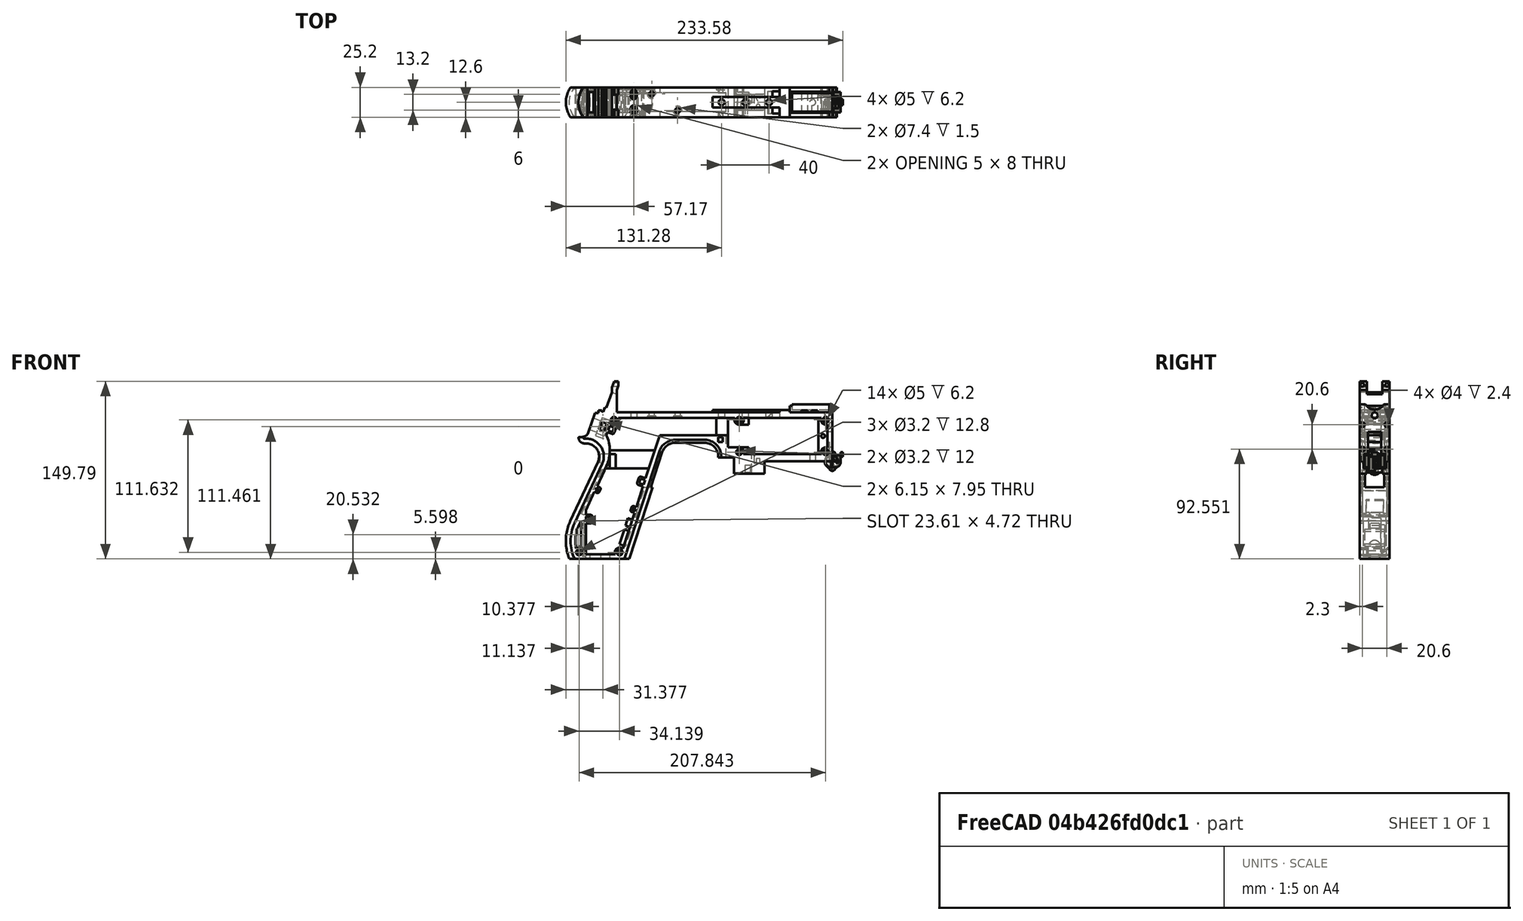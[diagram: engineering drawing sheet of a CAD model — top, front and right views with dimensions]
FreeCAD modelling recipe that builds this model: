
FCSTD DOCUMENT  (FreeCAD 1.0R39319 (Git))
Label: PICON-OF_ver_42
License: All rights reserved
LicenseURL: https://en.wikipedia.org/wiki/All_rights_reserved
objects: Sketcher::SketchObject×109, Part::Extrusion×52, Part::Cut×39, PartDesign::Pad×29, PartDesign::Pocket×18, PartDesign::Chamfer×15, PartDesign::Body×10, PartDesign::Fillet×6, PartDesign::SubtractivePipe×4, Part::Part2DObjectPython×4, PartDesign::SubtractiveLoft×4, PartDesign::Plane×2, PartDesign::SubShapeBinder×2, Part::Sweep×1, PartDesign::ShapeBinder×1, Part::MultiFuse×1, Mesh::Feature×1
note: 558 computed .brp shape members not serialized (recipe doc carries the construction recipe); baked Part::Feature solids carry a one-line shape summary decoded from their .brp

FEATURE [Sketcher::SketchObject] Sketch  label="corpo principale"
  ArcFitTolerance = 1e-06
  AttacherType = Attacher::AttachEngine3D
  AttachmentSupport = -> [XZ_Plane]
  FullyConstrained = true
  MakeInternals = false
  MapMode = 5
  Placement = pos=(0,0,0) rot=(1,0,0;1.5708rad)
  sketch-geometry (65):
    g0: LineSegment StartX=0 StartY=0 StartZ=0 EndX=-57.2 EndY=0 EndZ=0
    g1: LineSegment StartX=-57.2 StartY=0 StartZ=0 EndX=-57.2 EndY=-10.4 EndZ=0
    g2: LineSegment StartX=-57.2 StartY=-10.4 StartZ=0 EndX=-82.8 EndY=-10.4 EndZ=0
    g3: LineSegment StartX=-82.8 StartY=-10.4 StartZ=0 EndX=-82.8 EndY=3.2 EndZ=0
    g4: LineSegment StartX=-82.8 StartY=3.2 StartZ=0 EndX=-93.6 EndY=3.2 EndZ=0
    g5: LineSegment StartX=-93.6 StartY=3.2 StartZ=0 EndX=-93.6 EndY=4 EndZ=0
    g6: LineSegment StartX=-107.6 StartY=18 StartZ=0 EndX=-132.428 EndY=18 EndZ=0
    g7: LineSegment StartX=-145.743 StartY=8.32624 StartZ=0 EndX=-175.232 EndY=-82.4316 EndZ=0
    g8: LineSegment StartX=-175.232 StartY=-82.4316 StartZ=0 EndX=-217.232 EndY=-82.4316 EndZ=0
    g9: LineSegment StartX=-217.232 StartY=-52.1862 StartZ=0 EndX=-193.988 EndY=-2.33927 EndZ=0
    g10: LineSegment StartX=-206.196 StartY=23.0857 StartZ=0 EndX=-199.861 EndY=40.4914 EndZ=0
    g11: LineSegment StartX=-199.861 StartY=40.4914 StartZ=0 EndX=-197.061 EndY=40.4914 EndZ=0
    g12: LineSegment StartX=-197.061 StartY=40.4914 StartZ=0 EndX=-197.061 EndY=42.8914 EndZ=0
    g13: LineSegment StartX=-197.061 StartY=42.8914 StartZ=0 EndX=-194.261 EndY=42.8914 EndZ=0
    g14: LineSegment StartX=-194.261 StartY=42.8914 StartZ=0 EndX=-194.535 EndY=42.1397 EndZ=0
    g15: LineSegment StartX=-194.535 StartY=42.1397 StartZ=0 EndX=-193.031 EndY=41.5924 EndZ=0
    g16: LineSegment StartX=-193.031 StartY=41.5924 StartZ=0 EndX=-191.663 EndY=45.3512 EndZ=0
    g17: LineSegment StartX=-191.663 StartY=45.3512 StartZ=0 EndX=-190.536 EndY=44.9408 EndZ=0
    g18: LineSegment StartX=-190.536 StartY=44.9408 StartZ=0 EndX=-185.747 EndY=58.0965 EndZ=0
    g19: LineSegment StartX=-185.747 StartY=58.0965 StartZ=0 EndX=-185.747 EndY=62.0965 EndZ=0
    g20: LineSegment StartX=-185.747 StartY=62.0965 StartZ=0 EndX=-183.832 EndY=67.3588 EndZ=0
    g21: LineSegment StartX=-183.832 StartY=67.3588 StartZ=0 EndX=-180.232 EndY=67.3588 EndZ=0
    g22: LineSegment StartX=-180.232 StartY=67.3588 StartZ=0 EndX=-180.232 EndY=63.7588 EndZ=0
    g23: LineSegment StartX=-180.232 StartY=63.7588 StartZ=0 EndX=-181.6 EndY=60 EndZ=0
    g24: LineSegment StartX=-181.6 StartY=60 StartZ=0 EndX=-181.6 EndY=41.2 EndZ=0
    g25: LineSegment StartX=-181.6 StartY=41.2 StartZ=0 EndX=-100.8 EndY=41.2 EndZ=0
    g26: LineSegment StartX=-36 StartY=43.2 StartZ=0 EndX=-36 EndY=41.2 EndZ=0
    g27: LineSegment StartX=0 StartY=48 StartZ=0 EndX=0 EndY=0 EndZ=0
    g28: LineSegment StartX=-209.901 StartY=19.85 StartZ=0 EndX=-209.901 EndY=20.1 EndZ=0
    g29: LineSegment StartX=-208.001 StartY=22 StartZ=0 EndX=-207.747 EndY=22 EndZ=0
    g30: LineSegment StartX=-207.583 StartY=19 StartZ=0 EndX=-209.051 EndY=19 EndZ=0
    g31: ArcOfCircle CenterX=-208.001 CenterY=20.1 CenterZ=0 NormalX=0 NormalY=0 NormalZ=1 AngleXU=0 Radius=1.9 StartAngle=1.5708 EndAngle=3.14159
    g32: GeomPoint [constr] X=-209.901 Y=22 Z=0
    g33: ArcOfCircle CenterX=-209.051 CenterY=19.85 CenterZ=0 NormalX=0 NormalY=0 NormalZ=1 AngleXU=0 Radius=0.85 StartAngle=3.14159 EndAngle=4.71239
    g34: GeomPoint [constr] X=-209.901 Y=19 Z=0
    g35: ArcOfCircle CenterX=-207.747 CenterY=23.65 CenterZ=0 NormalX=0 NormalY=0 NormalZ=1 AngleXU=0 Radius=1.65 StartAngle=4.71239 EndAngle=5.93412
    g36: GeomPoint [constr] X=-206.591 Y=22 Z=0
    g37: LineSegment StartX=-4 StartY=6 StartZ=0 EndX=-4 EndY=36.4 EndZ=0
    g38: LineSegment StartX=-4 StartY=36.4 StartZ=0 EndX=-185.2 EndY=36.4 EndZ=0
    g39: LineSegment StartX=-185.2 StartY=36.4 StartZ=0 EndX=-190.441 EndY=22 EndZ=0
    g40: LineSegment StartX=-214.575 StartY=-78.4316 StartZ=0 EndX=-178.142 EndY=-78.4316 EndZ=0
    g41: LineSegment StartX=-178.142 StartY=-78.4316 StartZ=0 EndX=-145.51 EndY=22 EndZ=0
    g42: LineSegment StartX=-145.51 StartY=22 StartZ=0 EndX=-87.91 EndY=22 EndZ=0
    g43: LineSegment StartX=-87.91 StartY=22 StartZ=0 EndX=-87.91 EndY=11.6 EndZ=0
    g44: LineSegment StartX=-87.91 StartY=11.6 StartZ=0 EndX=-80.11 EndY=11.6 EndZ=0
    g45: LineSegment StartX=-80.11 StartY=11.6 StartZ=0 EndX=-80.11 EndY=6 EndZ=0
    g46: LineSegment StartX=-80.11 StartY=6 StartZ=0 EndX=-4 EndY=6 EndZ=0
    g47: LineSegment StartX=-190.363 StartY=-4.02975 StartZ=0 EndX=-213.607 EndY=-53.8767 EndZ=0
    g48: ArcOfCircle CenterX=-132.428 CenterY=4 CenterZ=0 NormalX=0 NormalY=0 NormalZ=1 AngleXU=0 Radius=14 StartAngle=1.5708 EndAngle=2.82743
    g49: GeomPoint [constr] X=-142.6 Y=18 Z=0
    g50: ArcOfCircle CenterX=-107.6 CenterY=4 CenterZ=0 NormalX=0 NormalY=0 NormalZ=1 AngleXU=0 Radius=14 StartAngle=0 EndAngle=1.5708
    g51: GeomPoint [constr] X=-93.6 Y=18 Z=0
    g52: ArcOfCircle CenterX=-184.801 CenterY=-67.3089 CenterZ=0 NormalX=0 NormalY=0 NormalZ=1 AngleXU=0 Radius=35.7833 StartAngle=2.70526 EndAngle=3.57792
    g53: ArcOfCircle CenterX=-207.583 CenterY=4 CenterZ=0 NormalX=0 NormalY=0 NormalZ=1 AngleXU=0 Radius=15 StartAngle=5.84685 EndAngle=7.85398
    g54: LineSegment [constr] StartX=-213.607 StartY=-53.8767 StartZ=0 EndX=-217.232 EndY=-52.1862 EndZ=0
    g55: ArcOfCircle CenterX=-184.801 CenterY=-67.3089 CenterZ=0 NormalX=0 NormalY=0 NormalZ=1 AngleXU=0 Radius=31.7833 StartAngle=2.70526 EndAngle=3.49911
    g56: ArcOfCircle CenterX=-218.095 CenterY=8.90192 CenterZ=0 NormalX=0 NormalY=0 NormalZ=1 AngleXU=0 Radius=30.5989 StartAngle=5.84685 EndAngle=6.72553
    g57: LineSegment StartX=-44.6 StartY=43.2 StartZ=0 EndX=-36 EndY=43.2 EndZ=0
    g58: LineSegment StartX=-100.8 StartY=41.2 StartZ=0 EndX=-44.6 EndY=41.2 EndZ=0
    g59: LineSegment StartX=-44.6 StartY=41.2 StartZ=0 EndX=-44.6 EndY=43.2 EndZ=0
    g60: LineSegment StartX=-2.4 StartY=48 StartZ=0 EndX=0 EndY=48 EndZ=0
    g61: LineSegment StartX=-36 StartY=41.2 StartZ=0 EndX=-2.4 EndY=41.2 EndZ=0
    g62: LineSegment StartX=-2.4 StartY=41.2 StartZ=0 EndX=-2.4 EndY=48 EndZ=0
    g63: LineSegment [constr] StartX=-181.6 StartY=36.4 StartZ=0 EndX=-152.209 EndY=36.4 EndZ=0
    g64: LineSegment [constr] StartX=-181.6 StartY=36.4 StartZ=0 EndX=-130.41 EndY=36.4 EndZ=0
  constraints (183):
    c: Coincident(g-1,g0)
    c: PointOnObject(g0,g-1)
    c: Coincident(g0,g1)
    c: Vertical(g1)
    c: Coincident(g1,g2)
    c: Horizontal(g2)
    c: Coincident(g2,g3)
    c: Vertical(g3)
    c: Coincident(g3,g4)
    c: Coincident(g4,g5)
    c: Vertical(g5)
    c: Horizontal(g6)
    c: Coincident(g7,g8)
    c: Horizontal(g8)
    c: Coincident(g10,g11)
    c: Horizontal(g11)
    c: Coincident(g11,g12)
    c: Vertical(g12)
    c: Coincident(g12,g13)
    c: Horizontal(g13)
    c: Coincident(g13,g14)
    c: Coincident(g14,g15)
    c: Coincident(g15,g16)
    c: Coincident(g16,g17)
    c: Coincident(g17,g18)
    c: Coincident(g18,g19)
    c: Vertical(g19)
    c: Coincident(g19,g20)
    c: Coincident(g20,g21)
    c: Horizontal(g21)
    c: Coincident(g21,g22)
    c: Vertical(g22)
    c: Coincident(g22,g23)
    c: Coincident(g23,g24)
    c: Vertical(g24)
    c: Coincident(g24,g25)
    c: Horizontal(g25)
    c: Coincident(g57,g26)
    c: Vertical(g26)
    c: Coincident(g26,g61)
    c: PointOnObject(g60,g-2)
    c: Coincident(g60,g27)
    c: Coincident(g27,g0)
    c: DistanceY(g27,g27) = 48
    c: DistanceY(g1,g1) = 10.4
    c: DistanceX(g0,g0) = 57.2
    c: DistanceX(g2,g2) = 25.6
    c: Horizontal(g4)
    c: DistanceY(g3,g3) = 13.6
    c: DistanceX(g4,g4) = 10.8
    c: DistanceY(g5,g51) = 14.8
    c: DistanceX(g49,g51) = 49
    c: Distance(g7,g49) = 105.6
    c: DistanceX(g61,g60) = 36
    c: DistanceX(g25,g25) = 80.8
    c: DistanceY(g24,g24) = 18.8
    c: DistanceY(g22,g22) = 3.6
    c: Distance(g23) = 4
    c: Angle(g-1,g23) = 1.22173
    c: DistanceX(g21,g21) = 3.6
    c: Distance(g20) = 5.6
    c: Angle(g-1,g20) = 1.22173
    c: DistanceY(g19,g19) = 4
    c: Distance(g18) = 14
    c: Angle(g-1,g18) = 1.22173
    c: Distance(g17) = 1.2
    c: Distance(g16) = 4
    c: Angle(g16) = 1.22173
    c: Perpendicular(g18,g17)
    c: Distance(g15) = 1.6
    c: Perpendicular(g16,g15)
    c: Distance(g14) = 0.8
    c: DistanceX(g13,g13) = 2.8
    c: Perpendicular(g15,g14)
    c: DistanceY(g12,g12) = 2.4
    c: DistanceX(g11,g11) = 2.8
    c: Distance(g9) = 55
    c: Angle(g9,g-1) = 2.00713
    c: Horizontal(g29)
    c: Vertical(g28)
    c: Horizontal(g30)
    c: PointOnObject(g32,g29)
    c: PointOnObject(g32,g28)
    c: Tangent(g29,g31) = 1.5708
    c: Tangent(g28,g31) = 1.5708
    c: PointOnObject(g34,g28)
    c: PointOnObject(g34,g30)
    c: Tangent(g28,g33) = 1.5708
    c: Tangent(g30,g33) = 1.5708
    c: PointOnObject(g36,g29)
    c: PointOnObject(g36,g10)
    c: Tangent(g29,g35) = -1.5708
    c: Tangent(g10,g35) = -1.5708
    c: Angle(g-1,g10) = 1.22173
    c: Radius(g35) = 1.65
    c: Vertical(g37)
    c: Coincident(g37,g38)
    c: Horizontal(g38)
    c: Coincident(g38,g39)
    c: Horizontal(g40)
    c: Coincident(g40,g41)
    c: Coincident(g41,g42)
    c: Horizontal(g42)
    c: Coincident(g42,g43)
    c: Vertical(g43)
    c: Coincident(g43,g44)
    c: Horizontal(g44)
    c: Coincident(g44,g45)
    c: Vertical(g45)
    c: Coincident(g45,g46)
    c: Coincident(g46,g37)
    c: Horizontal(g46)
    c: DistanceY(g0,g37) = 6
    c: DistanceX(g37,g0) = 4
    c: DistanceY(g37,g25) = 4.8
    c: DistanceX(g38,g38) = 181.2
    c: DistanceX(g42,g42) = 57.6
    c: DistanceY(g49,g41) = 4
    c: DistanceX(g41,g49) = 2.91
    c: DistanceY(g43,g43) = 10.4
    c: DistanceX(g44,g44) = 7.8
    c: DistanceY(g7,g40) = 4
    c: Distance(g47) = 55
    c: Angle(g-1,g39) = 1.22173
    c: PointOnObject(g49,g7)
    c: PointOnObject(g49,g6)
    c: Tangent(g7,g48) = -1.5708
    c: Tangent(g6,g48) = -1.5708
    c: PointOnObject(g51,g5)
    c: PointOnObject(g51,g6)
    c: Tangent(g5,g50) = -1.5708
    c: Tangent(g6,g50) = -1.5708
    c: Radius(g50) = 14
    c: Radius(g48) = 14
    c: DistanceX(g8,g8) = 42
    c: Angle(g7,g-1) = 1.88496
    c: Parallel(g41,g7)
    c: Parallel(g47,g9)
    c: Coincident(g52,g8)
    c: Tangent(g52,g9) = 1.5708
    c: DistanceX(g9,g8) = 0
    c: Tangent(g53,g9) = -1.5708
    c: Tangent(g53,g30) = -1.5708
    c: Diameter(g53) = 30
    c: DistanceY(g53,g0) = -4
    c: Coincident(g54,g47)
    c: Distance(g54) = 4
    c: Coincident(g54,g9)
    c: Coincident(g55,g40)
    c: Tangent(g55,g47) = -1.5708
    c: Coincident(g52,g55)
    c: Coincident(g56,g39)
    c: Tangent(g56,g47) = 1.5708
    c: Horizontal(g57)
    c: DistanceX(g57,g57) = 8.6
    c: Coincident(g58,g25)
    c: Horizontal(g58)
    c: Coincident(g59,g58)
    c: Vertical(g59)
    c: DistanceY(g58,g57) = 2
    c: DistanceX(g58,g58) = 56.2
    c: Coincident(g59,g57)
    c: DistanceY(g41,g36) = 0
    c: DistanceY(g36,g39) = 0
    c: DistanceY(g28,g28) = 0.25
    c: DistanceX(g30,g36) = 2.46
    c: DistanceX(g28,g29) = 1.9
    c: Coincident(g62,g60)
    c: Horizontal(g60)
    c: DistanceX(g62,g27) = 2.4
    c: Coincident(g61,g62)
    c: DistanceY(g26,g26) = 2
    c: Vertical(g62)
    c: DistanceY(g61,g60) = 6.8
    c: Horizontal(g61)
    c: Distance(g63) = 29.391
    c: PointOnObject(g63,g38)
    c: PointOnObject(g63,g38)
    c: Distance(g64) = 51.19
    c: PointOnObject(g64,g38)
    c: PointOnObject(g64,g38)
    c: DistanceX(g24,g63) = 0
    c: DistanceX(g24,g64) = 0
FEATURE [Part::Extrusion] Extrude  label="Extrude corpo principale"
  Base = -> Sketch
  Dir = (0,-1,2e-16)
  DirMode = 2
  FaceMakerClass = Part::FaceMakerBullseye
  FaceMakerMode = 3
  LengthFwd = 25.2
  LengthRev = 12.6
  Solid = true
  Symmetric = true
FEATURE [Sketcher::SketchObject] Sketch002  label="scavo grilletto"
  ArcFitTolerance = 1e-06
  AttachmentSupport = -> [XZ_Plane]
  ExternalGeometry = -> [Sketch]
  FullyConstrained = true
  MakeInternals = false
  MapMode = 5
  Placement = pos=(0,0,0) rot=(1,0,0;1.5708rad)
  sketch-geometry (4):
    g0: LineSegment StartX=-89.51 StartY=22 StartZ=0 EndX=-152.71 EndY=22 EndZ=0
    g1: LineSegment StartX=-152.71 StartY=22 StartZ=0 EndX=-167.006 EndY=-22 EndZ=0
    g2: LineSegment StartX=-167.006 StartY=-22 StartZ=0 EndX=-89.51 EndY=-22 EndZ=0
    g3: LineSegment StartX=-89.51 StartY=-22 StartZ=0 EndX=-89.51 EndY=22 EndZ=0
  constraints (12):
    c: Horizontal(g0)
    c: Coincident(g0,g1)
    c: Coincident(g1,g2)
    c: Horizontal(g2)
    c: Coincident(g2,g3)
    c: Coincident(g3,g0)
    c: Vertical(g3)
    c: Angle(g1,g0) = 1.88496
    c: DistanceY(g3,g3) = 44
    c: DistanceX(g0,g0) = 63.2
    c: DistanceX(g0,g-3) = 1.6
    c: DistanceY(g-3,g0) = 0
FEATURE [Sketcher::SketchObject] Sketch004  label="traiettoria arrotondamento impugnatura anteriore"
  ArcFitTolerance = 1e-06
  AttachmentSupport = -> [XZ_Plane]
  ExternalGeometry = -> [Sketch]
  FullyConstrained = true
  MakeInternals = false
  MapMode = 5
  Placement = pos=(0,0,0) rot=(1,0,0;1.5708rad)
  sketch-geometry (13):
    g0: LineSegment StartX=-175.232 StartY=-82.4316 StartZ=0 EndX=-145.743 EndY=8.32624 EndZ=0
    g1: LineSegment StartX=-93.6 StartY=3.2 StartZ=0 EndX=-93.6 EndY=4 EndZ=0
    g2: LineSegment StartX=-132.428 StartY=18 StartZ=0 EndX=-107.6 EndY=18 EndZ=0
    g3: ArcOfCircle CenterX=-132.428 CenterY=4 CenterZ=0 NormalX=0 NormalY=0 NormalZ=1 AngleXU=0 Radius=14 StartAngle=1.5708 EndAngle=2.82743
    g4: ArcOfCircle CenterX=-107.6 CenterY=4 CenterZ=0 NormalX=0 NormalY=0 NormalZ=1 AngleXU=0 Radius=14 StartAngle=0 EndAngle=1.5708
    g5: LineSegment StartX=-175.232 StartY=-82.4316 StartZ=0 EndX=-217.232 EndY=-82.4316 EndZ=0
    g6: LineSegment StartX=-217.232 StartY=-52.1862 StartZ=0 EndX=-193.988 EndY=-2.33927 EndZ=0
    g7: LineSegment StartX=-209.051 StartY=19 StartZ=0 EndX=-207.583 EndY=19 EndZ=0
    g8: LineSegment StartX=-209.901 StartY=20.1 StartZ=0 EndX=-209.901 EndY=19.85 EndZ=0
    g9: ArcOfCircle CenterX=-184.801 CenterY=-67.3089 CenterZ=0 NormalX=0 NormalY=0 NormalZ=1 AngleXU=0 Radius=35.7833 StartAngle=2.70526 EndAngle=3.57792
    g10: ArcOfCircle CenterX=-207.583 CenterY=4 CenterZ=0 NormalX=0 NormalY=0 NormalZ=1 AngleXU=0 Radius=15 StartAngle=5.84685 EndAngle=7.85398
    g11: ArcOfCircle CenterX=-209.051 CenterY=19.85 CenterZ=0 NormalX=0 NormalY=0 NormalZ=1 AngleXU=0 Radius=0.85 StartAngle=3.14159 EndAngle=4.71239
    g12: ArcOfCircle CenterX=-208.001 CenterY=20.1 CenterZ=0 NormalX=0 NormalY=0 NormalZ=1 AngleXU=0 Radius=1.9 StartAngle=1.5708 EndAngle=3.14159
  constraints (26):
    c: Coincident(g0,g-3)
    c: Coincident(g0,g-6)
    c: Coincident(g1,g-8)
    c: Coincident(g1,g-7)
    c: Coincident(g2,g-5)
    c: Coincident(g2,g-4)
    c: Coincident(g3,g2)
    c: Tangent(g3,g0) = 1.5708
    c: Coincident(g4,g1)
    c: Tangent(g4,g2) = 1.5708
    c: Coincident(g5,g0)
    c: Coincident(g5,g-9)
    c: Coincident(g6,g-12)
    c: Coincident(g6,g-11)
    c: Coincident(g7,g-15)
    c: Coincident(g7,g-14)
    c: Coincident(g8,g-16)
    c: Coincident(g8,g-17)
    c: Tangent(g9,g6) = 1.5708
    c: Coincident(g9,g5)
    c: Coincident(g10,g7)
    c: Tangent(g10,g6) = -1.5708
    c: Tangent(g11,g7) = -1.5708
    c: Coincident(g11,g8)
    c: Tangent(g12,g8) = -1.5708
    c: Coincident(g12,g-17)
FEATURE [PartDesign::Plane] DatumPlane  label="Piano per disegno arrotondamento impugnatura"
  AttachmentSupport = -> [Sketch]
  Length = 73.6581
  MapMode = 7
  Placement = pos=(-145.743,1.8e-15,8.32624) rot=(0.154555,0.154555,0.97582;1.59527rad)
  ResizeMode = 0
  Width = 303.511
FEATURE [Sketcher::SketchObject] Sketch005  label="forma arrotondamento impugnatura anteriore"
  ArcFitTolerance = 1e-06
  AttachmentSupport = -> [DatumPlane]
  FullyConstrained = true
  MakeInternals = false
  MapMode = 5
  Placement = pos=(-145.743,1.8e-15,8.32624) rot=(0.154555,0.154555,0.97582;1.59527rad)
  sketch-geometry (5):
    g0: GeomPoint [constr] X=0 Y=-4 Z=0
    g1: GeomPoint [constr] X=-12.6 Y=7.1e-15 Z=0
    g2: GeomPoint [constr] X=12.6 Y=4.97e-14 Z=0
    g3: LineSegment StartX=-12.6 StartY=7.1e-15 StartZ=0 EndX=12.6 EndY=4.97e-14 EndZ=0
    g4: ArcOfCircle CenterX=-3.88e-14 CenterY=17.845 CenterZ=0 NormalX=0 NormalY=0 NormalZ=1 AngleXU=0 Radius=21.845 StartAngle=4.09759 EndAngle=5.32718
  constraints (11):
    c: DistanceY(g0,g-1) = 4
    c: DistanceX(g-1,g0) = 0
    c: DistanceX(g1,g-1) = 12.6
    c: DistanceX(g-1,g2) = 12.6
    c: DistanceY(g-1,g2) = 0
    c: DistanceY(g-1,g1) = 0
    c: Coincident(g3,g1)
    c: Coincident(g3,g2)
    c: Coincident(g4,g1)
    c: Coincident(g4,g2)
    c: PointOnObject(g0,g4)
FEATURE [Part::Sweep] Sweep  label="Sweep impugnatura"
  Frenet = true
  Sections = -> [Sketch005]
  Solid = true
  Spine = -> Sketch [Edge32,Edge33,Edge34,Edge35,Edge36,Edge37,Edge38,Edge39,Edge40,Edge41,Edge42,Edge43,Edge44]
  Transition = 1
FEATURE [Sketcher::SketchObject] Sketch008  label="buchi e pulizie varie"
  ArcFitTolerance = 1e-06
  AttachmentSupport = -> [XZ_Plane]
  ExternalGeometry = -> [Sketch]
  FullyConstrained = true
  MakeInternals = false
  MapMode = 5
  Placement = pos=(0,0,0) rot=(1,0,0;1.5708rad)
  sketch-geometry (26):
    g0: LineSegment StartX=-96.278 StartY=20.155 StartZ=0 EndX=-92.278 EndY=20.155 EndZ=0
    g1: LineSegment StartX=-92.278 StartY=20.155 StartZ=0 EndX=-92.278 EndY=16.155 EndZ=0
    g2: LineSegment StartX=-92.278 StartY=16.155 StartZ=0 EndX=-96.278 EndY=16.155 EndZ=0
    g3: LineSegment StartX=-96.278 StartY=16.155 StartZ=0 EndX=-96.278 EndY=20.155 EndZ=0
    g4: LineSegment StartX=-222.232 StartY=-82.4316 StartZ=0 EndX=-170.232 EndY=-82.4316 EndZ=0
    g5: LineSegment StartX=-170.232 StartY=-82.4316 StartZ=0 EndX=-170.232 EndY=-86.4316 EndZ=0
    g6: LineSegment StartX=-170.232 StartY=-86.4316 StartZ=0 EndX=-222.232 EndY=-86.4316 EndZ=0
    g7: LineSegment StartX=-222.232 StartY=-86.4316 StartZ=0 EndX=-222.232 EndY=-82.4316 EndZ=0
    g8: LineSegment StartX=-213.901 StartY=20.1 StartZ=0 EndX=-213.901 EndY=26 EndZ=0
    g9: LineSegment StartX=-213.901 StartY=26 StartZ=0 EndX=-206.196 EndY=26 EndZ=0
    g10: LineSegment StartX=-17.4 StartY=42.8 StartZ=0 EndX=-12.4 EndY=42.8 EndZ=0
    g11: LineSegment StartX=-12.4 StartY=42.8 StartZ=0 EndX=-12.4 EndY=41.2 EndZ=0
    g12: LineSegment StartX=-12.4 StartY=41.2 StartZ=0 EndX=-17.4 EndY=41.2 EndZ=0
    g13: LineSegment StartX=-17.4 StartY=41.2 StartZ=0 EndX=-17.4 EndY=42.8 EndZ=0
    g14: LineSegment StartX=-25.9 StartY=42.8 StartZ=0 EndX=-20.9 EndY=42.8 EndZ=0
    g15: LineSegment StartX=-20.9 StartY=42.8 StartZ=0 EndX=-20.9 EndY=41.2 EndZ=0
    g16: LineSegment StartX=-20.9 StartY=41.2 StartZ=0 EndX=-25.9 EndY=41.2 EndZ=0
    g17: LineSegment StartX=-25.9 StartY=41.2 StartZ=0 EndX=-25.9 EndY=42.8 EndZ=0
    g18: GeomPoint [constr] X=-206.196 Y=23.0857 Z=0
    g19: GeomPoint [constr] X=-213.901 Y=20.1 Z=0
    g20: BSplineCurve PolesCount=4 KnotsCount=2 Degree=3 IsPeriodic=0
    g21-g24: Circle [constr] x4 (B-spline internal-alignment scaffolding for g20; pole/knot coordinates omitted)
    g25: LineSegment StartX=-206.196 StartY=26 StartZ=0 EndX=-206.196 EndY=23.0857 EndZ=0
  constraints (73):
    c: Horizontal(g0)
    c: Coincident(g1,g0)
    c: Vertical(g1)
    c: Coincident(g2,g1)
    c: Horizontal(g2)
    c: Coincident(g3,g2)
    c: Coincident(g3,g0)
    c: Vertical(g3)
    c: DistanceX(g0,g-4) = 4.368
    c: DistanceY(g0,g-4) = 1.845
    c: DistanceY(g1,g1) = 4
    c: DistanceX(g2,g2) = 4
    c: Horizontal(g4)
    c: Coincident(g5,g4)
    c: Vertical(g5)
    c: Coincident(g6,g5)
    c: Horizontal(g6)
    c: Coincident(g7,g6)
    c: Coincident(g7,g4)
    c: Vertical(g7)
    c: DistanceY(g7,g7) = 4
    c: DistanceX(g4,g-5) = 5
    c: DistanceX(g-5,g4) = 5
    c: DistanceY(g4,g-5) = 0
    c: Coincident(g9,g8)
    c: Parallel(g9,g-6)
    c: DistanceX(g8,g-8) = 4
    c: Horizontal(g10)
    c: Coincident(g11,g10)
    c: Vertical(g11)
    c: Coincident(g12,g11)
    c: Horizontal(g12)
    c: Coincident(g13,g12)
    c: Coincident(g13,g10)
    c: Vertical(g13)
    c: Horizontal(g14)
    c: Coincident(g15,g14)
    c: Vertical(g15)
    c: Coincident(g16,g15)
    c: Horizontal(g16)
    c: Coincident(g17,g16)
    c: Coincident(g17,g14)
    c: Vertical(g17)
    c: DistanceY(g11,g10) = 1.6
    c: DistanceX(g10,g10) = 5
    c: DistanceY(g15,g14) = 1.6
    c: DistanceX(g14,g14) = 5
    c: DistanceX(g15,g12) = 3.5
    c: DistanceX(g11,g-9) = 10
    c: DistanceY(g-9,g11) = 0
    c: DistanceY(g-9,g15) = 0
    c: Perpendicular(g8,g9)
    c: DistanceY(g-7,g9) = 4
    c: DistanceY(g8,g-8) = 0
    c: InternalAlignment(g18,g20)
    c: InternalAlignment(g19,g20)
    c: InternalAlignment(g21,g20)
    c: Weight(g21) = 1
    c: InternalAlignment(g22,g20)
    c: Equal(g22,g21)
    c: InternalAlignment(g23,g20)
    c: Equal(g23,g21)
    c: InternalAlignment(g24,g20)
    c: Equal(g24,g21)
    c: Coincident(g18,g-12)
    c: Coincident(g19,g8)
    c: Coincident(g25,g9)
    c: Coincident(g25,g20)
    c: Vertical(g25)
    c: DistanceY(g20,g23) = 0
    c: DistanceY(g22,g18) = 2.26
    c: DistanceX(g22,g18) = 0.93
    c: DistanceX(g20,g23) = 2.9
FEATURE [Part::Extrusion] Extrude004  label="Extrude Buchi e pulizie varie"
  Base = -> Sketch008
  Dir = (0,-1,2e-16)
  DirMode = 2
  FaceMakerClass = Part::FaceMakerBullseye
  FaceMakerMode = 3
  LengthFwd = 25.2
  LengthRev = 0
  Solid = true
  Symmetric = true
FEATURE [Sketcher::SketchObject] Sketch009  label="rinforzi"
  ArcFitTolerance = 1e-06
  AttachmentSupport = -> [XZ_Plane]
  ExternalGeometry = -> [Sketch]
  FullyConstrained = true
  MakeInternals = false
  MapMode = 5
  Placement = pos=(0,0,0) rot=(1,0,0;1.5708rad)
  sketch-geometry (9):
    g0: LineSegment StartX=-87.91 StartY=22 StartZ=0 EndX=-87.91 EndY=36.4 EndZ=0
    g1: LineSegment StartX=-87.91 StartY=36.4 StartZ=0 EndX=-97.91 EndY=36.4 EndZ=0
    g2: LineSegment StartX=-97.91 StartY=36.4 StartZ=0 EndX=-97.91 EndY=22 EndZ=0
    g3: LineSegment StartX=-97.91 StartY=22 StartZ=0 EndX=-87.91 EndY=22 EndZ=0
    g4: LineSegment StartX=-149.713 StartY=9.06563 StartZ=0 EndX=-154.586 EndY=-5.93437 EndZ=0
    g5: LineSegment StartX=-154.586 StartY=-5.93437 StartZ=0 EndX=-191.863 EndY=-5.93437 EndZ=0
    g6: LineSegment StartX=-191.863 StartY=-5.93437 StartZ=0 EndX=-191.863 EndY=9.06563 EndZ=0
    g7: LineSegment StartX=-191.863 StartY=9.06563 StartZ=0 EndX=-149.713 EndY=9.06563 EndZ=0
    g8: LineSegment [constr] StartX=-145.51 StartY=22 StartZ=0 EndX=-149.713 EndY=9.06563 EndZ=0
  constraints (25):
    c: Vertical(g0)
    c: Coincident(g1,g0)
    c: Horizontal(g1)
    c: Coincident(g2,g1)
    c: Vertical(g2)
    c: Coincident(g3,g2)
    c: Coincident(g3,g0)
    c: Horizontal(g3)
    c: Coincident(g0,g-4)
    c: DistanceX(g3,g3) = 10
    c: DistanceY(g0,g-3) = 0
    c: Coincident(g5,g4)
    c: Horizontal(g5)
    c: Coincident(g6,g5)
    c: Vertical(g6)
    c: Coincident(g7,g6)
    c: Coincident(g7,g4)
    c: Horizontal(g7)
    c: Distance(g8) = 13.6
    c: Parallel(g-6,g8)
    c: Coincident(g-6,g8)
    c: Parallel(g4,g-6)
    c: DistanceY(g4,g4) = 15
    c: Coincident(g4,g8)
    c: DistanceX(g-5,g5) = -1.5
FEATURE [Part::Extrusion] Extrude001  label="Extrude scavo grilletto"
  Base = -> Sketch002
  Dir = (0,-1,2e-16)
  DirMode = 2
  FaceMakerClass = Part::FaceMakerBullseye
  FaceMakerMode = 3
  LengthFwd = 16
  LengthRev = 0
  Solid = true
  Symmetric = true
FEATURE [Part::Extrusion] Extrude005  label="Extrude Rinforzi"
  Base = -> Sketch009
  Dir = (0,-1,2e-16)
  DirMode = 2
  FaceMakerClass = Part::FaceMakerBullseye
  FaceMakerMode = 3
  LengthFwd = 2
  LengthRev = 0
  Placement = pos=(0,12.6,0) rot=(0,0,1;0rad)
  Solid = true
  Symmetric = false
FEATURE [PartDesign::ShapeBinder] CopyCut
  TraceSupport = false
FEATURE [PartDesign::Plane] DatumPlane001
  AttachmentSupport = -> [CopyCut]
  Length = 283.944
  MapMode = 5
  Placement = pos=(0,12.6,0) rot=(0,0.707107,0.707107;3.14159rad)
  ResizeMode = 0
  Width = 188.15
FEATURE [Sketcher::SketchObject] Sketch010  label="buco neopixel"
  ArcFitTolerance = 1e-06
  AttachmentSupport = -> [XZ_Plane]
  ExternalGeometry = -> [Sketch]
  FullyConstrained = true
  MakeInternals = false
  MapMode = 5
  Placement = pos=(0,0,0) rot=(1,0,0;1.5708rad)
  sketch-geometry (5):
    g0: LineSegment [constr] StartX=-199.861 StartY=40.4914 StartZ=0 EndX=-201.368 EndY=36.3521 EndZ=0
    g1: LineSegment StartX=-201.368 StartY=36.3521 StartZ=0 EndX=-204.932 EndY=26.5605 EndZ=0
    g2: LineSegment StartX=-201.368 StartY=36.3521 StartZ=0 EndX=-180.2 EndY=28.6477 EndZ=0
    g3: LineSegment StartX=-180.2 StartY=28.6477 StartZ=0 EndX=-183.764 EndY=18.8561 EndZ=0
    g4: LineSegment StartX=-183.764 StartY=18.8561 StartZ=0 EndX=-204.932 EndY=26.5605 EndZ=0
  constraints (14):
    c: Parallel(g0,g-3)
    c: Distance(g0) = 4.405
    c: Coincident(g0,g-3)
    c: Coincident(g2,g1)
    c: Coincident(g3,g2)
    c: Coincident(g4,g3)
    c: Coincident(g4,g1)
    c: Parallel(g1,g-3)
    c: Distance(g1) = 10.42
    c: Coincident(g1,g0)
    c: Parallel(g2,g4)
    c: Perpendicular(g1,g2)
    c: DistanceX(g-4,g2) = 5
    c: Parallel(g3,g1)
FEATURE [Part::Extrusion] Extrude006  label="Extrude buco neopixel"
  Base = -> Sketch010
  Dir = (0,-1,2e-16)
  DirMode = 2
  FaceMakerClass = Part::FaceMakerBullseye
  FaceMakerMode = 3
  LengthFwd = 17.2
  LengthRev = 0
  Solid = true
  Symmetric = true
FEATURE [Sketcher::SketchObject] Sketch011  label="fermo grilletto"
  ArcFitTolerance = 1e-06
  AttachmentSupport = -> [XZ_Plane]
  ExternalGeometry = -> [Sketch]
  FullyConstrained = true
  MakeInternals = false
  MapMode = 5
  Placement = pos=(0,0,0) rot=(1,0,0;1.5708rad)
  sketch-geometry (18):
    g0: LineSegment [constr] StartX=-145.51 StartY=22 StartZ=0 EndX=-157.347 EndY=-14.4293 EndZ=0
    g1: LineSegment [constr] StartX=-157.347 StartY=-14.4293 StartZ=0 EndX=-157.841 EndY=-15.951 EndZ=0
    g2: LineSegment StartX=-161.151 StartY=-13.1932 StartZ=0 EndX=-155.825 EndY=-14.9237 EndZ=0
    g3: LineSegment StartX=-163.167 StartY=-14.2205 StartZ=0 EndX=-164.403 EndY=-18.0247 EndZ=0
    g4: LineSegment StartX=-163.376 StartY=-20.0408 StartZ=0 EndX=-158.05 EndY=-21.7713 EndZ=0
    g5: LineSegment StartX=-158.05 StartY=-21.7713 StartZ=0 EndX=-155.825 EndY=-14.9237 EndZ=0
    g6: LineSegment StartX=-161.645 StartY=-14.7149 StartZ=0 EndX=-157.841 EndY=-15.951 EndZ=0
    g7: LineSegment StartX=-157.841 StartY=-15.951 StartZ=0 EndX=-159.077 EndY=-19.7552 EndZ=0
    g8: LineSegment StartX=-159.077 StartY=-19.7552 StartZ=0 EndX=-162.881 EndY=-18.5191 EndZ=0
    g9: LineSegment StartX=-162.881 StartY=-18.5191 StartZ=0 EndX=-161.645 EndY=-14.7149 EndZ=0
    g10: LineSegment [constr] StartX=-161.645 StartY=-14.7149 StartZ=0 EndX=-161.151 EndY=-13.1932 EndZ=0
    g11: LineSegment [constr] StartX=-159.077 StartY=-19.7552 StartZ=0 EndX=-157.555 EndY=-20.2496 EndZ=0
    g12: LineSegment [constr] StartX=-159.077 StartY=-19.7552 StartZ=0 EndX=-159.572 EndY=-21.2769 EndZ=0
    g13: LineSegment [constr] StartX=-161.645 StartY=-14.7149 StartZ=0 EndX=-163.167 EndY=-14.2205 EndZ=0
    g14: ArcOfCircle CenterX=-161.645 CenterY=-14.7149 CenterZ=0 NormalX=0 NormalY=0 NormalZ=1 AngleXU=0 Radius=1.6 StartAngle=1.25664 EndAngle=2.82743
    g15: GeomPoint [constr] X=-162.673 Y=-12.6988 Z=0
    g16: ArcOfCircle CenterX=-162.881 CenterY=-18.5191 CenterZ=0 NormalX=0 NormalY=0 NormalZ=1 AngleXU=0 Radius=1.6 StartAngle=2.82743 EndAngle=4.39823
    g17: GeomPoint [constr] X=-164.897 Y=-19.5464 Z=0
  constraints (48):
    c: Parallel(g0,g-3)
    c: Distance(g0) = 38.304
    c: Coincident(g0,g-3)
    c: Parallel(g1,g-3)
    c: Distance(g1) = 1.6
    c: Coincident(g1,g0)
    c: Coincident(g5,g4)
    c: Coincident(g5,g2)
    c: Coincident(g7,g6)
    c: Coincident(g8,g7)
    c: Coincident(g9,g8)
    c: Coincident(g9,g6)
    c: Parallel(g7,g-3)
    c: Parallel(g9,g7)
    c: Perpendicular(g6,g7)
    c: Parallel(g6,g8)
    c: Distance(g6) = 4
    c: Distance(g9) = 4
    c: Parallel(g5,g7)
    c: Parallel(g9,g3)
    c: Parallel(g2,g6)
    c: Parallel(g4,g8)
    c: Parallel(g13,g6)
    c: Parallel(g10,g9)
    c: Parallel(g11,g8)
    c: Parallel(g12,g7)
    c: Distance(g10) = 1.6
    c: Distance(g13) = 1.6
    c: Distance(g12) = 1.6
    c: Distance(g11) = 1.6
    c: Coincident(g10,g6)
    c: Coincident(g13,g6)
    c: Coincident(g12,g7)
    c: Coincident(g11,g7)
    c: Distance(g10,g15) = 1.6
    c: Distance(g15,g13) = 1.6
    c: Distance(g4,g12) = 1.6
    c: Distance(g4,g11) = 1.6
    c: PointOnObject(g15,g2)
    c: Tangent(g3,g14) = -1.5708
    c: Tangent(g2,g14) = 1.5708
    c: PointOnObject(g17,g4)
    c: PointOnObject(g17,g3)
    c: Tangent(g4,g16) = -1.5708
    c: Tangent(g3,g16) = -1.5708
    c: Equal(g16,g14)
    c: Coincident(g16,g8)
    c: Coincident(g6,g1)
FEATURE [Part::Extrusion] Extrude007  label="Extrude fermo grilletto"
  Base = -> Sketch011
  Dir = (0,-1,2e-16)
  DirMode = 2
  FaceMakerClass = Part::FaceMakerBullseye
  FaceMakerMode = 3
  LengthFwd = 25.2
  LengthRev = 0
  Solid = true
  Symmetric = true
FEATURE [Sketcher::SketchObject] Sketch012  label="buco oled"
  ArcFitTolerance = 1e-06
  AttachmentSupport = -> [XZ_Plane]
  ExternalGeometry = -> [Sketch]
  FullyConstrained = true
  MakeInternals = false
  MapMode = 5
  Placement = pos=(0,0,0) rot=(1,0,0;1.5708rad)
  sketch-geometry (4):
    g0: LineSegment StartX=-185.747 StartY=58.0965 StartZ=0 EndX=-180.232 EndY=56.0891 EndZ=0
    g1: LineSegment StartX=-185.747 StartY=58.0965 StartZ=0 EndX=-185.747 EndY=67.3588 EndZ=0
    g2: LineSegment StartX=-185.747 StartY=67.3588 StartZ=0 EndX=-180.232 EndY=67.3588 EndZ=0
    g3: LineSegment StartX=-180.232 StartY=67.3588 StartZ=0 EndX=-180.232 EndY=56.0891 EndZ=0
  constraints (10):
    c: Coincident(g1,g0)
    c: Coincident(g2,g1)
    c: Coincident(g3,g2)
    c: Coincident(g3,g0)
    c: Parallel(g1,g-5)
    c: Perpendicular(g-3,g0)
    c: Parallel(g2,g-6)
    c: Parallel(g3,g-4)
    c: Coincident(g0,g-5)
    c: Coincident(g2,g-6)
FEATURE [Part::Extrusion] Extrude008  label="Extrude buco oled"
  Base = -> Sketch012
  Dir = (0,-1,2e-16)
  DirMode = 2
  FaceMakerClass = Part::FaceMakerBullseye
  FaceMakerMode = 3
  LengthFwd = 12.8
  LengthRev = 0
  Solid = true
  Symmetric = true
FEATURE [Sketcher::SketchObject] Sketch013  label="buco pompa"
  ArcFitTolerance = 1e-06
  AttachmentSupport = -> [XZ_Plane]
  ExternalGeometry = -> [Sketch]
  FullyConstrained = true
  MakeInternals = false
  MapMode = 5
  Placement = pos=(0,0,0) rot=(1,0,0;1.5708rad)
  sketch-geometry (8):
    g0: LineSegment StartX=-82.8 StartY=-10.4 StartZ=0 EndX=-82.8 EndY=-9.6 EndZ=0
    g1: LineSegment StartX=-82.8 StartY=-9.6 StartZ=0 EndX=-67.9 EndY=-9.6 EndZ=0
    g2: LineSegment StartX=-67.9 StartY=-9.6 StartZ=0 EndX=-67.9 EndY=6 EndZ=0
    g3: LineSegment StartX=-67.9 StartY=6 StartZ=0 EndX=-65.9 EndY=6 EndZ=0
    g4: LineSegment StartX=-65.9 StartY=6 StartZ=0 EndX=-65.9 EndY=-1.7 EndZ=0
    g5: LineSegment StartX=-65.9 StartY=-1.7 StartZ=0 EndX=-57.2 EndY=-1.7 EndZ=0
    g6: LineSegment StartX=-57.2 StartY=-1.7 StartZ=0 EndX=-57.2 EndY=-10.4 EndZ=0
    g7: LineSegment StartX=-57.2 StartY=-10.4 StartZ=0 EndX=-82.8 EndY=-10.4 EndZ=0
  constraints (22):
    c: Vertical(g0)
    c: Coincident(g1,g0)
    c: Horizontal(g1)
    c: Coincident(g2,g1)
    c: Vertical(g2)
    c: Coincident(g3,g2)
    c: Horizontal(g3)
    c: Coincident(g4,g3)
    c: Vertical(g4)
    c: Coincident(g5,g4)
    c: Horizontal(g5)
    c: Coincident(g6,g5)
    c: Vertical(g6)
    c: Coincident(g7,g6)
    c: Coincident(g7,g0)
    c: DistanceY(g0,g0) = 0.8
    c: DistanceY(g6,g6) = 8.7
    c: DistanceX(g1,g1) = 14.9
    c: DistanceX(g3,g3) = 2
    c: Coincident(g0,g-4)
    c: DistanceY(g2,g-6) = 0
    c: Coincident(g6,g-5)
FEATURE [Part::Extrusion] Extrude009  label="Extrude buco pompa"
  Base = -> Sketch013
  Dir = (0,-1,2e-16)
  DirMode = 2
  FaceMakerClass = Part::FaceMakerBullseye
  FaceMakerMode = 3
  LengthFwd = 13.2
  LengthRev = 0
  Solid = true
  Symmetric = true
FEATURE [Sketcher::SketchObject] Sketch014  label="buco frontale"
  ArcFitTolerance = 1e-06
  AttachmentSupport = -> [XZ_Plane]
  ExternalGeometry = -> [Sketch]
  FullyConstrained = true
  MakeInternals = false
  MapMode = 5
  Placement = pos=(0,0,0) rot=(1,0,0;1.5708rad)
  sketch-geometry (10):
    g0: LineSegment StartX=0 StartY=0 StartZ=0 EndX=0 EndY=24.671 EndZ=0
    g1: LineSegment StartX=0 StartY=24.671 StartZ=0 EndX=-4 EndY=24.671 EndZ=0
    g2: LineSegment StartX=-4 StartY=24.671 StartZ=0 EndX=-4 EndY=16 EndZ=0
    g3: LineSegment StartX=-4 StartY=16 StartZ=0 EndX=-2.4 EndY=16 EndZ=0
    g4: LineSegment StartX=-2.4 StartY=16 StartZ=0 EndX=-2.4 EndY=10 EndZ=0
    g5: LineSegment StartX=-2.4 StartY=10 StartZ=0 EndX=-12 EndY=10 EndZ=0
    g6: LineSegment StartX=-12 StartY=10 StartZ=0 EndX=-12 EndY=6 EndZ=0
    g7: LineSegment StartX=-12 StartY=6 StartZ=0 EndX=-2.4 EndY=6 EndZ=0
    g8: LineSegment StartX=-2.4 StartY=6 StartZ=0 EndX=-2.4 EndY=0 EndZ=0
    g9: LineSegment StartX=-2.4 StartY=0 StartZ=0 EndX=0 EndY=0 EndZ=0
  constraints (29):
    c: Vertical(g0)
    c: Coincident(g1,g0)
    c: Horizontal(g1)
    c: Coincident(g2,g1)
    c: Vertical(g2)
    c: Coincident(g3,g2)
    c: Horizontal(g3)
    c: Coincident(g4,g3)
    c: Vertical(g4)
    c: Coincident(g5,g4)
    c: Horizontal(g5)
    c: Coincident(g6,g5)
    c: Vertical(g6)
    c: Coincident(g7,g6)
    c: Coincident(g8,g7)
    c: Vertical(g8)
    c: Coincident(g9,g8)
    c: Coincident(g9,g0)
    c: Horizontal(g9)
    c: DistanceY(g0,g0) = 24.671
    c: Horizontal(g7)
    c: DistanceY(g6,g6) = 4
    c: DistanceY(g4,g4) = 6
    c: DistanceX(g9,g9) = 2.4
    c: Coincident(g0,g-1)
    c: DistanceY(g-3,g7) = 0
    c: DistanceX(g8,g4) = 0
    c: DistanceX(g-3,g1) = 0
    c: DistanceX(g6,g-3) = 8
FEATURE [Part::Extrusion] Extrude010  label="Extrude buco frontale"
  Base = -> Sketch014
  Dir = (0,-1,2e-16)
  DirMode = 2
  FaceMakerClass = Part::FaceMakerBullseye
  FaceMakerMode = 3
  LengthFwd = 11.2
  LengthRev = 0
  Solid = true
  Symmetric = true
FEATURE [Sketcher::SketchObject] Sketch015  label="guida rail"
  ArcFitTolerance = 1e-06
  AttachmentSupport = -> [XZ_Plane]
  ExternalGeometry = -> [Sketch]
  FullyConstrained = true
  MakeInternals = false
  MapMode = 5
  Placement = pos=(0,0,0) rot=(1,0,0;1.5708rad)
  sketch-geometry (4):
    g0: LineSegment StartX=-100.8 StartY=43.2 StartZ=0 EndX=-44.6 EndY=43.2 EndZ=0
    g1: LineSegment StartX=-44.6 StartY=43.2 StartZ=0 EndX=-44.6 EndY=41.2 EndZ=0
    g2: LineSegment StartX=-44.6 StartY=41.2 StartZ=0 EndX=-100.8 EndY=41.2 EndZ=0
    g3: LineSegment StartX=-100.8 StartY=41.2 StartZ=0 EndX=-100.8 EndY=43.2 EndZ=0
  constraints (9):
    c: Horizontal(g0)
    c: Coincident(g1,g0)
    c: Coincident(g2,g1)
    c: Coincident(g3,g2)
    c: Coincident(g3,g0)
    c: Vertical(g3)
    c: Coincident(g2,g-3)
    c: Coincident(g1,g-3)
    c: Coincident(g0,g-4)
FEATURE [Part::Extrusion] Extrude011  label="Extrude guida rail"
  Base = -> Sketch015
  Dir = (0,-1,2e-16)
  DirMode = 2
  FaceMakerClass = Part::FaceMakerBullseye
  FaceMakerMode = 3
  LengthFwd = 9
  LengthRev = 0
  Solid = true
  Symmetric = true
FEATURE [Sketcher::SketchObject] Sketch016  label="guide per coperture laterali"
  ArcFitTolerance = 1e-06
  AttachmentSupport = -> [XZ_Plane]
  ExternalGeometry = -> [Sketch]
  FullyConstrained = true
  MakeInternals = false
  MapMode = 5
  Placement = pos=(0,0,0) rot=(1,0,0;1.5708rad)
  sketch-geometry (14):
    g0: Circle CenterX=-5.6 CenterY=7.6 CenterZ=0 NormalX=0 NormalY=0 NormalZ=1 AngleXU=0 Radius=1.6
    g1: Circle CenterX=-5.6 CenterY=7.6 CenterZ=0 NormalX=0 NormalY=0 NormalZ=1 AngleXU=0 Radius=4
    g2: Circle CenterX=-5.6 CenterY=34.8 CenterZ=0 NormalX=0 NormalY=0 NormalZ=1 AngleXU=0 Radius=1.6
    g3: Circle CenterX=-5.6 CenterY=34.8 CenterZ=0 NormalX=0 NormalY=0 NormalZ=1 AngleXU=0 Radius=4
    g4: Circle CenterX=-184.08 CenterY=34.8 CenterZ=0 NormalX=0 NormalY=0 NormalZ=1 AngleXU=0 Radius=1.6
    g5: Circle CenterX=-184.08 CenterY=34.8 CenterZ=0 NormalX=0 NormalY=0 NormalZ=1 AngleXU=0 Radius=4
    g6: Circle CenterX=-179.305 CenterY=-76.8316 CenterZ=0 NormalX=0 NormalY=0 NormalZ=1 AngleXU=0 Radius=1.6
    g7: Circle CenterX=-179.305 CenterY=-76.8316 CenterZ=0 NormalX=0 NormalY=0 NormalZ=1 AngleXU=0 Radius=4
    g8: Circle CenterX=-213.443 CenterY=-76.8316 CenterZ=0 NormalX=0 NormalY=0 NormalZ=1 AngleXU=0 Radius=1.6
    g9: Circle CenterX=-213.443 CenterY=-76.8316 CenterZ=0 NormalX=0 NormalY=0 NormalZ=1 AngleXU=0 Radius=4
    g10: Circle CenterX=-78.51 CenterY=7.6 CenterZ=0 NormalX=0 NormalY=0 NormalZ=1 AngleXU=0 Radius=1.6
    g11: Circle CenterX=-78.51 CenterY=7.6 CenterZ=0 NormalX=0 NormalY=0 NormalZ=1 AngleXU=0 Radius=4
    g12: Circle CenterX=-78.51 CenterY=34.8 CenterZ=0 NormalX=0 NormalY=0 NormalZ=1 AngleXU=0 Radius=1.6
    g13: Circle CenterX=-78.51 CenterY=34.8 CenterZ=0 NormalX=0 NormalY=0 NormalZ=1 AngleXU=0 Radius=4
  constraints (35):
    c: Diameter(g0) = 3.2
    c: Diameter(g1) = 8
    c: Coincident(g0,g1)
    c: Diameter(g2) = 3.2
    c: Diameter(g3) = 8
    c: Coincident(g3,g2)
    c: Tangent(g2,g-7)
    c: Diameter(g4) = 3.2
    c: Diameter(g5) = 8
    c: Coincident(g5,g4)
    c: Tangent(g4,g-7)
    c: Tangent(g4,g-8)
    c: Diameter(g6) = 3.2
    c: Diameter(g7) = 8
    c: Coincident(g7,g6)
    c: Tangent(g6,g-9)
    c: Tangent(g6,g-10)
    c: Diameter(g8) = 3.2
    c: Diameter(g9) = 8
    c: Coincident(g9,g8)
    c: Tangent(g8,g-10)
    c: Tangent(g8,g-11)
    c: Diameter(g10) = 3.2
    c: Diameter(g11) = 8
    c: Diameter(g12) = 3.2
    c: Diameter(g13) = 8
    c: Coincident(g12,g13)
    c: Coincident(g10,g11)
    c: Tangent(g12,g-7)
    c: DistanceX(g12,g10) = 0
    c: Tangent(g2,g-6)
    c: Tangent(g0,g-6)
    c: Tangent(g0,g-3)
    c: Tangent(g10,g-3)
    c: Tangent(g10,g-4)
FEATURE [Part::Extrusion] Extrude012  label="extrude guide per coperture laterali"
  Base = -> Sketch016
  Dir = (0,-1,2e-16)
  DirMode = 2
  FaceMakerClass = Part::FaceMakerBullseye
  FaceMakerMode = 3
  LengthFwd = 25.2
  LengthRev = 0
  Solid = true
  Symmetric = true
FEATURE [Sketcher::SketchObject] Sketch017  label="supporto CAM"
  ArcFitTolerance = 1e-06
  AttachmentSupport = -> [XZ_Plane]
  ExternalGeometry = -> [Sketch]
  FullyConstrained = true
  MakeInternals = false
  MapMode = 5
  Placement = pos=(0,0,0) rot=(1,0,0;1.5708rad)
  sketch-geometry (6):
    g0: LineSegment StartX=-2.4 StartY=48 StartZ=0 EndX=-2.4 EndY=41.2 EndZ=0
    g1: LineSegment StartX=-2.4 StartY=48 StartZ=0 EndX=-34 EndY=48 EndZ=0
    g2: LineSegment StartX=-34 StartY=48 StartZ=0 EndX=-34 EndY=46.72 EndZ=0
    g3: LineSegment StartX=-34 StartY=46.72 StartZ=0 EndX=-36 EndY=46.72 EndZ=0
    g4: LineSegment StartX=-36 StartY=46.72 StartZ=0 EndX=-36 EndY=41.2 EndZ=0
    g5: LineSegment StartX=-36 StartY=41.2 StartZ=0 EndX=-2.4 EndY=41.2 EndZ=0
  constraints (15):
    c: Coincident(g1,g0)
    c: Horizontal(g1)
    c: Coincident(g2,g1)
    c: Vertical(g2)
    c: Coincident(g3,g2)
    c: Horizontal(g3)
    c: Coincident(g4,g3)
    c: Coincident(g5,g4)
    c: DistanceX(g1,g0) = 31.6
    c: Coincident(g5,g0)
    c: Vertical(g4)
    c: DistanceY(g2,g1) = 1.28
    c: Coincident(g0,g-3)
    c: Coincident(g0,g-3)
    c: Coincident(g4,g-4)
FEATURE [Part::Extrusion] Extrude013  label="Extrude supporto CAM"
  Base = -> Sketch017
  Dir = (0,-1,2e-16)
  DirMode = 2
  FaceMakerClass = Part::FaceMakerBullseye
  FaceMakerMode = 3
  LengthFwd = 17.8
  LengthRev = 0
  Solid = true
  Symmetric = true
FEATURE [Sketcher::SketchObject] Sketch018  label="Scavo CAM"
  ArcFitTolerance = 1e-06
  AttachmentSupport = -> [YZ_Plane]
  ExternalGeometry = -> [Sketch]
  FullyConstrained = true
  MakeInternals = false
  MapMode = 5
  Placement = pos=(0,0,0) rot=(0.57735,0.57735,0.57735;2.0944rad)
  sketch-geometry (4):
    g0: LineSegment StartX=-7.73 StartY=48 StartZ=0 EndX=7.73 EndY=48 EndZ=0
    g1: LineSegment [constr] StartX=1.07e-14 StartY=48 StartZ=0 EndX=0 EndY=43.5155 EndZ=0
    g2: ArcOfCircle CenterX=9e-15 CenterY=52.42 CenterZ=0 NormalX=0 NormalY=0 NormalZ=1 AngleXU=0 Radius=8.90445 StartAngle=3.66102 EndAngle=5.76376
    g3: Circle [constr] CenterX=9e-15 CenterY=52.42 CenterZ=0 NormalX=0 NormalY=0 NormalZ=1 AngleXU=0 Radius=8.9
  constraints (13):
    c: Horizontal(g0)
    c: DistanceY(g-3,g0) = 0
    c: DistanceX(g0,g0) = 15.46
    c: DistanceX(g0,g-3) = 7.73
    c: DistanceX(g-3) = 0
    c: Coincident(g1,g-3)
    c: PointOnObject(g1,g-2)
    c: Coincident(g2,g0)
    c: Coincident(g2,g0)
    c: PointOnObject(g1,g2)
    c: Diameter(g3) = 17.8
    c: DistanceY(g1,g3) = 4.42
    c: Coincident(g2,g3)
FEATURE [Part::Extrusion] Extrude014  label="Extrude Scavo CAM"
  Base = -> Sketch018
  Dir = (1,0,0)
  DirMode = 2
  FaceMakerClass = Part::FaceMakerBullseye
  FaceMakerMode = 3
  LengthFwd = -34
  LengthRev = 0
  Solid = true
  Symmetric = false
FEATURE [Sketcher::SketchObject] Sketch019  label="scavo rumble"
  ArcFitTolerance = 1e-06
  AttachmentSupport = -> [XZ_Plane]
  ExternalGeometry = -> [Sketch]
  FullyConstrained = true
  MakeInternals = false
  MapMode = 5
  Placement = pos=(0,0,0) rot=(1,0,0;1.5708rad)
  sketch-geometry (6):
    g0: LineSegment StartX=-164.266 StartY=-23.4275 StartZ=0 EndX=-159.13 EndY=-25.0962 EndZ=0
    g1: LineSegment StartX=-159.13 StartY=-25.0962 StartZ=0 EndX=-166.238 EndY=-46.9705 EndZ=0
    g2: LineSegment StartX=-166.238 StartY=-46.9705 StartZ=0 EndX=-171.373 EndY=-45.3018 EndZ=0
    g3: LineSegment StartX=-171.373 StartY=-45.3018 StartZ=0 EndX=-164.266 EndY=-23.4275 EndZ=0
    g4: LineSegment [constr] StartX=-145.51 StartY=22 StartZ=0 EndX=-160.652 EndY=-24.6018 EndZ=0
    g5: LineSegment [constr] StartX=-159.13 StartY=-25.0962 StartZ=0 EndX=-160.652 EndY=-24.6018 EndZ=0
  constraints (17):
    c: Coincident(g1,g0)
    c: Coincident(g2,g1)
    c: Coincident(g3,g2)
    c: Coincident(g3,g0)
    c: Parallel(g3,g-3)
    c: Parallel(g3,g1)
    c: Perpendicular(g3,g0)
    c: Perpendicular(g2,g3)
    c: Distance(g2,g0) = 23
    c: Parallel(g4,g-3)
    c: Distance(g4) = 49
    c: Coincident(g4,g-3)
    c: Parallel(g5,g0)
    c: Distance(g5) = 1.6
    c: Coincident(g5,g0)
    c: Distance(g5,g0) = 3.8
    c: Coincident(g5,g4)
FEATURE [Part::Extrusion] Extrude015  label="scavo rumble001"
  Base = -> Sketch019
  Dir = (0,-1,2e-16)
  DirMode = 2
  FaceMakerClass = Part::FaceMakerBullseye
  FaceMakerMode = 3
  LengthFwd = 21
  LengthRev = 0
  Solid = true
  Symmetric = true
FEATURE [Sketcher::SketchObject] Sketch020  label="fermo rumble"
  ArcFitTolerance = 1e-06
  AttachmentSupport = -> [XZ_Plane]
  ExternalGeometry = -> [Sketch019,Sketch]
  FullyConstrained = true
  MakeInternals = false
  MapMode = 5
  Placement = pos=(0,0,0) rot=(1,0,0;1.5708rad)
  sketch-geometry (16):
    g0: LineSegment [constr] StartX=-166.4 StartY=-42.2914 StartZ=0 EndX=-167.759 EndY=-46.4761 EndZ=0
    g1: LineSegment [constr] StartX=-167.759 StartY=-46.4761 StartZ=0 EndX=-166.238 EndY=-46.9705 EndZ=0
    g2: LineSegment StartX=-167.812 StartY=-39.5193 StartZ=0 EndX=-165.72 EndY=-40.1991 EndZ=0
    g3: LineSegment StartX=-165.72 StartY=-40.1991 StartZ=0 EndX=-166.4 EndY=-42.2914 EndZ=0
    g4: LineSegment StartX=-166.4 StartY=-42.2914 StartZ=0 EndX=-168.492 EndY=-41.6116 EndZ=0
    g5: LineSegment StartX=-168.492 StartY=-41.6116 StartZ=0 EndX=-167.812 EndY=-39.5193 EndZ=0
    g6: LineSegment StartX=-167.318 StartY=-37.9976 StartZ=0 EndX=-163.894 EndY=-39.11 EndZ=0
    g7: LineSegment StartX=-163.894 StartY=-39.11 StartZ=0 EndX=-165.501 EndY=-44.0555 EndZ=0
    g8: LineSegment StartX=-165.501 StartY=-44.0555 StartZ=0 EndX=-168.924 EndY=-42.9431 EndZ=0
    g9: LineSegment StartX=-169.952 StartY=-40.9269 StartZ=0 EndX=-169.334 EndY=-39.0248 EndZ=0
    g10: LineSegment [constr] StartX=-169.334 StartY=-39.0248 StartZ=0 EndX=-168.839 EndY=-37.5031 EndZ=0
    g11: LineSegment [constr] StartX=-168.839 StartY=-37.5031 StartZ=0 EndX=-167.318 EndY=-37.9976 EndZ=0
    g12: ArcOfCircle CenterX=-168.43 CenterY=-41.4214 CenterZ=0 NormalX=0 NormalY=0 NormalZ=1 AngleXU=0 Radius=1.6 StartAngle=2.82743 EndAngle=4.39823
    g13: GeomPoint [constr] X=-170.446 Y=-42.4486 Z=0
    g14: ArcOfCircle CenterX=-167.812 CenterY=-39.5193 CenterZ=0 NormalX=0 NormalY=0 NormalZ=1 AngleXU=0 Radius=1.6 StartAngle=1.25664 EndAngle=2.82743
    g15: GeomPoint [constr] X=-168.839 Y=-37.5031 Z=0
  constraints (42):
    c: Parallel(g0,g-4)
    c: Distance(g0) = 4.4
    c: Coincident(g1,g0)
    c: Perpendicular(g0,g1)
    c: Distance(g1) = 1.6
    c: Coincident(g1,g-5)
    c: Coincident(g3,g2)
    c: Coincident(g4,g3)
    c: Coincident(g5,g4)
    c: Coincident(g5,g2)
    c: Parallel(g3,g-4)
    c: Parallel(g3,g5)
    c: Perpendicular(g2,g3)
    c: Parallel(g4,g2)
    c: Distance(g2) = 2.2
    c: Distance(g3) = 2.2
    c: Coincident(g7,g6)
    c: Coincident(g8,g7)
    c: Parallel(g7,g-4)
    c: Parallel(g7,g9)
    c: Perpendicular(g6,g7)
    c: Parallel(g6,g8)
    c: Distance(g6,g15) = 5.2
    c: Distance(g7) = 5.2
    c: Coincident(g11,g10)
    c: Parallel(g10,g9)
    c: Parallel(g11,g6)
    c: Distance(g10) = 1.6
    c: Distance(g11) = 1.6
    c: Coincident(g10,g15)
    c: Distance(g11,g2) = 1.6
    c: Distance(g2,g10) = 1.6
    c: PointOnObject(g13,g8)
    c: PointOnObject(g13,g9)
    c: Tangent(g8,g12) = 1.5708
    c: Tangent(g9,g12) = 1.5708
    c: PointOnObject(g15,g9)
    c: Tangent(g6,g14) = 1.5708
    c: Tangent(g9,g14) = 1.5708
    c: Equal(g12,g14)
    c: Coincident(g6,g11)
    c: Coincident(g3,g0)
FEATURE [Part::Extrusion] Extrude016  label="Extrude fermo rumble"
  Base = -> Sketch020
  Dir = (0,-1,2e-16)
  DirMode = 2
  FaceMakerClass = Part::FaceMakerBullseye
  FaceMakerMode = 3
  LengthFwd = 25.2
  LengthRev = 0
  Solid = true
  Symmetric = true
FEATURE [Sketcher::SketchObject] Sketch021  label="perno fermo rumble001"
  ArcFitTolerance = 1e-06
  AttachmentSupport = -> [XZ_Plane001]
  FullyConstrained = true
  MakeInternals = false
  MapMode = 5
  Placement = pos=(0,0,0) rot=(1,0,0;1.5708rad)
  sketch-geometry (16):
    g0: LineSegment StartX=0 StartY=0.45 StartZ=0 EndX=0 EndY=1.55 EndZ=0
    g1: LineSegment StartX=0.45 StartY=2 StartZ=0 EndX=1.55 EndY=2 EndZ=0
    g2: LineSegment StartX=2 StartY=1.55 StartZ=0 EndX=2 EndY=0.45 EndZ=0
    g3: LineSegment StartX=1.55 StartY=0 StartZ=0 EndX=0.45 EndY=0 EndZ=0
    g4: ArcOfCircle [constr] CenterX=0.45 CenterY=1.55 CenterZ=0 NormalX=0 NormalY=0 NormalZ=1 AngleXU=0 Radius=0.45 StartAngle=1.5708 EndAngle=3.14159
    g5: GeomPoint [constr] X=0 Y=2 Z=0
    g6: LineSegment StartX=0.45 StartY=2 StartZ=0 EndX=0 EndY=1.55 EndZ=0
    g7: ArcOfCircle [constr] CenterX=1.55 CenterY=1.55 CenterZ=0 NormalX=0 NormalY=0 NormalZ=1 AngleXU=0 Radius=0.45 StartAngle=0 EndAngle=1.5708
    g8: GeomPoint [constr] X=2 Y=2 Z=0
    g9: LineSegment StartX=2 StartY=1.55 StartZ=0 EndX=1.55 EndY=2 EndZ=0
    g10: ArcOfCircle [constr] CenterX=1.55 CenterY=0.45 CenterZ=0 NormalX=0 NormalY=0 NormalZ=1 AngleXU=0 Radius=0.45 StartAngle=4.71239 EndAngle=6.28319
    g11: GeomPoint [constr] X=2 Y=0 Z=0
    g12: LineSegment StartX=1.55 StartY=0 StartZ=0 EndX=2 EndY=0.45 EndZ=0
    g13: ArcOfCircle [constr] CenterX=0.45 CenterY=0.45 CenterZ=0 NormalX=0 NormalY=0 NormalZ=1 AngleXU=0 Radius=0.45 StartAngle=3.14159 EndAngle=4.71239
    g14: GeomPoint [constr] X=0 Y=0 Z=0
    g15: LineSegment StartX=0 StartY=0.45 StartZ=0 EndX=0.45 EndY=0 EndZ=0
  constraints (35):
    c: Coincident(g14,g-1)
    c: PointOnObject(g5,g-2)
    c: Horizontal(g1)
    c: Vertical(g2)
    c: Horizontal(g3)
    c: DistanceX(g5,g8) = 2
    c: DistanceY(g11,g8) = 2
    c: PointOnObject(g5,g0)
    c: PointOnObject(g5,g1)
    c: Tangent(g0,g4) = 1.5708
    c: Tangent(g1,g4) = 1.5708
    c: Coincident(g6,g0)
    c: Coincident(g6,g1)
    c: PointOnObject(g8,g2)
    c: PointOnObject(g8,g1)
    c: Tangent(g2,g7) = 1.5708
    c: Tangent(g1,g7) = 1.5708
    c: Coincident(g9,g2)
    c: Coincident(g9,g1)
    c: PointOnObject(g11,g2)
    c: PointOnObject(g11,g3)
    c: Tangent(g2,g10) = 1.5708
    c: Tangent(g3,g10) = 1.5708
    c: Coincident(g12,g2)
    c: Coincident(g12,g3)
    c: PointOnObject(g14,g0)
    c: PointOnObject(g14,g3)
    c: Tangent(g0,g13) = 1.5708
    c: Tangent(g3,g13) = 1.5708
    c: Coincident(g15,g0)
    c: Coincident(g15,g3)
    c: Equal(g6,g9)
    c: Equal(g9,g12)
    c: Equal(g12,g15)
    c: DistanceX(g14,g3) = 0.45
FEATURE [Sketcher::SketchObject] Sketch022  label="fori per M3x5(OD)x6(L)"
  ArcFitTolerance = 1e-06
  AttachmentSupport = -> [XZ_Plane]
  ExternalGeometry = -> [Sketch016]
  FullyConstrained = true
  MakeInternals = false
  MapMode = 5
  Placement = pos=(0,0,0) rot=(1,0,0;1.5708rad)
  sketch-geometry (7):
    g0: Circle CenterX=-5.6 CenterY=34.8 CenterZ=0 NormalX=0 NormalY=0 NormalZ=1 AngleXU=0 Radius=2.5
    g1: Circle CenterX=-5.6 CenterY=7.6 CenterZ=0 NormalX=0 NormalY=0 NormalZ=1 AngleXU=0 Radius=2.5
    g2: Circle CenterX=-78.51 CenterY=34.8 CenterZ=0 NormalX=0 NormalY=0 NormalZ=1 AngleXU=0 Radius=2.5
    g3: Circle CenterX=-78.51 CenterY=7.6 CenterZ=0 NormalX=0 NormalY=0 NormalZ=1 AngleXU=0 Radius=2.5
    g4: Circle CenterX=-184.08 CenterY=34.8 CenterZ=0 NormalX=0 NormalY=0 NormalZ=1 AngleXU=0 Radius=2.5
    g5: Circle CenterX=-179.305 CenterY=-76.8316 CenterZ=0 NormalX=0 NormalY=0 NormalZ=1 AngleXU=0 Radius=2.5
    g6: Circle CenterX=-213.443 CenterY=-76.8316 CenterZ=0 NormalX=0 NormalY=0 NormalZ=1 AngleXU=0 Radius=2.5
  constraints (14):
    c: Diameter(g0) = 5
    c: Diameter(g1) = 5
    c: Diameter(g2) = 5
    c: Diameter(g3) = 5
    c: Diameter(g4) = 5
    c: Diameter(g5) = 5
    c: Diameter(g6) = 5
    c: Coincident(g0,g-8)
    c: Coincident(g1,g-9)
    c: Coincident(g2,g-6)
    c: Coincident(g3,g-7)
    c: Coincident(g4,g-5)
    c: Coincident(g5,g-4)
    c: Coincident(g6,g-3)
FEATURE [Part::Extrusion] Extrude018  label="Extrude fori M3x5x6 - dx"
  Base = -> Sketch022
  Dir = (0,-1,2e-16)
  DirMode = 2
  FaceMakerClass = Part::FaceMakerBullseye
  FaceMakerMode = 3
  LengthFwd = 6.2
  LengthRev = 0
  Placement = pos=(0,-9.5,0) rot=(0,0,1;0rad)
  Solid = true
  Symmetric = true
FEATURE [Part::Extrusion] Extrude019  label="Extrude fori M3x5x6 - sx"
  Base = -> Sketch022
  Dir = (0,-1,2e-16)
  DirMode = 2
  FaceMakerClass = Part::FaceMakerBullseye
  FaceMakerMode = 3
  LengthFwd = 6.2
  LengthRev = 0
  Placement = pos=(0,9.5,0) rot=(0,0,1;0rad)
  Solid = true
  Symmetric = true
FEATURE [Sketcher::SketchObject] Sketch023  label="foro anteriore M3x5x6"
  ArcFitTolerance = 1e-06
  AttachmentSupport = -> [YZ_Plane]
  FullyConstrained = true
  MakeInternals = false
  MapMode = 5
  Placement = pos=(0,0,0) rot=(0.57735,0.57735,0.57735;2.0944rad)
  sketch-geometry (2):
    g0: LineSegment [constr] StartX=0 StartY=0 StartZ=0 EndX=0 EndY=38.6 EndZ=0
    g1: Circle CenterX=0 CenterY=38.6 CenterZ=0 NormalX=0 NormalY=0 NormalZ=1 AngleXU=0 Radius=2.5
  constraints (5):
    c: Coincident(g0,g-1)
    c: PointOnObject(g0,g-2)
    c: DistanceY(g0,g0) = 38.6
    c: Diameter(g1) = 5
    c: Coincident(g1,g0)
FEATURE [Part::Extrusion] Extrude020  label="Extrude foro anteriore M3x5x6"
  Base = -> Sketch023
  Dir = (1,0,0)
  DirMode = 2
  FaceMakerClass = Part::FaceMakerBullseye
  FaceMakerMode = 3
  LengthFwd = -6.2
  LengthRev = 0
  Solid = true
  Symmetric = false
FEATURE [Sketcher::SketchObject] Sketch024  label="fori per viti frontale"
  ArcFitTolerance = 1e-06
  AttachmentSupport = -> [YZ_Plane]
  FullyConstrained = true
  MakeInternals = false
  MapMode = 5
  Placement = pos=(0,0,0) rot=(0.57735,0.57735,0.57735;2.0944rad)
  sketch-geometry (9):
    g0: LineSegment [constr] StartX=-10.3 StartY=30.721 StartZ=0 EndX=10.3 EndY=30.721 EndZ=0
    g1: LineSegment [constr] StartX=10.3 StartY=30.721 StartZ=0 EndX=10.3 EndY=10.121 EndZ=0
    g2: LineSegment [constr] StartX=10.3 StartY=10.121 StartZ=0 EndX=-10.3 EndY=10.121 EndZ=0
    g3: LineSegment [constr] StartX=-10.3 StartY=10.121 StartZ=0 EndX=-10.3 EndY=30.721 EndZ=0
    g4: LineSegment [constr] StartX=0 StartY=0 StartZ=0 EndX=0 EndY=10.121 EndZ=0
    g5: Circle CenterX=-10.3 CenterY=30.721 CenterZ=0 NormalX=0 NormalY=0 NormalZ=1 AngleXU=0 Radius=2
    g6: Circle CenterX=10.3 CenterY=30.721 CenterZ=0 NormalX=0 NormalY=0 NormalZ=1 AngleXU=0 Radius=2
    g7: Circle CenterX=-10.3 CenterY=10.121 CenterZ=0 NormalX=0 NormalY=0 NormalZ=1 AngleXU=0 Radius=2
    g8: Circle CenterX=10.3 CenterY=10.121 CenterZ=0 NormalX=0 NormalY=0 NormalZ=1 AngleXU=0 Radius=2
  constraints (22):
    c: Horizontal(g0)
    c: Coincident(g1,g0)
    c: Vertical(g1)
    c: Coincident(g2,g1)
    c: Horizontal(g2)
    c: Coincident(g3,g2)
    c: Coincident(g3,g0)
    c: Vertical(g3)
    c: DistanceX(g0,g0) = 20.6
    c: DistanceY(g3,g3) = 20.6
    c: Coincident(g4,g-1)
    c: PointOnObject(g4,g-2)
    c: DistanceY(g4,g4) = 10.121
    c: Symmetric(g2,g2,g4)
    c: Diameter(g5) = 4
    c: Diameter(g6) = 4
    c: Diameter(g7) = 4
    c: Diameter(g8) = 4
    c: Coincident(g5,g0)
    c: Coincident(g6,g0)
    c: Coincident(g7,g2)
    c: Coincident(g8,g1)
FEATURE [Part::Extrusion] Extrude021  label="Extrude fori per viti frontale"
  Base = -> Sketch024
  Dir = (1,0,0)
  DirMode = 2
  FaceMakerClass = Part::FaceMakerBullseye
  FaceMakerMode = 3
  LengthFwd = -2.4
  LengthRev = 0
  Solid = true
  Symmetric = false
FEATURE [Sketcher::SketchObject] Sketch025  label="foro per filo CAM"
  ArcFitTolerance = 1e-06
  AttachmentSupport = -> [XZ_Plane]
  ExternalGeometry = -> [Sketch]
  FullyConstrained = true
  MakeInternals = false
  MapMode = 5
  Placement = pos=(0,0,0) rot=(1,0,0;1.5708rad)
  sketch-geometry (4):
    g0: LineSegment StartX=-44.6 StartY=41.2 StartZ=0 EndX=-44.6 EndY=36.4 EndZ=0
    g1: LineSegment StartX=-44.6 StartY=36.4 StartZ=0 EndX=-54.6 EndY=36.4 EndZ=0
    g2: LineSegment StartX=-54.6 StartY=36.4 StartZ=0 EndX=-50.4 EndY=41.2 EndZ=0
    g3: LineSegment StartX=-50.4 StartY=41.2 StartZ=0 EndX=-44.6 EndY=41.2 EndZ=0
  constraints (11):
    c: Vertical(g0)
    c: Coincident(g1,g0)
    c: Horizontal(g1)
    c: Coincident(g2,g1)
    c: Coincident(g3,g2)
    c: Coincident(g3,g0)
    c: Horizontal(g3)
    c: Coincident(g0,g-3)
    c: DistanceY(g0,g-4) = 0
    c: DistanceX(g3,g3) = 5.8
    c: DistanceX(g1,g1) = 10
FEATURE [Part::Extrusion] Extrude022  label="Extrude foro per filo CAM dx"
  Base = -> Sketch025
  Dir = (0,-1,2e-16)
  DirMode = 2
  FaceMakerClass = Part::FaceMakerBullseye
  FaceMakerMode = 3
  LengthFwd = 4.9
  LengthRev = 0
  Placement = pos=(0,6.95,0) rot=(0,0,1;0rad)
  Solid = true
  Symmetric = true
FEATURE [Part::Extrusion] Extrude023  label="Extrude foro per filo CAM sx"
  Base = -> Sketch025
  Dir = (0,-1,2e-16)
  DirMode = 2
  FaceMakerClass = Part::FaceMakerBullseye
  FaceMakerMode = 3
  LengthFwd = 4.9
  LengthRev = 0
  Placement = pos=(0,-6.95,0) rot=(0,0,1;0rad)
  Solid = true
  Symmetric = true
FEATURE [Sketcher::SketchObject] Sketch026  label="foro sotto anteriore M3x5x6"
  ArcFitTolerance = 1e-06
  AttachmentSupport = -> [XY_Plane]
  FullyConstrained = true
  MakeInternals = false
  MapMode = 5
  sketch-geometry (2):
    g0: LineSegment [constr] StartX=0 StartY=0 StartZ=0 EndX=-16.5 EndY=0 EndZ=0
    g1: Circle CenterX=-16.5 CenterY=0 CenterZ=0 NormalX=0 NormalY=0 NormalZ=1 AngleXU=0 Radius=2.5
  constraints (5):
    c: Distance(g0) = 16.5
    c: Coincident(g0,g-1)
    c: PointOnObject(g0,g-1)
    c: Diameter(g1) = 5
    c: Coincident(g0,g1)
FEATURE [Sketcher::SketchObject] Sketch027  label="foro sotto posteriore M3x5x6"
  ArcFitTolerance = 1e-06
  AttachmentSupport = -> [XY_Plane]
  ExternalGeometry = -> [Sketch]
  FullyConstrained = true
  MakeInternals = false
  MapMode = 5
  sketch-geometry (2):
    g0: LineSegment [constr] StartX=-82.8 StartY=2e-16 StartZ=0 EndX=-71.3 EndY=2e-16 EndZ=0
    g1: Circle CenterX=-71.3 CenterY=2e-16 CenterZ=0 NormalX=0 NormalY=0 NormalZ=1 AngleXU=0 Radius=2.5
  constraints (5):
    c: Distance(g0) = 11.5
    c: Coincident(g0,g-3)
    c: PointOnObject(g0,g-3)
    c: Diameter(g1) = 5
    c: Coincident(g1,g0)
FEATURE [Sketcher::SketchObject] Sketch029  label="fori sotto impugnatura"
  ArcFitTolerance = 1e-06
  AttachmentSupport = -> [XY_Plane]
  ExternalGeometry = -> [Sketch]
  FullyConstrained = true
  MakeInternals = false
  MapMode = 5
  sketch-geometry (15):
    g0: LineSegment [constr] StartX=-175.232 StartY=-1.83e-14 StartZ=0 EndX=-191.232 EndY=0 EndZ=0
    g1: Circle CenterX=-191.232 CenterY=0 CenterZ=0 NormalX=0 NormalY=0 NormalZ=1 AngleXU=0 Radius=3.95
    g2: LineSegment [constr] StartX=-175.232 StartY=-1.83e-14 StartZ=0 EndX=-204.275 EndY=0 EndZ=0
    g3: LineSegment StartX=-204.275 StartY=3.525 StartZ=0 EndX=-204.275 EndY=-3.525 EndZ=0
    g4: LineSegment StartX=-205.4 StartY=-4.65 StartZ=0 EndX=-206.65 EndY=-4.65 EndZ=0
    g5: LineSegment StartX=-207.775 StartY=-3.525 StartZ=0 EndX=-207.775 EndY=3.525 EndZ=0
    g6: LineSegment StartX=-206.65 StartY=4.65 StartZ=0 EndX=-205.4 EndY=4.65 EndZ=0
    g7: ArcOfCircle CenterX=-206.65 CenterY=3.525 CenterZ=0 NormalX=0 NormalY=0 NormalZ=1 AngleXU=0 Radius=1.125 StartAngle=1.5708 EndAngle=3.14159
    g8: GeomPoint [constr] X=-207.775 Y=4.65 Z=0
    g9: ArcOfCircle CenterX=-205.4 CenterY=3.525 CenterZ=0 NormalX=0 NormalY=0 NormalZ=1 AngleXU=0 Radius=1.125 StartAngle=0 EndAngle=1.5708
    g10: GeomPoint [constr] X=-204.275 Y=4.65 Z=0
    g11: ArcOfCircle CenterX=-205.4 CenterY=-3.525 CenterZ=0 NormalX=0 NormalY=0 NormalZ=1 AngleXU=0 Radius=1.125 StartAngle=4.71239 EndAngle=6.28319
    g12: GeomPoint [constr] X=-204.275 Y=-4.65 Z=0
    g13: ArcOfCircle CenterX=-206.65 CenterY=-3.525 CenterZ=0 NormalX=0 NormalY=0 NormalZ=1 AngleXU=0 Radius=1.125 StartAngle=3.14159 EndAngle=4.71239
    g14: GeomPoint [constr] X=-207.775 Y=-4.65 Z=0
  constraints (35):
    c: Distance(g0) = 16
    c: Coincident(g0,g-3)
    c: PointOnObject(g0,g-1)
    c: Diameter(g1) = 7.9
    c: Coincident(g1,g0)
    c: Coincident(g2,g0)
    c: PointOnObject(g2,g-1)
    c: Vertical(g3)
    c: Horizontal(g4)
    c: Vertical(g5)
    c: Horizontal(g6)
    c: DistanceY(g12,g10) = 9.3
    c: DistanceX(g8,g10) = 3.5
    c: Symmetric(g10,g12,g2)
    c: PointOnObject(g8,g5)
    c: PointOnObject(g8,g6)
    c: Tangent(g5,g7) = 1.5708
    c: Tangent(g6,g7) = 1.5708
    c: PointOnObject(g10,g3)
    c: PointOnObject(g10,g6)
    c: Tangent(g3,g9) = 1.5708
    c: Tangent(g6,g9) = 1.5708
    c: PointOnObject(g12,g3)
    c: PointOnObject(g12,g4)
    c: Tangent(g3,g11) = 1.5708
    c: Tangent(g4,g11) = 1.5708
    c: PointOnObject(g14,g4)
    c: PointOnObject(g14,g5)
    c: Tangent(g4,g13) = 1.5708
    c: Tangent(g5,g13) = 1.5708
    c: Equal(g7,g9)
    c: Equal(g9,g11)
    c: Equal(g11,g13)
    c: DistanceX(g6,g6) = 1.25
    c: DistanceX(g-5,g5) = 6.8
FEATURE [Sketcher::SketchObject] Sketch030  label="fori superiori per solenoide e oled"
  ArcFitTolerance = 1e-06
  AttachmentSupport = -> [XY_Plane]
  ExternalGeometry = -> [Sketch]
  FullyConstrained = true
  MakeInternals = false
  MapMode = 5
  sketch-geometry (33):
    g0: LineSegment [constr] StartX=-181.6 StartY=1.12e-14 StartZ=0 EndX=-169.91 EndY=0 EndZ=0
    g1: LineSegment [constr] StartX=-169.91 StartY=0 StartZ=0 EndX=-169.91 EndY=-2.6 EndZ=0
    g2: LineSegment [constr] StartX=-169.91 StartY=0 StartZ=0 EndX=-169.91 EndY=2.6 EndZ=0
    g3: LineSegment StartX=-169.91 StartY=4.975 StartZ=0 EndX=-169.91 EndY=8.225 EndZ=0
    g4: LineSegment StartX=-167.535 StartY=10.6 StartZ=0 EndX=-167.285 EndY=10.6 EndZ=0
    g5: LineSegment StartX=-164.91 StartY=8.225 StartZ=0 EndX=-164.91 EndY=4.975 EndZ=0
    g6: LineSegment StartX=-167.285 StartY=2.6 StartZ=0 EndX=-167.535 EndY=2.6 EndZ=0
    g7: LineSegment StartX=-169.91 StartY=-4.975 StartZ=0 EndX=-169.91 EndY=-8.225 EndZ=0
    g8: LineSegment StartX=-167.535 StartY=-10.6 StartZ=0 EndX=-167.285 EndY=-10.6 EndZ=0
    g9: LineSegment StartX=-164.91 StartY=-8.225 StartZ=0 EndX=-164.91 EndY=-4.975 EndZ=0
    g10: LineSegment StartX=-167.285 StartY=-2.6 StartZ=0 EndX=-167.535 EndY=-2.6 EndZ=0
    g11: ArcOfCircle CenterX=-167.535 CenterY=8.225 CenterZ=0 NormalX=0 NormalY=0 NormalZ=1 AngleXU=0 Radius=2.375 StartAngle=1.5708 EndAngle=3.14159
    g12: GeomPoint [constr] X=-169.91 Y=10.6 Z=0
    g13: ArcOfCircle CenterX=-167.285 CenterY=8.225 CenterZ=0 NormalX=0 NormalY=0 NormalZ=1 AngleXU=0 Radius=2.375 StartAngle=0 EndAngle=1.5708
    g14: GeomPoint [constr] X=-164.91 Y=10.6 Z=0
    g15: ArcOfCircle CenterX=-167.285 CenterY=4.975 CenterZ=0 NormalX=0 NormalY=0 NormalZ=1 AngleXU=0 Radius=2.375 StartAngle=4.71239 EndAngle=6.28319
    g16: GeomPoint [constr] X=-164.91 Y=2.6 Z=0
    g17: ArcOfCircle CenterX=-167.535 CenterY=4.975 CenterZ=0 NormalX=0 NormalY=0 NormalZ=1 AngleXU=0 Radius=2.375 StartAngle=3.14159 EndAngle=4.71239
    g18: GeomPoint [constr] X=-169.91 Y=2.6 Z=0
    g19: ArcOfCircle CenterX=-167.535 CenterY=-4.975 CenterZ=0 NormalX=0 NormalY=0 NormalZ=1 AngleXU=0 Radius=2.375 StartAngle=1.5708 EndAngle=3.14159
    g20: GeomPoint [constr] X=-169.91 Y=-2.6 Z=0
    g21: ArcOfCircle CenterX=-167.285 CenterY=-4.975 CenterZ=0 NormalX=0 NormalY=0 NormalZ=1 AngleXU=0 Radius=2.375 StartAngle=0 EndAngle=1.5708
    g22: GeomPoint [constr] X=-164.91 Y=-2.6 Z=0
    g23: ArcOfCircle CenterX=-167.285 CenterY=-8.225 CenterZ=0 NormalX=0 NormalY=0 NormalZ=1 AngleXU=0 Radius=2.375 StartAngle=4.71239 EndAngle=6.28319
    g24: GeomPoint [constr] X=-164.91 Y=-10.6 Z=0
    g25: ArcOfCircle CenterX=-167.535 CenterY=-8.225 CenterZ=0 NormalX=0 NormalY=0 NormalZ=1 AngleXU=0 Radius=2.375 StartAngle=3.14159 EndAngle=4.71239
    g26: GeomPoint [constr] X=-169.91 Y=-10.6 Z=0
    g27: LineSegment [constr] StartX=-181.6 StartY=1.12e-14 StartZ=0 EndX=-152.209 EndY=0 EndZ=0
    g28: LineSegment [constr] StartX=-181.6 StartY=1.12e-14 StartZ=0 EndX=-130.41 EndY=0 EndZ=0
    g29: LineSegment [constr] StartX=-152.209 StartY=0 StartZ=0 EndX=-152.209 EndY=6.95 EndZ=0
    g30: LineSegment [constr] StartX=-130.41 StartY=0 StartZ=0 EndX=-130.41 EndY=-6.95 EndZ=0
    g31: Circle CenterX=-152.209 CenterY=6.95 CenterZ=0 NormalX=0 NormalY=0 NormalZ=1 AngleXU=0 Radius=2.1
    g32: Circle CenterX=-130.41 CenterY=-6.95 CenterZ=0 NormalX=0 NormalY=0 NormalZ=1 AngleXU=0 Radius=2.1
  constraints (79):
    c: Distance(g0) = 11.69
    c: PointOnObject(g0,g-1)
    c: Coincident(g-4,g0)
    c: Distance(g1) = 2.6
    c: Coincident(g1,g0)
    c: Vertical(g1)
    c: Distance(g2) = 2.6
    c: Coincident(g2,g0)
    c: Vertical(g2)
    c: Distance(g18,g12) = 8
    c: Coincident(g18,g2)
    c: Vertical(g3)
    c: Distance(g14,g12) = 5
    c: Horizontal(g4)
    c: Distance(g16,g14) = 8
    c: Vertical(g5)
    c: Distance(g26,g20) = 8
    c: Coincident(g20,g1)
    c: Vertical(g7)
    c: Distance(g26,g24) = 5
    c: Horizontal(g8)
    c: Distance(g24,g22) = 8
    c: Vertical(g9)
    c: PointOnObject(g12,g3)
    c: PointOnObject(g12,g4)
    c: Tangent(g3,g11) = 1.5708
    c: Tangent(g4,g11) = 1.5708
    c: PointOnObject(g14,g5)
    c: PointOnObject(g14,g4)
    c: Tangent(g5,g13) = 1.5708
    c: Tangent(g4,g13) = 1.5708
    c: PointOnObject(g16,g5)
    c: PointOnObject(g16,g6)
    c: Tangent(g5,g15) = 1.5708
    c: Tangent(g6,g15) = 1.5708
    c: PointOnObject(g18,g3)
    c: PointOnObject(g18,g6)
    c: Tangent(g3,g17) = 1.5708
    c: Tangent(g6,g17) = 1.5708
    c: Equal(g11,g13)
    c: Equal(g13,g15)
    c: Equal(g15,g17)
    c: DistanceX(g4,g4) = 0.25
    c: PointOnObject(g20,g7)
    c: PointOnObject(g20,g10)
    c: Tangent(g7,g19) = -1.5708
    c: Tangent(g10,g19) = -1.5708
    c: PointOnObject(g22,g9)
    c: PointOnObject(g22,g10)
    c: Tangent(g9,g21) = -1.5708
    c: Tangent(g10,g21) = -1.5708
    c: PointOnObject(g24,g9)
    c: PointOnObject(g24,g8)
    c: Tangent(g9,g23) = -1.5708
    c: Tangent(g8,g23) = -1.5708
    c: PointOnObject(g26,g8)
    c: PointOnObject(g26,g7)
    c: Tangent(g8,g25) = -1.5708
    c: Tangent(g7,g25) = -1.5708
    c: Equal(g19,g21)
    c: Equal(g21,g23)
    c: Equal(g23,g25)
    c: DistanceX(g10,g10) = 0.25
    c: Distance(g27) = 29.391
    c: Coincident(g27,g0)
    c: PointOnObject(g27,g-1)
    c: Distance(g28) = 51.19
    c: Coincident(g28,g0)
    c: PointOnObject(g28,g-1)
    c: Distance(g29) = 6.95
    c: Coincident(g29,g27)
    c: Vertical(g29)
    c: Distance(g30) = 6.95
    c: Coincident(g30,g28)
    c: Vertical(g30)
    c: Diameter(g31) = 4.2
    c: Diameter(g32) = 4.2
    c: Coincident(g32,g30)
    c: Coincident(g31,g29)
FEATURE [Sketcher::SketchObject] Sketch031  label="fori inferiori switch pompa"
  ArcFitTolerance = 1e-06
  AttachmentSupport = -> [XY_Plane]
  ExternalGeometry = -> [Sketch]
  FullyConstrained = true
  MakeInternals = false
  MapMode = 5
  sketch-geometry (4):
    g0: LineSegment [constr] StartX=-57.2 StartY=1.9e-15 StartZ=0 EndX=-62.45 EndY=1.9e-15 EndZ=0
    g1: LineSegment [constr] StartX=-62.45 StartY=3.25 StartZ=0 EndX=-62.45 EndY=-3.25 EndZ=0
    g2: Circle CenterX=-62.45 CenterY=3.25 CenterZ=0 NormalX=0 NormalY=0 NormalZ=1 AngleXU=0 Radius=1.6
    g3: Circle CenterX=-62.45 CenterY=-3.25 CenterZ=0 NormalX=0 NormalY=0 NormalZ=1 AngleXU=0 Radius=1.6
  constraints (10):
    c: Distance(g0) = 5.25
    c: Coincident(g0,g-3)
    c: PointOnObject(g0,g-3)
    c: Vertical(g1)
    c: DistanceY(g1,g1) = 6.5
    c: Symmetric(g1,g1,g0)
    c: Diameter(g2) = 3.2
    c: Diameter(g3) = 3.2
    c: Coincident(g2,g1)
    c: Coincident(g3,g1)
FEATURE [Sketcher::SketchObject] Sketch032  label="spazio per PILA 18650"
  ArcFitTolerance = 1e-06
  AttachmentSupport = -> [XY_Plane]
  ExternalGeometry = -> [Sketch]
  FullyConstrained = true
  MakeInternals = false
  MapMode = 5
  sketch-geometry (2):
    g0: LineSegment [constr] StartX=-178.142 StartY=-1.74e-14 StartZ=0 EndX=-191.142 EndY=-1.83e-14 EndZ=0
    g1: Circle CenterX=-191.142 CenterY=-1.83e-14 CenterZ=0 NormalX=0 NormalY=0 NormalZ=1 AngleXU=0 Radius=10.9
  constraints (5):
    c: Distance(g0) = 13
    c: Coincident(g0,g-3)
    c: PointOnObject(g0,g-4)
    c: Diameter(g1) = 21.8
    c: Coincident(g1,g0)
FEATURE [Part::Extrusion] Extrude030  label="Extrude spazio per PILA 18650"
  Base = -> Sketch032
  Dir = (0,0,1)
  DirLink = -> Sketch [Edge45]
  DirMode = 2
  FaceMakerClass = Part::FaceMakerBullseye
  FaceMakerMode = 3
  LengthFwd = 76
  LengthRev = 0
  Placement = pos=(6,0,-70) rot=(0,0,1;0rad)
  Solid = true
  Symmetric = false
FEATURE [Sketcher::SketchObject] Sketch033  label="fermo per scheda micro"
  ArcFitTolerance = 1e-06
  AttachmentSupport = -> [XZ_Plane]
  ExternalGeometry = -> [Sketch]
  FullyConstrained = true
  MakeInternals = false
  MapMode = 5
  Placement = pos=(0,0,0) rot=(1,0,0;1.5708rad)
  sketch-geometry (12):
    g0: LineSegment StartX=-11.6 StartY=6 StartZ=0 EndX=-4 EndY=6 EndZ=0
    g1: LineSegment StartX=-4 StartY=6 StartZ=0 EndX=-4 EndY=36.4 EndZ=0
    g2: LineSegment StartX=-4 StartY=36.4 StartZ=0 EndX=-11.6 EndY=36.4 EndZ=0
    g3: LineSegment StartX=-11.6 StartY=36.4 StartZ=0 EndX=-11.6 EndY=6 EndZ=0
    g4: LineSegment StartX=-80.11 StartY=11.6 StartZ=0 EndX=-70.51 EndY=11.6 EndZ=0
    g5: LineSegment StartX=-70.51 StartY=11.6 StartZ=0 EndX=-70.51 EndY=6 EndZ=0
    g6: LineSegment StartX=-70.51 StartY=6 StartZ=0 EndX=-80.11 EndY=6 EndZ=0
    g7: LineSegment StartX=-80.11 StartY=6 StartZ=0 EndX=-80.11 EndY=11.6 EndZ=0
    g8: LineSegment StartX=-78.51 StartY=36.4 StartZ=0 EndX=-70.51 EndY=36.4 EndZ=0
    g9: LineSegment StartX=-70.51 StartY=36.4 StartZ=0 EndX=-70.51 EndY=30.8 EndZ=0
    g10: LineSegment StartX=-70.51 StartY=30.8 StartZ=0 EndX=-78.51 EndY=30.8 EndZ=0
    g11: LineSegment StartX=-78.51 StartY=30.8 StartZ=0 EndX=-78.51 EndY=36.4 EndZ=0
  constraints (33):
    c: Horizontal(g0)
    c: Coincident(g1,g0)
    c: Coincident(g2,g1)
    c: Horizontal(g2)
    c: Coincident(g3,g2)
    c: Coincident(g3,g0)
    c: Vertical(g3)
    c: DistanceX(g2,g2) = 7.6
    c: Coincident(g1,g-3)
    c: Coincident(g0,g-3)
    c: Horizontal(g4)
    c: Coincident(g5,g4)
    c: Vertical(g5)
    c: Coincident(g6,g5)
    c: Horizontal(g6)
    c: Coincident(g7,g6)
    c: Coincident(g7,g4)
    c: Vertical(g7)
    c: DistanceY(g5,g5) = 5.6
    c: DistanceX(g4,g4) = 9.6
    c: Coincident(g9,g8)
    c: Vertical(g9)
    c: Coincident(g10,g9)
    c: Horizontal(g10)
    c: Coincident(g11,g10)
    c: Coincident(g11,g8)
    c: Vertical(g11)
    c: DistanceY(g9,g9) = 5.6
    c: DistanceX(g10,g10) = 8
    c: Coincident(g4,g-4)
    c: DistanceX(g4,g10) = 1.6
    c: Horizontal(g8)
    c: DistanceY(g8,g1) = 0
FEATURE [Sketcher::SketchObject] Sketch034  label="buchi guida rail"
  ArcFitTolerance = 1e-06
  AttachmentSupport = -> [XY_Plane]
  ExternalGeometry = -> [Sketch]
  FullyConstrained = true
  MakeInternals = false
  MapMode = 5
  sketch-geometry (6):
    g0: LineSegment [constr] StartX=-100.8 StartY=9.1e-15 StartZ=0 EndX=-93.3 EndY=0 EndZ=0
    g1: LineSegment [constr] StartX=-93.3 StartY=0 StartZ=0 EndX=-73.3 EndY=0 EndZ=0
    g2: LineSegment [constr] StartX=-73.3 StartY=0 StartZ=0 EndX=-53.3 EndY=0 EndZ=0
    g3: Circle CenterX=-93.3 CenterY=0 CenterZ=0 NormalX=0 NormalY=0 NormalZ=1 AngleXU=0 Radius=2.5
    g4: Circle CenterX=-73.3 CenterY=0 CenterZ=0 NormalX=0 NormalY=0 NormalZ=1 AngleXU=0 Radius=2.5
    g5: Circle CenterX=-53.3 CenterY=0 CenterZ=0 NormalX=0 NormalY=0 NormalZ=1 AngleXU=0 Radius=2.5
  constraints (15):
    c: Distance(g0) = 7.5
    c: Coincident(g0,g-3)
    c: PointOnObject(g0,g-1)
    c: Distance(g1) = 20
    c: Coincident(g1,g0)
    c: PointOnObject(g1,g-1)
    c: Distance(g2) = 20
    c: Coincident(g2,g1)
    c: PointOnObject(g2,g-1)
    c: Diameter(g3) = 5
    c: Diameter(g4) = 5
    c: Diameter(g5) = 5
    c: Coincident(g3,g0)
    c: Coincident(g4,g1)
    c: Coincident(g5,g2)
FEATURE [Part::Extrusion] Extrude032  label="Extrude buchi guida rail"
  Base = -> Sketch034
  Dir = (0,0,1)
  DirMode = 2
  FaceMakerClass = Part::FaceMakerBullseye
  FaceMakerMode = 3
  LengthFwd = -6.2
  LengthRev = 0
  Placement = pos=(0,0,43.2) rot=(0,0,1;0rad)
  Solid = true
  Symmetric = false
FEATURE [Part::Extrusion] Extrude033  label="Extrude fori superiori per solenoide e oled001"
  Base = -> Sketch030
  Dir = (0,0,1)
  DirMode = 2
  FaceMakerClass = Part::FaceMakerBullseye
  FaceMakerMode = 3
  LengthFwd = -4.8
  LengthRev = 0
  Placement = pos=(0,0,41.2) rot=(0,0,1;0rad)
  Solid = true
  Symmetric = false
FEATURE [Part::Extrusion] Extrude034  label="Extrude fori sotto impugnatura001"
  Base = -> Sketch029
  Dir = (0,0,1)
  DirMode = 2
  FaceMakerClass = Part::FaceMakerBullseye
  FaceMakerMode = 3
  LengthFwd = 5
  LengthRev = 0
  Placement = pos=(0,0,-83) rot=(0,0,1;0rad)
  Solid = true
  Symmetric = false
FEATURE [Part::Extrusion] Extrude035  label="Extrude fori inferiori switch pompa001"
  Base = -> Sketch031
  Dir = (0,0,1)
  DirMode = 2
  FaceMakerClass = Part::FaceMakerBullseye
  FaceMakerMode = 3
  LengthFwd = 4
  LengthRev = 0
  Placement = pos=(0,0,-1.7) rot=(0,0,1;0rad)
  Solid = true
  Symmetric = false
FEATURE [Part::Extrusion] Extrude036  label="Extrude foro sotto posteriore M3x5x007"
  Base = -> Sketch027
  Dir = (0,0,1)
  DirMode = 2
  FaceMakerClass = Part::FaceMakerBullseye
  FaceMakerMode = 3
  LengthFwd = 6.2
  LengthRev = 0
  Placement = pos=(0,0,-9.6) rot=(0,0,1;0rad)
  Solid = true
  Symmetric = false
FEATURE [Part::Extrusion] Extrude037  label="Extrude foro sotto anteriore M3x5x007"
  Base = -> Sketch026
  Dir = (0,0,1)
  DirMode = 2
  FaceMakerClass = Part::FaceMakerBullseye
  FaceMakerMode = 3
  LengthFwd = 6.2
  LengthRev = 0
  Solid = true
  Symmetric = false
FEATURE [Sketcher::SketchObject] Sketch035  label="foro per fissaggio micro"
  ArcFitTolerance = 1e-06
  AttachmentSupport = -> [XZ_Plane]
  ExternalGeometry = -> [Sketch,Sketch033]
  FullyConstrained = true
  MakeInternals = false
  MapMode = 5
  Placement = pos=(0,0,0) rot=(1,0,0;1.5708rad)
  sketch-geometry (3):
    g0: Circle CenterX=-7.8 CenterY=21.2 CenterZ=0 NormalX=0 NormalY=0 NormalZ=1 AngleXU=0 Radius=1.6
    g1: GeomPoint [constr] X=-4 Y=21.2 Z=0
    g2: LineSegment [constr] StartX=-4 StartY=21.2 StartZ=0 EndX=-11.6 EndY=21.2 EndZ=0
  constraints (6):
    c: Diameter(g0) = 3.2
    c: Symmetric(g-3,g-3,g1)
    c: Coincident(g2,g1)
    c: Horizontal(g2)
    c: DistanceX(g-4,g2) = 0
    c: Symmetric(g2,g1,g0)
FEATURE [Part::Extrusion] Extrude038  label="Extrude foro per fissaggio micro"
  Base = -> Sketch035
  Dir = (0,-1,2e-16)
  DirMode = 2
  FaceMakerClass = Part::FaceMakerBullseye
  FaceMakerMode = 3
  LengthFwd = 3
  LengthRev = 0
  Placement = pos=(0,8.6,0) rot=(0,0,1;0rad)
  Solid = true
  Symmetric = false
FEATURE [Sketcher::SketchObject] Sketch036  label="supporto per alimentatore"
  ArcFitTolerance = 1e-06
  AttachmentSupport = -> [XZ_Plane]
  ExternalGeometry = -> [Sketch,Sketch016,Sketch022]
  FullyConstrained = true
  MakeInternals = false
  MapMode = 5
  Placement = pos=(0,0,0) rot=(1,0,0;1.5708rad)
  sketch-geometry (5):
    g0: LineSegment StartX=-211.843 StartY=-50.0944 StartZ=0 EndX=-211.843 EndY=-80.4316 EndZ=0
    g1: LineSegment StartX=-211.843 StartY=-50.0944 StartZ=0 EndX=-207.775 EndY=-41.3701 EndZ=0
    g2: LineSegment [constr] StartX=-209.443 StartY=-50.0944 StartZ=0 EndX=-209.443 EndY=-80.4316 EndZ=0
    g3: LineSegment StartX=-207.775 StartY=-41.3701 StartZ=0 EndX=-207.775 EndY=-80.4316 EndZ=0
    g4: LineSegment StartX=-211.843 StartY=-80.4316 StartZ=0 EndX=-207.775 EndY=-80.4316 EndZ=0
  constraints (15):
    c: Vertical(g0)
    c: Coincident(g1,g0)
    c: Vertical(g2)
    c: Tangent(g2,g-5)
    c: Coincident(g3,g1)
    c: Vertical(g3)
    c: DistanceY(g-3,g3) = -2
    c: Tangent(g1,g-8)
    c: DistanceY(g-3,g0) = -2
    c: Coincident(g4,g0)
    c: Coincident(g4,g3)
    c: Tangent(g0,g-6)
    c: DistanceY(g-3,g2) = -2
    c: DistanceY(g2,g0) = 0
    c: DistanceX(g-3,g3) = 6.8
FEATURE [Part::Extrusion] Extrude039  label="Extrude039 supporto alimentatore"
  Base = -> Sketch036
  Dir = (0,-1,2e-16)
  DirMode = 2
  FaceMakerClass = Part::FaceMakerBullseye
  FaceMakerMode = 3
  LengthFwd = 25.2
  LengthRev = 0
  Solid = true
  Symmetric = true
FEATURE [Sketcher::SketchObject] Sketch037  label="scavo per alimentatore"
  ArcFitTolerance = 1e-06
  AttachmentSupport = -> [XZ_Plane]
  ExternalGeometry = -> [Sketch036]
  FullyConstrained = true
  MakeInternals = false
  MapMode = 5
  Placement = pos=(0,0,0) rot=(1,0,0;1.5708rad)
  sketch-geometry (4):
    g0: LineSegment StartX=-209.575 StartY=-50.4316 StartZ=0 EndX=-209.575 EndY=-80.4316 EndZ=0
    g1: LineSegment StartX=-209.575 StartY=-50.4316 StartZ=0 EndX=-207.775 EndY=-50.4316 EndZ=0
    g2: LineSegment StartX=-207.775 StartY=-50.4316 StartZ=0 EndX=-207.775 EndY=-80.4316 EndZ=0
    g3: LineSegment StartX=-207.775 StartY=-80.4316 StartZ=0 EndX=-209.575 EndY=-80.4316 EndZ=0
  constraints (11):
    c: Vertical(g0)
    c: Coincident(g1,g0)
    c: Horizontal(g1)
    c: Coincident(g2,g1)
    c: Vertical(g2)
    c: Coincident(g3,g2)
    c: Coincident(g3,g0)
    c: Horizontal(g3)
    c: DistanceX(g1,g1) = 1.8
    c: Coincident(g2,g-3)
    c: DistanceY(g2,g2) = 30
FEATURE [Part::Extrusion] Extrude040  label="Extrude040 scavo alimentatore"
  Base = -> Sketch037
  Dir = (0,-1,2e-16)
  DirMode = 2
  FaceMakerClass = Part::FaceMakerBullseye
  FaceMakerMode = 3
  LengthFwd = 19.5
  LengthRev = 0
  Solid = true
  Symmetric = true
FEATURE [Part::Extrusion] Extrude031  label="Extrude fermo per scheda micro"
  Base = -> Sketch033
  Dir = (0,-1,2e-16)
  DirMode = 2
  FaceMakerClass = Part::FaceMakerBullseye
  FaceMakerMode = 3
  LengthFwd = 3
  LengthRev = 0
  Placement = pos=(0,8.6,0) rot=(0,0,1;0rad)
  Solid = true
  Symmetric = false
FEATURE [Sketcher::SketchObject] Sketch038  label="scavo driver solenoide"
  ArcFitTolerance = 1e-06
  AttachmentSupport = -> [XZ_Plane]
  ExternalGeometry = -> [Sketch,Sketch036]
  FullyConstrained = true
  MakeInternals = false
  MapMode = 5
  Placement = pos=(0,0,0) rot=(1,0,0;1.5708rad)
  sketch-geometry (7):
    g0: LineSegment StartX=-192.222 StartY=-8.0175 StartZ=0 EndX=-194.035 EndY=-7.17226 EndZ=0
    g1: LineSegment StartX=-194.035 StartY=-7.17226 StartZ=0 EndX=-211.362 EndY=-44.3309 EndZ=0
    g2: LineSegment StartX=-192.222 StartY=-8.0175 StartZ=0 EndX=-188.779 EndY=-9.62345 EndZ=0
    g3: LineSegment StartX=-188.779 StartY=-9.62345 StartZ=0 EndX=-205.357 EndY=-45.1761 EndZ=0
    g4: LineSegment StartX=-205.357 StartY=-45.1761 StartZ=0 EndX=-209.55 EndY=-45.1761 EndZ=0
    g5: LineSegment [constr] StartX=-211.362 StartY=-44.3309 StartZ=0 EndX=-209.55 EndY=-45.1761 EndZ=0
    g6: LineSegment StartX=-211.362 StartY=-44.3309 StartZ=0 EndX=-209.55 EndY=-45.1761 EndZ=0
  constraints (20):
    c: Coincident(g1,g0)
    c: Coincident(g3,g2)
    c: Coincident(g4,g3)
    c: Distance(g2) = 3.8
    c: Distance(g1) = 41
    c: Coincident(g5,g1)
    c: Distance(g5) = 2
    c: Perpendicular(g5,g-3)
    c: Parallel(g1,g-3)
    c: Perpendicular(g1,g0)
    c: Distance(g0) = 2
    c: Coincident(g6,g1)
    c: Parallel(g3,g-3)
    c: Perpendicular(g2,g3)
    c: Coincident(g2,g0)
    c: Perpendicular(g-4,g4)
    c: PointOnObject(g5,g-3)
    c: Distance(g-3,g5) = 9.6
    c: Coincident(g4,g5)
    c: Coincident(g6,g4)
FEATURE [Part::Extrusion] Extrude041  label="Extrude scavo driver solenoide"
  Base = -> Sketch038
  Dir = (0,-1,2e-16)
  DirMode = 2
  FaceMakerClass = Part::FaceMakerBullseye
  FaceMakerMode = 3
  LengthFwd = 20.8
  LengthRev = 0
  Solid = true
  Symmetric = true
FEATURE [Sketcher::SketchObject] Sketch039  label="scavo per cavo usb per micro"
  ArcFitTolerance = 1e-06
  AttachmentSupport = -> [XZ_Plane]
  ExternalGeometry = -> [Sketch,Sketch016]
  FullyConstrained = true
  MakeInternals = false
  MapMode = 5
  Placement = pos=(0,0,0) rot=(1,0,0;1.5708rad)
  sketch-geometry (4):
    g0: LineSegment StartX=-82.51 StartY=36.4 StartZ=0 EndX=-74.51 EndY=36.4 EndZ=0
    g1: LineSegment StartX=-74.51 StartY=36.4 StartZ=0 EndX=-74.51 EndY=30.8 EndZ=0
    g2: LineSegment StartX=-74.51 StartY=30.8 StartZ=0 EndX=-82.51 EndY=30.8 EndZ=0
    g3: LineSegment StartX=-82.51 StartY=30.8 StartZ=0 EndX=-82.51 EndY=36.4 EndZ=0
  constraints (11):
    c: Coincident(g1,g0)
    c: Vertical(g1)
    c: Coincident(g2,g1)
    c: Horizontal(g2)
    c: Coincident(g3,g2)
    c: Coincident(g3,g0)
    c: Vertical(g3)
    c: Tangent(g0,g-3)
    c: Tangent(g2,g-4)
    c: Tangent(g3,g-4)
    c: Tangent(g1,g-4)
FEATURE [Part::Extrusion] Extrude042  label="Extrude scavo per cavo usb per micro"
  Base = -> Sketch039
  Dir = (0,-1,2e-16)
  DirMode = 2
  FaceMakerClass = Part::FaceMakerBullseye
  FaceMakerMode = 3
  LengthFwd = 11.2
  LengthRev = 0
  Solid = true
  Symmetric = true
FEATURE [Sketcher::SketchObject] Sketch040  label="scavo saldature alimentatore connettore 5v"
  ArcFitTolerance = 1e-06
  AttachmentSupport = -> [XZ_Plane]
  ExternalGeometry = -> [Sketch037]
  FullyConstrained = true
  MakeInternals = false
  MapMode = 5
  Placement = pos=(0,0,0) rot=(1,0,0;1.5708rad)
  sketch-geometry (4):
    g0: LineSegment StartX=-211.175 StartY=-52.4316 StartZ=0 EndX=-211.175 EndY=-56.4316 EndZ=0
    g1: LineSegment StartX=-211.175 StartY=-52.4316 StartZ=0 EndX=-209.575 EndY=-52.4316 EndZ=0
    g2: LineSegment StartX=-209.575 StartY=-52.4316 StartZ=0 EndX=-209.575 EndY=-56.4316 EndZ=0
    g3: LineSegment StartX=-209.575 StartY=-56.4316 StartZ=0 EndX=-211.175 EndY=-56.4316 EndZ=0
  constraints (11):
    c: Vertical(g0)
    c: Coincident(g1,g0)
    c: Horizontal(g1)
    c: Coincident(g2,g1)
    c: Coincident(g3,g2)
    c: Coincident(g3,g0)
    c: Horizontal(g3)
    c: DistanceX(g1,g1) = 1.6
    c: DistanceY(g2,g2) = 4
    c: Tangent(g2,g-3)
    c: DistanceY(g1,g-3) = 2
FEATURE [Part::Extrusion] Extrude043  label="Extrude scavo saldature alimentatore connettore 5v"
  Base = -> Sketch040
  Dir = (0,-1,2e-16)
  DirMode = 2
  FaceMakerClass = Part::FaceMakerBullseye
  FaceMakerMode = 3
  LengthFwd = 8
  LengthRev = 0
  Solid = true
  Symmetric = true
FEATURE [Sketcher::SketchObject] Sketch041  label="scavo saldature alimentatore connettore 5v verticali"
  ArcFitTolerance = 1e-06
  AttachmentSupport = -> [XZ_Plane]
  ExternalGeometry = -> [Sketch037]
  FullyConstrained = true
  MakeInternals = false
  MapMode = 5
  Placement = pos=(0,0,0) rot=(1,0,0;1.5708rad)
  sketch-geometry (4):
    g0: LineSegment StartX=-211.175 StartY=-53.6316 StartZ=0 EndX=-209.575 EndY=-53.6316 EndZ=0
    g1: LineSegment StartX=-209.575 StartY=-53.6316 StartZ=0 EndX=-209.575 EndY=-76.6316 EndZ=0
    g2: LineSegment StartX=-209.575 StartY=-76.6316 StartZ=0 EndX=-211.175 EndY=-76.6316 EndZ=0
    g3: LineSegment StartX=-211.175 StartY=-76.6316 StartZ=0 EndX=-211.175 EndY=-53.6316 EndZ=0
  constraints (11):
    c: Horizontal(g0)
    c: Coincident(g1,g0)
    c: Coincident(g2,g1)
    c: Horizontal(g2)
    c: Coincident(g3,g2)
    c: Coincident(g3,g0)
    c: Vertical(g3)
    c: DistanceY(g3,g3) = 23
    c: DistanceX(g0,g0) = 1.6
    c: Tangent(g1,g-3)
    c: DistanceY(g0,g-3) = 3.2
FEATURE [Part::Extrusion] Extrude044  label="Extrude scavo saldature alimentatore connettore 5v verticali"
  Base = -> Sketch041
  Dir = (0,-1,2e-16)
  DirMode = 2
  FaceMakerClass = Part::FaceMakerBullseye
  FaceMakerMode = 3
  LengthFwd = 3.2
  LengthRev = 0
  Placement = pos=(0,8.3,0) rot=(0,0,1;0rad)
  Solid = true
  Symmetric = false
FEATURE [Sketcher::SketchObject] Sketch042  label="fermi per driver solenoide e alimentatore"
  ArcFitTolerance = 1e-06
  AttachmentSupport = -> [XZ_Plane]
  ExternalGeometry = -> [Sketch036,Sketch037,Sketch,Sketch038]
  FullyConstrained = true
  MakeInternals = false
  MapMode = 5
  Placement = pos=(0,0,0) rot=(1,0,0;1.5708rad)
  sketch-geometry (27):
    g0: LineSegment StartX=-198.9 StartY=-22.3372 StartZ=0 EndX=-199.83 EndY=-24.331 EndZ=0
    g1: LineSegment StartX=-199.83 StartY=-24.331 StartZ=0 EndX=-197.836 EndY=-25.2608 EndZ=0
    g2: LineSegment StartX=-197.836 StartY=-25.2608 StartZ=0 EndX=-196.906 EndY=-23.2669 EndZ=0
    g3: LineSegment StartX=-196.906 StartY=-23.2669 StartZ=0 EndX=-198.9 EndY=-22.3372 EndZ=0
    g4: LineSegment StartX=-199.674 StartY=-20.2109 StartZ=0 EndX=-201.956 EndY=-25.1049 EndZ=0
    g5: LineSegment StartX=-201.956 StartY=-25.1049 StartZ=0 EndX=-198.512 EndY=-26.7109 EndZ=0
    g6: LineSegment StartX=-196.386 StartY=-25.937 StartZ=0 EndX=-195.456 EndY=-23.9431 EndZ=0
    g7: LineSegment StartX=-196.23 StartY=-21.8168 StartZ=0 EndX=-199.674 EndY=-20.2109 EndZ=0
    g8: LineSegment [constr] StartX=-197.062 StartY=-27.3871 StartZ=0 EndX=-196.386 EndY=-25.937 EndZ=0
    g9: LineSegment [constr] StartX=-197.062 StartY=-27.3871 StartZ=0 EndX=-198.512 EndY=-26.7109 EndZ=0
    g10: ArcOfCircle CenterX=-196.906 CenterY=-23.2669 CenterZ=0 NormalX=0 NormalY=0 NormalZ=1 AngleXU=0 Radius=1.6 StartAngle=5.84685 EndAngle=7.41765
    g11: GeomPoint [constr] X=-194.78 Y=-22.493 Z=0
    g12: ArcOfCircle CenterX=-197.836 CenterY=-25.2608 CenterZ=0 NormalX=0 NormalY=0 NormalZ=1 AngleXU=0 Radius=1.6 StartAngle=4.27606 EndAngle=5.84685
    g13: GeomPoint [constr] X=-197.062 Y=-27.3871 Z=0
    g14: LineSegment StartX=-207.775 StartY=-46.8316 StartZ=0 EndX=-207.775 EndY=-50.8316 EndZ=0
    g15: LineSegment StartX=-207.775 StartY=-46.8316 StartZ=0 EndX=-203.775 EndY=-46.8316 EndZ=0
    g16: LineSegment StartX=-203.775 StartY=-46.8316 StartZ=0 EndX=-203.775 EndY=-50.8316 EndZ=0
    g17: LineSegment StartX=-207.775 StartY=-50.8316 StartZ=0 EndX=-203.775 EndY=-50.8316 EndZ=0
    g18: LineSegment StartX=-209.375 StartY=-52.4316 StartZ=0 EndX=-203.775 EndY=-52.4316 EndZ=0
    g19: LineSegment StartX=-202.175 StartY=-50.8316 StartZ=0 EndX=-202.175 EndY=-46.8316 EndZ=0
    g20: LineSegment StartX=-203.775 StartY=-45.2316 StartZ=0 EndX=-209.375 EndY=-45.2316 EndZ=0
    g21: LineSegment StartX=-209.375 StartY=-45.2316 StartZ=0 EndX=-209.375 EndY=-52.4316 EndZ=0
    g22: ArcOfCircle CenterX=-203.775 CenterY=-46.8316 CenterZ=0 NormalX=0 NormalY=0 NormalZ=1 AngleXU=0 Radius=1.6 StartAngle=1.8e-15 EndAngle=1.5708
    g23: GeomPoint [constr] X=-202.175 Y=-45.2316 Z=0
    g24: ArcOfCircle CenterX=-203.775 CenterY=-50.8316 CenterZ=0 NormalX=0 NormalY=0 NormalZ=1 AngleXU=0 Radius=1.6 StartAngle=4.71239 EndAngle=6.28319
    g25: GeomPoint [constr] X=-202.175 Y=-52.4316 Z=0
    g26: LineSegment [constr] StartX=-207.775 StartY=-50.4316 StartZ=0 EndX=-207.775 EndY=-50.8316 EndZ=0
  constraints (69):
    c: Coincident(g1,g0)
    c: Coincident(g2,g1)
    c: Coincident(g3,g2)
    c: Coincident(g3,g0)
    c: Parallel(g0,g2)
    c: Perpendicular(g3,g0)
    c: Perpendicular(g1,g0)
    c: Coincident(g5,g4)
    c: Coincident(g7,g4)
    c: Distance(g3) = 2.2
    c: Distance(g2) = 2.2
    c: Parallel(g6,g2)
    c: Parallel(g6,g4)
    c: Perpendicular(g5,g6)
    c: Perpendicular(g7,g6)
    c: Distance(g13,g11) = 5.4
    c: Distance(g5,g13) = 5.4
    c: Coincident(g9,g8)
    c: Distance(g8) = 1.6
    c: Distance(g9) = 1.6
    c: Perpendicular(g9,g8)
    c: Parallel(g8,g6)
    c: Coincident(g8,g13)
    c: Distance(g8,g1) = 1.6
    c: Distance(g9,g1) = 1.6
    c: Tangent(g0,g-5)
    c: Distance(g0,g-6) = 23
    c: PointOnObject(g11,g7)
    c: PointOnObject(g11,g6)
    c: Tangent(g7,g10) = -1.5708
    c: Tangent(g6,g10) = -1.5708
    c: PointOnObject(g13,g5)
    c: Tangent(g5,g12) = -1.5708
    c: Tangent(g6,g12) = -1.5708
    c: Equal(g10,g12)
    c: Coincident(g10,g2)
    c: Vertical(g14)
    c: Coincident(g15,g14)
    c: Horizontal(g15)
    c: Coincident(g16,g15)
    c: Vertical(g16)
    c: Coincident(g17,g14)
    c: Coincident(g17,g16)
    c: Horizontal(g17)
    c: Distance(g16) = 4
    c: Distance(g15) = 4
    c: Horizontal(g18)
    c: Vertical(g19)
    c: Horizontal(g20)
    c: Coincident(g21,g20)
    c: Coincident(g21,g18)
    c: Vertical(g21)
    c: Distance(g20,g23) = 7.2
    c: Distance(g25,g23) = 7.2
    c: DistanceY(g18,g14) = 1.6
    c: DistanceX(g18,g14) = 1.6
    c: PointOnObject(g23,g20)
    c: PointOnObject(g23,g19)
    c: Tangent(g20,g22) = -1.5708
    c: Tangent(g19,g22) = -1.5708
    c: PointOnObject(g25,g19)
    c: Tangent(g18,g24) = -1.5708
    c: Tangent(g19,g24) = -1.5708
    c: Equal(g22,g24)
    c: Coincident(g22,g15)
    c: Vertical(g26)
    c: Distance(g26) = 0.4
    c: Coincident(g26,g-4)
    c: Coincident(g14,g26)
FEATURE [Part::Extrusion] Extrude045  label="Extrude fermi per driver solenoide e alimentatore"
  Base = -> Sketch042
  Dir = (0,-1,2e-16)
  DirMode = 2
  FaceMakerClass = Part::FaceMakerBullseye
  FaceMakerMode = 3
  LengthFwd = 25.2
  LengthRev = 0
  Solid = true
  Symmetric = true
FEATURE [Sketcher::SketchObject] Sketch043  label="scavo pulizia fermo alimentatore"
  ArcFitTolerance = 1e-06
  AttachmentSupport = -> [XZ_Plane]
  ExternalGeometry = -> [Sketch042,Sketch036,Sketch037]
  FullyConstrained = true
  MakeInternals = false
  MapMode = 5
  Placement = pos=(0,0,0) rot=(1,0,0;1.5708rad)
  sketch-geometry (6):
    g0: LineSegment StartX=-209.375 StartY=-52.4316 StartZ=0 EndX=-209.375 EndY=-50.4316 EndZ=0
    g1: LineSegment StartX=-209.375 StartY=-50.4316 StartZ=0 EndX=-207.775 EndY=-50.4316 EndZ=0
    g2: LineSegment StartX=-207.775 StartY=-50.4316 StartZ=0 EndX=-207.775 EndY=-45.2316 EndZ=0
    g3: LineSegment StartX=-207.775 StartY=-45.2316 StartZ=0 EndX=-202.175 EndY=-45.2316 EndZ=0
    g4: LineSegment StartX=-202.175 StartY=-45.2316 StartZ=0 EndX=-202.175 EndY=-52.4316 EndZ=0
    g5: LineSegment StartX=-202.175 StartY=-52.4316 StartZ=0 EndX=-209.375 EndY=-52.4316 EndZ=0
  constraints (13):
    c: Vertical(g0)
    c: Coincident(g1,g0)
    c: Coincident(g2,g1)
    c: Coincident(g3,g2)
    c: Coincident(g4,g3)
    c: Coincident(g5,g4)
    c: Coincident(g5,g0)
    c: Horizontal(g5)
    c: Coincident(g0,g-6)
    c: Tangent(g1,g-8)
    c: Tangent(g2,g-4)
    c: Tangent(g3,g-7)
    c: Tangent(g4,g-3)
FEATURE [Part::Extrusion] Extrude046  label="Extrude scavo pulizia fermo alimentatore"
  Base = -> Sketch043
  Dir = (0,-1,2e-16)
  DirMode = 2
  FaceMakerClass = Part::FaceMakerBullseye
  FaceMakerMode = 3
  LengthFwd = 19.5
  LengthRev = 0
  Solid = true
  Symmetric = true
FEATURE [Sketcher::SketchObject] Sketch044  label="buchini per fissaggio oled"
  ArcFitTolerance = 1e-06
  AttachmentSupport = -> [YZ_Plane]
  ExternalGeometry = -> [Sketch]
  FullyConstrained = true
  MakeInternals = false
  MapMode = 5
  Placement = pos=(0,0,0) rot=(0.57735,0.57735,0.57735;2.0944rad)
  sketch-geometry (5):
    g0: LineSegment [constr] StartX=1.5e-14 StartY=67.3588 StartZ=0 EndX=0 EndY=64.3588 EndZ=0
    g1: LineSegment [constr] StartX=0 StartY=64.3588 StartZ=0 EndX=10.4 EndY=64.3588 EndZ=0
    g2: LineSegment [constr] StartX=0 StartY=64.3588 StartZ=0 EndX=-10.4 EndY=64.3588 EndZ=0
    g3: Circle CenterX=10.4 CenterY=64.3588 CenterZ=0 NormalX=0 NormalY=0 NormalZ=1 AngleXU=0 Radius=1.5
    g4: Circle CenterX=-10.4 CenterY=64.3588 CenterZ=0 NormalX=0 NormalY=0 NormalZ=1 AngleXU=0 Radius=1.5
  constraints (13):
    c: Distance(g0) = 3
    c: PointOnObject(g0,g-2)
    c: Coincident(g1,g0)
    c: Horizontal(g1)
    c: Coincident(g2,g0)
    c: Horizontal(g2)
    c: DistanceX(g1,g1) = 10.4
    c: Coincident(g3,g1)
    c: Diameter(g4) = 3
    c: Coincident(g4,g2)
    c: Coincident(g0,g-7)
    c: Equal(g1,g2)
    c: Equal(g4,g3)
FEATURE [Part::Extrusion] Extrude047  label="Extrude buchini per fissaggio oled"
  Base = -> Sketch044
  Dir = (1,0,0)
  DirMode = 2
  FaceMakerClass = Part::FaceMakerBullseye
  FaceMakerMode = 3
  LengthFwd = 10
  LengthRev = 0
  Placement = pos=(-186,0,0) rot=(0,0,1;0rad)
  Solid = true
  Symmetric = false
FEATURE [Sketcher::SketchObject] Sketch046  label="scavo 5x5 neopixel"
  ArcFitTolerance = 1e-06
  AttachmentSupport = -> [YZ_Plane002]
  FullyConstrained = true
  MakeInternals = false
  MapMode = 5
  Placement = pos=(0,0,0) rot=(0.57735,0.57735,0.57735;2.0944rad)
  sketch-geometry (4):
    g0: LineSegment StartX=-2.7 StartY=2.7 StartZ=0 EndX=2.7 EndY=2.7 EndZ=0
    g1: LineSegment StartX=2.7 StartY=2.7 StartZ=0 EndX=2.7 EndY=-2.7 EndZ=0
    g2: LineSegment StartX=2.7 StartY=-2.7 StartZ=0 EndX=-2.7 EndY=-2.7 EndZ=0
    g3: LineSegment StartX=-2.7 StartY=-2.7 StartZ=0 EndX=-2.7 EndY=2.7 EndZ=0
  constraints (11):
    c: Horizontal(g0)
    c: Coincident(g1,g0)
    c: Vertical(g1)
    c: Coincident(g2,g1)
    c: Horizontal(g2)
    c: Coincident(g3,g2)
    c: Coincident(g3,g0)
    c: Vertical(g3)
    c: DistanceX(g0,g0) = 5.4
    c: DistanceY(g1,g1) = 5.4
    c: Symmetric(g0,g1,g-1)
FEATURE [Sketcher::SketchObject] Sketch047  label="scavo 10x10 neopixel corpo"
  ArcFitTolerance = 1e-06
  AttachmentOffset = pos=(0,0,1) rot=(0,0,1;0rad)
  AttachmentSupport = -> [YZ_Plane002]
  FullyConstrained = true
  MakeInternals = false
  MapMode = 5
  Placement = pos=(1,0,0) rot=(0.57735,0.57735,0.57735;2.0944rad)
  sketch-geometry (4):
    g0: LineSegment StartX=-5 StartY=5.1 StartZ=0 EndX=5 EndY=5.1 EndZ=0
    g1: LineSegment StartX=5 StartY=5.1 StartZ=0 EndX=5 EndY=-5.1 EndZ=0
    g2: LineSegment StartX=5 StartY=-5.1 StartZ=0 EndX=-5 EndY=-5.1 EndZ=0
    g3: LineSegment StartX=-5 StartY=-5.1 StartZ=0 EndX=-5 EndY=5.1 EndZ=0
  constraints (11):
    c: Horizontal(g0)
    c: Coincident(g1,g0)
    c: Vertical(g1)
    c: Coincident(g2,g1)
    c: Horizontal(g2)
    c: Coincident(g3,g2)
    c: Coincident(g3,g0)
    c: Vertical(g3)
    c: DistanceX(g0,g0) = 10
    c: DistanceY(g1,g1) = 10.2
    c: Symmetric(g0,g2,g-1)
FEATURE [Sketcher::SketchObject] Sketch048  label="buco per perno blocco neopixel"
  ArcFitTolerance = 1e-06
  AttachmentSupport = -> [XZ_Plane002]
  FullyConstrained = true
  MakeInternals = false
  MapMode = 5
  Placement = pos=(0,0,0) rot=(1,0,0;1.5708rad)
  sketch-geometry (4):
    g0: LineSegment StartX=3 StartY=1.2 StartZ=0 EndX=3 EndY=-1.2 EndZ=0
    g1: LineSegment StartX=3 StartY=-1.2 StartZ=0 EndX=5.4 EndY=-1.2 EndZ=0
    g2: LineSegment StartX=5.4 StartY=-1.2 StartZ=0 EndX=5.4 EndY=1.2 EndZ=0
    g3: LineSegment StartX=5.4 StartY=1.2 StartZ=0 EndX=3 EndY=1.2 EndZ=0
  constraints (11):
    c: Coincident(g1,g0)
    c: Horizontal(g1)
    c: Coincident(g2,g1)
    c: Vertical(g2)
    c: Coincident(g3,g2)
    c: Coincident(g3,g0)
    c: Horizontal(g3)
    c: DistanceX(g1,g1) = 2.4
    c: DistanceY(g2,g2) = 2.4
    c: Symmetric(g0,g0,g-1)
    c: DistanceX(g-1,g0) = 3
FEATURE [Sketcher::SketchObject] Sketch045  label="blocco principale per neopixel"
  ArcFitTolerance = 1e-06
  AttachmentSupport = -> [XZ_Plane002]
  ExternalGeometry = -> [Sketch048]
  FullyConstrained = true
  MakeInternals = false
  MapMode = 5
  Placement = pos=(0,0,0) rot=(1,0,0;1.5708rad)
  sketch-geometry (6):
    g0: LineSegment StartX=0 StartY=5.1 StartZ=0 EndX=0 EndY=-5.1 EndZ=0
    g1: LineSegment StartX=0 StartY=-5.1 StartZ=0 EndX=3 EndY=-5.1 EndZ=0
    g2: LineSegment StartX=7 StartY=-1.1 StartZ=0 EndX=7 EndY=5.1 EndZ=0
    g3: LineSegment StartX=7 StartY=5.1 StartZ=0 EndX=0 EndY=5.1 EndZ=0
    g4: ArcOfCircle CenterX=3 CenterY=-1.1 CenterZ=0 NormalX=0 NormalY=0 NormalZ=1 AngleXU=0 Radius=4 StartAngle=4.71239 EndAngle=6.28319
    g5: GeomPoint [constr] X=7 Y=-5.1 Z=0
  constraints (15):
    c: Vertical(g0)
    c: Coincident(g1,g0)
    c: Horizontal(g1)
    c: Vertical(g2)
    c: Coincident(g3,g2)
    c: Coincident(g3,g0)
    c: Horizontal(g3)
    c: DistanceY(g0,g0) = 10.2
    c: Symmetric(g0,g0,g-1)
    c: DistanceX(g3,g3) = 7
    c: PointOnObject(g5,g2)
    c: PointOnObject(g5,g1)
    c: Tangent(g2,g4) = -1.5708
    c: Tangent(g1,g4) = -1.5708
    c: DistanceX(g-3,g1) = 0
FEATURE [Sketcher::SketchObject] Sketch049  label="rinforzi esterni per corpo neopoixel"
  ArcFitTolerance = 1e-06
  AttachmentSupport = -> [XZ_Plane002]
  ExternalGeometry = -> [Sketch045]
  FullyConstrained = true
  MakeInternals = false
  MapMode = 5
  Placement = pos=(0,0,0) rot=(1,0,0;1.5708rad)
  sketch-geometry (8):
    g0: LineSegment StartX=1 StartY=-4.1 StartZ=0 EndX=2 EndY=-4.1 EndZ=0
    g1: LineSegment StartX=2 StartY=-4.1 StartZ=0 EndX=2 EndY=-5.1 EndZ=0
    g2: LineSegment StartX=2 StartY=-5.1 StartZ=0 EndX=1 EndY=-5.1 EndZ=0
    g3: LineSegment StartX=1 StartY=-5.1 StartZ=0 EndX=1 EndY=-4.1 EndZ=0
    g4: LineSegment StartX=1 StartY=5.1 StartZ=0 EndX=2 EndY=5.1 EndZ=0
    g5: LineSegment StartX=2 StartY=5.1 StartZ=0 EndX=2 EndY=4.1 EndZ=0
    g6: LineSegment StartX=2 StartY=4.1 StartZ=0 EndX=1 EndY=4.1 EndZ=0
    g7: LineSegment StartX=1 StartY=4.1 StartZ=0 EndX=1 EndY=5.1 EndZ=0
  constraints (24):
    c: Horizontal(g0)
    c: Coincident(g1,g0)
    c: Vertical(g1)
    c: Coincident(g2,g1)
    c: Horizontal(g2)
    c: Coincident(g3,g2)
    c: Coincident(g3,g0)
    c: Vertical(g3)
    c: Horizontal(g4)
    c: Coincident(g5,g4)
    c: Vertical(g5)
    c: Coincident(g6,g5)
    c: Horizontal(g6)
    c: Coincident(g7,g6)
    c: Coincident(g7,g4)
    c: Vertical(g7)
    c: DistanceX(g4,g4) = 1
    c: DistanceY(g5,g5) = 1
    c: DistanceX(g0,g0) = 1
    c: DistanceY(g1,g1) = 1
    c: DistanceX(g-3,g4) = 1
    c: DistanceY(g-3,g4) = 0
    c: DistanceX(g-4,g2) = 1
    c: DistanceY(g2,g-4) = 0
FEATURE [Sketcher::SketchObject] Sketch052  label="scavo saldature driver solenoide"
  ArcFitTolerance = 1e-06
  AttachmentSupport = -> [XZ_Plane]
  ExternalGeometry = -> [Sketch038]
  FullyConstrained = true
  MakeInternals = false
  MapMode = 5
  Placement = pos=(0,0,0) rot=(1,0,0;1.5708rad)
  sketch-geometry (4):
    g0: LineSegment StartX=-195.485 StartY=-6.49608 StartZ=0 EndX=-197.176 EndY=-10.1213 EndZ=0
    g1: LineSegment StartX=-197.176 StartY=-10.1213 StartZ=0 EndX=-195.726 EndY=-10.7975 EndZ=0
    g2: LineSegment StartX=-195.726 StartY=-10.7975 StartZ=0 EndX=-194.035 EndY=-7.17226 EndZ=0
    g3: LineSegment StartX=-194.035 StartY=-7.17226 StartZ=0 EndX=-195.485 EndY=-6.49608 EndZ=0
  constraints (11):
    c: Coincident(g1,g0)
    c: Coincident(g2,g1)
    c: Coincident(g3,g2)
    c: Coincident(g3,g0)
    c: Parallel(g2,g0)
    c: Perpendicular(g2,g3)
    c: Perpendicular(g1,g2,g1) = 1.5708
    c: Parallel(g2,g-3)
    c: Distance(g2) = 4
    c: Distance(g3) = 1.6
    c: Coincident(g2,g-3)
FEATURE [Part::Extrusion] Extrude055  label="Extrude scavo saldature driver solenoide"
  Base = -> Sketch052
  Dir = (0,-1,2e-16)
  DirMode = 2
  FaceMakerClass = Part::FaceMakerBullseye
  FaceMakerMode = 3
  LengthFwd = 6
  LengthRev = 0
  Solid = true
  Symmetric = true
FEATURE [Sketcher::SketchObject] Sketch053  label="scavo saldature rumble"
  ArcFitTolerance = 1e-06
  AttachmentSupport = -> [XZ_Plane]
  ExternalGeometry = -> [Sketch019]
  FullyConstrained = true
  MakeInternals = false
  MapMode = 5
  Placement = pos=(0,0,0) rot=(1,0,0;1.5708rad)
  sketch-geometry (4):
    g0: LineSegment StartX=-165.001 StartY=-43.1663 StartZ=0 EndX=-166.238 EndY=-46.9705 EndZ=0
    g1: LineSegment StartX=-166.238 StartY=-46.9705 StartZ=0 EndX=-165.096 EndY=-47.3413 EndZ=0
    g2: LineSegment StartX=-165.096 StartY=-47.3413 StartZ=0 EndX=-163.86 EndY=-43.5371 EndZ=0
    g3: LineSegment StartX=-163.86 StartY=-43.5371 StartZ=0 EndX=-165.001 EndY=-43.1663 EndZ=0
  constraints (11):
    c: Coincident(g1,g0)
    c: Coincident(g2,g1)
    c: Coincident(g3,g2)
    c: Coincident(g3,g0)
    c: Parallel(g0,g2)
    c: Perpendicular(g3,g0)
    c: Perpendicular(g1,g0)
    c: Parallel(g0,g-3)
    c: Distance(g0) = 4
    c: Distance(g1) = 1.2
    c: Coincident(g0,g-3)
FEATURE [Part::Extrusion] Extrude056  label="Extrude scavo saldature rumble"
  Base = -> Sketch053
  Dir = (0,-1,2e-16)
  DirMode = 2
  FaceMakerClass = Part::FaceMakerBullseye
  FaceMakerMode = 3
  LengthFwd = 8.4
  LengthRev = 0
  Solid = true
  Symmetric = true
FEATURE [Sketcher::SketchObject] Sketch054  label="scavo saldature alimentatore connettore USB"
  ArcFitTolerance = 1e-06
  AttachmentSupport = -> [XZ_Plane]
  ExternalGeometry = -> [Sketch037]
  FullyConstrained = true
  MakeInternals = false
  MapMode = 5
  Placement = pos=(0,0,0) rot=(1,0,0;1.5708rad)
  sketch-geometry (4):
    g0: LineSegment StartX=-209.575 StartY=-80.4316 StartZ=0 EndX=-210.375 EndY=-80.4316 EndZ=0
    g1: LineSegment StartX=-210.375 StartY=-80.4316 StartZ=0 EndX=-210.375 EndY=-72.4316 EndZ=0
    g2: LineSegment StartX=-210.375 StartY=-72.4316 StartZ=0 EndX=-209.575 EndY=-72.4316 EndZ=0
    g3: LineSegment StartX=-209.575 StartY=-72.4316 StartZ=0 EndX=-209.575 EndY=-80.4316 EndZ=0
  constraints (11):
    c: Horizontal(g0)
    c: Coincident(g1,g0)
    c: Vertical(g1)
    c: Coincident(g2,g1)
    c: Horizontal(g2)
    c: Coincident(g3,g2)
    c: Coincident(g3,g0)
    c: Vertical(g3)
    c: DistanceX(g0,g0) = 0.8
    c: DistanceY(g3,g3) = 8
    c: Coincident(g0,g-4)
FEATURE [Part::Extrusion] Extrude057  label="Extrude scavo saldature alimentatore connettore USB"
  Base = -> Sketch054
  Dir = (0,-1,2e-16)
  DirMode = 2
  FaceMakerClass = Part::FaceMakerBullseye
  FaceMakerMode = 3
  LengthFwd = 11
  LengthRev = 0
  Solid = true
  Symmetric = true
FEATURE [Sketcher::SketchObject] Sketch055  label="buco interno per micro switch"
  ArcFitTolerance = 1e-06
  AttachmentSupport = -> [XZ_Plane]
  ExternalGeometry = -> [Sketch]
  FullyConstrained = true
  MakeInternals = false
  MapMode = 5
  Placement = pos=(0,0,0) rot=(1,0,0;1.5708rad)
  sketch-geometry (11):
    g0: LineSegment [constr] StartX=-194.483 StartY=34.2854 StartZ=0 EndX=-196.022 EndY=30.0568 EndZ=0
    g1: LineSegment [constr] StartX=-196.022 StartY=30.0568 StartZ=0 EndX=-197.561 EndY=25.8282 EndZ=0
    g2: LineSegment [constr] StartX=-196.022 StartY=30.0568 StartZ=0 EndX=-194.143 EndY=29.3727 EndZ=0
    g3: LineSegment [constr] StartX=-196.022 StartY=30.0568 StartZ=0 EndX=-197.902 EndY=30.7408 EndZ=0
    g4: LineSegment StartX=-196.362 StartY=34.9694 StartZ=0 EndX=-192.604 EndY=33.6014 EndZ=0
    g5: LineSegment StartX=-199.441 StartY=26.5122 StartZ=0 EndX=-195.682 EndY=25.1441 EndZ=0
    g6: LineSegment StartX=-192.604 StartY=33.6014 StartZ=0 EndX=-195.682 EndY=25.1441 EndZ=0
    g7: LineSegment StartX=-196.362 StartY=34.9694 StartZ=0 EndX=-199.441 EndY=26.5122 EndZ=0
    g8: GeomPoint [constr] X=-187.821 Y=29.2 Z=0
    g9: LineSegment [constr] StartX=-188.505 StartY=27.3206 StartZ=0 EndX=-196.022 EndY=30.0568 EndZ=0
    g10: LineSegment [constr] StartX=-187.821 StartY=29.2 StartZ=0 EndX=-188.505 EndY=27.3206 EndZ=0
  constraints (27):
    c: Coincident(g2,g0)
    c: Parallel(g0,g-3)
    c: Tangent(g1,g0) = -1.5708
    c: Perpendicular(g0,g2)
    c: Tangent(g2,g3)
    c: Distance(g0,g1) = 9
    c: Equal(g0,g1)
    c: Distance(g3,g2) = 4
    c: Equal(g2,g3)
    c: Parallel(g3,g4)
    c: Symmetric(g4,g4,g0)
    c: Parallel(g6,g1)
    c: Parallel(g7,g1)
    c: Symmetric(g6,g6,g2)
    c: Symmetric(g5,g5,g1)
    c: Symmetric(g7,g7,g3)
    c: Coincident(g7,g4)
    c: Coincident(g6,g4)
    c: Coincident(g5,g6)
    c: Symmetric(g-3,g-3,g8)
    c: Perpendicular(g-3,g9)
    c: Distance(g9) = 8
    c: Coincident(g3,g9)
    c: Coincident(g10,g8)
    c: Parallel(g10,g-3)
    c: Distance(g10) = 2
    c: Coincident(g10,g9)
FEATURE [Sketcher::SketchObject] Sketch056  label="buco esterno per micro switch"
  ArcFitTolerance = 1e-06
  AttachmentSupport = -> [XZ_Plane]
  ExternalGeometry = -> [Sketch055]
  FullyConstrained = true
  MakeInternals = false
  MapMode = 5
  Placement = pos=(0,0,0) rot=(1,0,0;1.5708rad)
  sketch-geometry (17):
    g0: GeomPoint [constr] X=-194.143 Y=29.3727 Z=0
    g1: GeomPoint [constr] X=-194.483 Y=34.2854 Z=0
    g2: GeomPoint [constr] X=-197.902 Y=30.7408 Z=0
    g3: GeomPoint [constr] X=-197.561 Y=25.8282 Z=0
    g4: GeomPoint [constr] X=-196.022 Y=30.0568 Z=0
    g5: LineSegment [constr] StartX=-194.483 StartY=34.2854 StartZ=0 EndX=-196.022 EndY=30.0568 EndZ=0
    g6: LineSegment [constr] StartX=-196.022 StartY=30.0568 StartZ=0 EndX=-197.561 EndY=25.8282 EndZ=0
    g7: LineSegment [constr] StartX=-197.902 StartY=30.7408 StartZ=0 EndX=-196.022 EndY=30.0568 EndZ=0
    g8: LineSegment [constr] StartX=-196.022 StartY=30.0568 StartZ=0 EndX=-194.143 EndY=29.3727 EndZ=0
    g9: LineSegment [constr] StartX=-195.338 StartY=31.9362 StartZ=0 EndX=-196.022 EndY=30.0568 EndZ=0
    g10: LineSegment [constr] StartX=-196.022 StartY=30.0568 StartZ=0 EndX=-196.706 EndY=28.1774 EndZ=0
    g11: LineSegment [constr] StartX=-196.022 StartY=30.0568 StartZ=0 EndX=-196.821 EndY=30.3475 EndZ=0
    g12: LineSegment [constr] StartX=-196.022 StartY=30.0568 StartZ=0 EndX=-195.223 EndY=29.7661 EndZ=0
    g13: LineSegment StartX=-194.539 StartY=31.6454 StartZ=0 EndX=-195.907 EndY=27.8867 EndZ=0
    g14: LineSegment StartX=-196.137 StartY=32.2269 StartZ=0 EndX=-197.505 EndY=28.4681 EndZ=0
    g15: LineSegment StartX=-196.137 StartY=32.2269 StartZ=0 EndX=-194.539 EndY=31.6454 EndZ=0
    g16: LineSegment StartX=-197.505 StartY=28.4681 StartZ=0 EndX=-195.907 EndY=27.8867 EndZ=0
  constraints (34):
    c: Symmetric(g-5,g-5,g1)
    c: Symmetric(g-5,g-6,g0)
    c: Symmetric(g-6,g-6,g3)
    c: Symmetric(g-5,g-6,g2)
    c: Coincident(g5,g1)
    c: Coincident(g5,g4)
    c: Coincident(g6,g4)
    c: Coincident(g6,g3)
    c: Equal(g5,g6)
    c: Coincident(g7,g2)
    c: Coincident(g7,g4)
    c: Coincident(g8,g4)
    c: Coincident(g8,g0)
    c: Equal(g7,g8)
    c: Coincident(g11,g9)
    c: Coincident(g12,g9)
    c: Tangent(g10,g9) = -1.5708
    c: Perpendicular(g11,g9)
    c: Parallel(g9,g-4)
    c: Equal(g9,g10)
    c: Parallel(g12,g11)
    c: Equal(g11,g12)
    c: Distance(g11,g12) = 1.7
    c: Distance(g9,g10) = 4
    c: Symmetric(g13,g13,g12)
    c: Parallel(g13,g9)
    c: Symmetric(g14,g14,g11)
    c: Symmetric(g15,g15,g9)
    c: Parallel(g15,g11)
    c: Symmetric(g16,g16,g10)
    c: Coincident(g16,g14)
    c: Coincident(g15,g14)
    c: Coincident(g13,g15)
    c: Coincident(g9,g4)
FEATURE [Sketcher::SketchObject] Sketch057  label="buco interno per SWITCH"
  ArcFitTolerance = 1e-06
  AttachmentSupport = -> [XZ_Plane]
  ExternalGeometry = -> [Sketch]
  FullyConstrained = true
  MakeInternals = false
  MapMode = 5
  Placement = pos=(0,0,0) rot=(1,0,0;1.5708rad)
  sketch-geometry (10):
    g0: GeomPoint [constr] X=-187.821 Y=29.2 Z=0
    g1: LineSegment [constr] StartX=-188.505 StartY=27.3206 StartZ=0 EndX=-193.203 EndY=29.0307 EndZ=0
    g2: LineSegment [constr] StartX=-190.809 StartY=35.6086 StartZ=0 EndX=-195.597 EndY=22.4529 EndZ=0
    g3: GeomPoint [constr] X=-193.203 Y=29.0307 Z=0
    g4: LineSegment [constr] StartX=-196.492 StartY=30.2278 StartZ=0 EndX=-189.914 EndY=27.8336 EndZ=0
    g5: LineSegment StartX=-194.098 StartY=36.8056 StartZ=0 EndX=-187.52 EndY=34.4115 EndZ=0
    g6: LineSegment StartX=-194.098 StartY=36.8056 StartZ=0 EndX=-198.886 EndY=23.6499 EndZ=0
    g7: LineSegment StartX=-187.52 StartY=34.4115 StartZ=0 EndX=-192.308 EndY=21.2558 EndZ=0
    g8: LineSegment StartX=-198.886 StartY=23.6499 StartZ=0 EndX=-192.308 EndY=21.2558 EndZ=0
    g9: LineSegment [constr] StartX=-187.821 StartY=29.2 StartZ=0 EndX=-188.505 EndY=27.3206 EndZ=0
  constraints (23):
    c: Symmetric(g-3,g-3,g0)
    c: Perpendicular(g1,g-3)
    c: Parallel(g2,g-3)
    c: Symmetric(g2,g2,g3)
    c: Perpendicular(g2,g4)
    c: Symmetric(g4,g4,g3)
    c: Distance(g2) = 14
    c: Distance(g4) = 7
    c: Distance(g1) = 5
    c: Parallel(g5,g4)
    c: Parallel(g7,g2)
    c: Symmetric(g5,g5,g2)
    c: Symmetric(g6,g6,g4)
    c: Symmetric(g7,g7,g4)
    c: Symmetric(g8,g8,g2)
    c: Coincident(g6,g5)
    c: Coincident(g7,g5)
    c: Coincident(g8,g7)
    c: Coincident(g3,g1)
    c: Coincident(g9,g0)
    c: Parallel(g9,g-3)
    c: Distance(g9) = 2
    c: Coincident(g1,g9)
FEATURE [Sketcher::SketchObject] Sketch058  label="buco esterno per SWITCH"
  ArcFitTolerance = 1e-06
  AttachmentSupport = -> [XZ_Plane]
  ExternalGeometry = -> [Sketch057]
  FullyConstrained = true
  MakeInternals = false
  MapMode = 5
  Placement = pos=(0,0,0) rot=(1,0,0;1.5708rad)
  sketch-geometry (12):
    g0: GeomPoint [constr] X=-190.809 Y=35.6086 Z=0
    g1: GeomPoint [constr] X=-196.492 Y=30.2278 Z=0
    g2: GeomPoint [constr] X=-189.914 Y=27.8336 Z=0
    g3: GeomPoint [constr] X=-195.597 Y=22.4529 Z=0
    g4: GeomPoint [constr] X=-193.203 Y=29.0307 Z=0
    g5: LineSegment [constr] StartX=-192.006 StartY=32.3196 StartZ=0 EndX=-194.4 EndY=25.7418 EndZ=0
    g6: GeomPoint [constr] X=-193.203 Y=29.0307 Z=0
    g7: LineSegment [constr] StartX=-195.082 StartY=29.7148 StartZ=0 EndX=-191.324 EndY=28.3467 EndZ=0
    g8: LineSegment StartX=-193.885 StartY=33.0037 StartZ=0 EndX=-190.127 EndY=31.6356 EndZ=0
    g9: LineSegment StartX=-190.127 StartY=31.6356 StartZ=0 EndX=-192.521 EndY=25.0578 EndZ=0
    g10: LineSegment StartX=-196.28 StartY=26.4258 StartZ=0 EndX=-192.521 EndY=25.0578 EndZ=0
    g11: LineSegment StartX=-193.885 StartY=33.0037 StartZ=0 EndX=-196.28 EndY=26.4258 EndZ=0
  constraints (21):
    c: Symmetric(g-6,g-6,g3)
    c: Symmetric(g-4,g-6,g2)
    c: Symmetric(g-5,g-4,g0)
    c: Symmetric(g-5,g-6,g1)
    c: Symmetric(g1,g2,g4)
    c: Parallel(g5,g-4)
    c: Symmetric(g5,g5,g6)
    c: Perpendicular(g7,g5)
    c: Symmetric(g7,g7,g6)
    c: Distance(g5) = 7
    c: Distance(g7) = 4
    c: Parallel(g8,g7)
    c: Parallel(g11,g5)
    c: Symmetric(g8,g8,g5)
    c: Symmetric(g9,g9,g7)
    c: Symmetric(g10,g10,g5)
    c: Symmetric(g11,g11,g7)
    c: Coincident(g11,g8)
    c: Coincident(g9,g8)
    c: Coincident(g9,g10)
    c: Coincident(g6,g4)
FEATURE [Part::Extrusion] Extrude060  label="Extrude buco interno per SWITCH destro"
  Base = -> Sketch057
  Dir = (0,-1,2e-16)
  DirMode = 2
  FaceMakerClass = Part::FaceMakerBullseye
  FaceMakerMode = 3
  LengthFwd = 13.2
  LengthRev = 0
  Placement = pos=(0,2.6,0) rot=(0,0,1;0rad)
  Solid = true
  Symmetric = false
FEATURE [Part::Extrusion] Extrude061  label="Extrude buco esterno per SWITCH destro"
  Base = -> Sketch058
  Dir = (0,-1,2e-16)
  DirMode = 2
  FaceMakerClass = Part::FaceMakerBullseye
  FaceMakerMode = 3
  LengthFwd = 2
  LengthRev = 0
  Placement = pos=(0,-10.6,0) rot=(0,0,1;0rad)
  Solid = true
  Symmetric = false
FEATURE [Sketcher::SketchObject] Sketch059  label="buco per spazio introduzione SWITCH"
  ArcFitTolerance = 1e-06
  AttachmentSupport = -> [XZ_Plane]
  ExternalGeometry = -> [Sketch057,Sketch010]
  FullyConstrained = true
  MakeInternals = false
  MapMode = 5
  Placement = pos=(0,0,0) rot=(1,0,0;1.5708rad)
  sketch-geometry (8):
    g0: LineSegment [constr] StartX=-201.368 StartY=36.3521 StartZ=0 EndX=-195.094 EndY=34.0687 EndZ=0
    g1: LineSegment [constr] StartX=-194.098 StartY=36.8056 StartZ=0 EndX=-195.094 EndY=34.0687 EndZ=0
    g2: LineSegment StartX=-198.658 StartY=24.2771 StartZ=0 EndX=-199.654 EndY=21.5401 EndZ=0
    g3: LineSegment StartX=-199.654 StartY=21.5401 StartZ=0 EndX=-181.196 EndY=14.822 EndZ=0
    g4: LineSegment StartX=-181.196 StartY=14.822 StartZ=0 EndX=-180.2 EndY=17.559 EndZ=0
    g5: LineSegment StartX=-180.2 StartY=17.559 StartZ=0 EndX=-198.658 EndY=24.2771 EndZ=0
    g6: LineSegment [constr] StartX=-204.932 StartY=26.5605 StartZ=0 EndX=-198.658 EndY=24.2771 EndZ=0
    g7: LineSegment [constr] StartX=-198.658 StartY=24.2771 StartZ=0 EndX=-199.654 EndY=21.5401 EndZ=0
  constraints (20):
    c: Parallel(g1,g-3)
    c: Parallel(g0,g-4)
    c: Coincident(g0,g-4)
    c: Coincident(g1,g-3)
    c: Coincident(g0,g1)
    c: Coincident(g3,g2)
    c: Coincident(g4,g3)
    c: Coincident(g5,g4)
    c: Coincident(g5,g2)
    c: Parallel(g5,g-5)
    c: Parallel(g3,g-5)
    c: Parallel(g4,g-6)
    c: DistanceX(g-6,g4) = 0
    c: Coincident(g6,g-5)
    c: Equal(g6,g0)
    c: Coincident(g7,g6)
    c: Equal(g7,g1)
    c: Tangent(g7,g-3)
    c: Coincident(g2,g6)
    c: Coincident(g2,g7)
FEATURE [Part::Extrusion] Extrude062  label="Extrude buco per spazio introduzione SWITCH"
  Base = -> Sketch059
  Dir = (0,-1,2e-16)
  DirMode = 2
  FaceMakerClass = Part::FaceMakerBullseye
  FaceMakerMode = 3
  LengthFwd = 13.2
  LengthRev = 0
  Solid = true
  Symmetric = true
FEATURE [Part::Extrusion] Extrude063  label="Extrude buco interno per SWITCH sinistro"
  Base = -> Sketch057
  Dir = (0,-1,2e-16)
  DirMode = 2
  FaceMakerClass = Part::FaceMakerBullseye
  FaceMakerMode = 3
  LengthFwd = 13.2
  LengthRev = 0
  Placement = pos=(0,10.6,0) rot=(0,0,1;0rad)
  Solid = true
  Symmetric = false
FEATURE [Part::Extrusion] Extrude064  label="Extrude buco esterno per SWITCH sinistro"
  Base = -> Sketch058
  Dir = (0,-1,2e-16)
  DirMode = 2
  FaceMakerClass = Part::FaceMakerBullseye
  FaceMakerMode = 3
  LengthFwd = 2
  LengthRev = 0
  Placement = pos=(0,12.6,0) rot=(0,0,1;0rad)
  Solid = true
  Symmetric = false
FEATURE [Sketcher::SketchObject] Sketch061  label="struttura esterna blocco switch"
  ArcFitTolerance = 1e-06
  AttachmentSupport = -> [XZ_Plane003]
  FullyConstrained = true
  MakeInternals = false
  MapMode = 5
  Placement = pos=(0,0,0) rot=(1,0,0;1.5708rad)
  sketch-geometry (5):
    g0: LineSegment StartX=-1 StartY=-5.1 StartZ=0 EndX=1 EndY=-5.1 EndZ=0
    g1: LineSegment StartX=1 StartY=-5.1 StartZ=0 EndX=1 EndY=5.1 EndZ=0
    g2: LineSegment StartX=1 StartY=5.1 StartZ=0 EndX=-1 EndY=5.1 EndZ=0
    g3: LineSegment StartX=-1 StartY=5.1 StartZ=0 EndX=-1 EndY=-5.1 EndZ=0
    g4: GeomPoint [constr] X=0 Y=0 Z=0
  constraints (12):
    c: Coincident(g0,g1)
    c: Coincident(g1,g2)
    c: Coincident(g2,g3)
    c: Coincident(g3,g0)
    c: Horizontal(g0)
    c: Horizontal(g2)
    c: Vertical(g1)
    c: Vertical(g3)
    c: Symmetric(g2,g0,g4)
    c: Distance(g1,g3) = 2
    c: Distance(g0,g2) = 10.2
    c: Coincident(g4,g-1)
FEATURE [Sketcher::SketchObject] Sketch062  label="struttura interna blocco switch"
  ArcFitTolerance = 1e-06
  AttachmentSupport = -> [XZ_Plane003]
  ExternalGeometry = -> [Sketch061]
  FullyConstrained = true
  MakeInternals = false
  MapMode = 5
  Placement = pos=(0,0,0) rot=(1,0,0;1.5708rad)
  sketch-geometry (5):
    g0: LineSegment StartX=-1 StartY=3.1 StartZ=0 EndX=-1 EndY=-3.1 EndZ=0
    g1: LineSegment StartX=-1 StartY=-3.1 StartZ=0 EndX=1 EndY=-3.1 EndZ=0
    g2: LineSegment StartX=1 StartY=-3.1 StartZ=0 EndX=1 EndY=3.1 EndZ=0
    g3: LineSegment StartX=1 StartY=3.1 StartZ=0 EndX=-1 EndY=3.1 EndZ=0
    g4: GeomPoint [constr] X=0 Y=0 Z=0
  constraints (12):
    c: Coincident(g0,g1)
    c: Coincident(g1,g2)
    c: Coincident(g2,g3)
    c: Coincident(g3,g0)
    c: Vertical(g0)
    c: Vertical(g2)
    c: Horizontal(g1)
    c: Horizontal(g3)
    c: Symmetric(g2,g0,g4)
    c: Coincident(g4,g-1)
    c: Distance(g0) = 6.2
    c: Equal(g3,g-3)
FEATURE [Sketcher::SketchObject] Sketch063  label="blocchi tra switch"
  ArcFitTolerance = 1e-06
  AttachmentSupport = -> [XZ_Plane003]
  ExternalGeometry = -> [Sketch061,Sketch062]
  FullyConstrained = true
  MakeInternals = false
  MapMode = 5
  Placement = pos=(0,0,0) rot=(1,0,0;1.5708rad)
  sketch-geometry (8):
    g0: LineSegment StartX=-3 StartY=5.1 StartZ=0 EndX=-1 EndY=5.1 EndZ=0
    g1: LineSegment StartX=-1 StartY=5.1 StartZ=0 EndX=-1 EndY=3.1 EndZ=0
    g2: LineSegment StartX=-1 StartY=3.1 StartZ=0 EndX=-3 EndY=3.1 EndZ=0
    g3: LineSegment StartX=-3 StartY=3.1 StartZ=0 EndX=-3 EndY=5.1 EndZ=0
    g4: LineSegment StartX=-3 StartY=-3.1 StartZ=0 EndX=-1 EndY=-3.1 EndZ=0
    g5: LineSegment StartX=-1 StartY=-3.1 StartZ=0 EndX=-1 EndY=-5.1 EndZ=0
    g6: LineSegment StartX=-1 StartY=-5.1 StartZ=0 EndX=-3 EndY=-5.1 EndZ=0
    g7: LineSegment StartX=-3 StartY=-5.1 StartZ=0 EndX=-3 EndY=-3.1 EndZ=0
  constraints (20):
    c: Horizontal(g0)
    c: Coincident(g1,g0)
    c: Coincident(g2,g1)
    c: Horizontal(g2)
    c: Coincident(g3,g2)
    c: Coincident(g3,g0)
    c: Vertical(g3)
    c: Horizontal(g4)
    c: Coincident(g5,g4)
    c: Coincident(g6,g5)
    c: Horizontal(g6)
    c: Coincident(g7,g6)
    c: Coincident(g7,g4)
    c: Vertical(g7)
    c: Coincident(g0,g-4)
    c: Coincident(g1,g-5)
    c: Coincident(g4,g-6)
    c: Coincident(g5,g-7)
    c: Distance(g0) = 2
    c: Distance(g4) = 2
FEATURE [Sketcher::SketchObject] Sketch066  label="piano per rampino"
  ArcFitTolerance = 1e-06
  AttachmentSupport = -> [XZ_Plane002]
  ExternalGeometry = -> [Sketch045]
  FullyConstrained = true
  MakeInternals = false
  MapMode = 5
  Placement = pos=(0,0,0) rot=(1,0,0;1.5708rad)
  sketch-geometry (4):
    g0: LineSegment StartX=5.4 StartY=5.1 StartZ=0 EndX=5.4 EndY=3.9 EndZ=0
    g1: LineSegment StartX=5.4 StartY=3.9 StartZ=0 EndX=7 EndY=3.9 EndZ=0
    g2: LineSegment StartX=7 StartY=3.9 StartZ=0 EndX=7 EndY=5.1 EndZ=0
    g3: LineSegment StartX=7 StartY=5.1 StartZ=0 EndX=5.4 EndY=5.1 EndZ=0
  constraints (11):
    c: Coincident(g0,g1)
    c: Coincident(g1,g2)
    c: Coincident(g2,g3)
    c: Coincident(g3,g0)
    c: Vertical(g0)
    c: Vertical(g2)
    c: Horizontal(g1)
    c: Horizontal(g3)
    c: Distance(g0,g2) = 1.6
    c: Distance(g1,g3) = 1.2
    c: Coincident(g2,g-3)
FEATURE [Sketcher::SketchObject] Sketch064  label="rampini_per_serraggio_struttura"
  ArcFitTolerance = 1e-06
  AttachmentSupport = -> [XZ_Plane002]
  ExternalGeometry = -> [Sketch066,Sketch045]
  FullyConstrained = true
  MakeInternals = false
  MapMode = 5
  Placement = pos=(0,0,0) rot=(1,0,0;1.5708rad)
  sketch-geometry (7):
    g0: LineSegment StartX=7 StartY=5.1 StartZ=0 EndX=7 EndY=3.9 EndZ=0
    g1: LineSegment StartX=7 StartY=3.9 StartZ=0 EndX=9 EndY=3.9 EndZ=0
    g2: LineSegment StartX=7 StartY=5.1 StartZ=0 EndX=7 EndY=5.1 EndZ=0
    g3: LineSegment StartX=7 StartY=5.1 StartZ=0 EndX=7 EndY=7.5 EndZ=0
    g4: LineSegment StartX=9 StartY=5.1 StartZ=0 EndX=9 EndY=3.9 EndZ=0
    g5: LineSegment StartX=7 StartY=7.5 StartZ=0 EndX=9 EndY=7.5 EndZ=0
    g6: LineSegment StartX=9 StartY=7.5 StartZ=0 EndX=9 EndY=5.1 EndZ=0
  constraints (20):
    c: Vertical(g0)
    c: Coincident(g1,g0)
    c: Horizontal(g1)
    c: Coincident(g2,g0)
    c: Horizontal(g2)
    c: Coincident(g3,g2)
    c: Vertical(g3)
    c: Coincident(g5,g3)
    c: Coincident(g4,g6)
    c: Coincident(g4,g1)
    c: Vertical(g4)
    c: Coincident(g0,g-3)
    c: DistanceY(g-4,g3) = 2.4
    c: DistanceX(g1,g1) = 2
    c: DistanceY(g2,g6) = 0
    c: DistanceX(g2,g2) = 0
    c: DistanceY(g0,g0) = 1.2
    c: Coincident(g5,g6)
    c: Horizontal(g5)
    c: Vertical(g6)
FEATURE [Sketcher::SketchObject] Sketch067  label="perno per blocco switch"
  ArcFitTolerance = 1e-06
  AttachmentSupport = -> [XZ_Plane]
  ExternalGeometry = -> [Sketch,Sketch010]
  FullyConstrained = true
  MakeInternals = false
  MapMode = 5
  Placement = pos=(0,0,0) rot=(1,0,0;1.5708rad)
  sketch-geometry (14):
    g0: LineSegment StartX=-191.073 StartY=24.9429 StartZ=0 EndX=-185.81 EndY=23.0276 EndZ=0
    g1: LineSegment StartX=-183.76 StartY=23.9839 StartZ=0 EndX=-182.392 EndY=27.7427 EndZ=0
    g2: LineSegment StartX=-183.348 StartY=29.7934 StartZ=0 EndX=-188.61 EndY=31.7087 EndZ=0
    g3: LineSegment StartX=-188.61 StartY=31.7087 StartZ=0 EndX=-191.073 EndY=24.9429 EndZ=0
    g4: GeomPoint [constr] X=-186.459 Y=27.0946 Z=0
    g5: LineSegment StartX=-189.022 StartY=25.8992 StartZ=0 EndX=-185.263 EndY=24.5311 EndZ=0
    g6: LineSegment StartX=-185.263 StartY=24.5311 StartZ=0 EndX=-183.895 EndY=28.2899 EndZ=0
    g7: LineSegment StartX=-183.895 StartY=28.2899 StartZ=0 EndX=-187.654 EndY=29.658 EndZ=0
    g8: LineSegment StartX=-187.654 StartY=29.658 StartZ=0 EndX=-189.022 EndY=25.8992 EndZ=0
    g9: GeomPoint [constr] X=-186.459 Y=27.0946 Z=0
    g10: ArcOfCircle CenterX=-185.263 CenterY=24.5311 CenterZ=0 NormalX=0 NormalY=0 NormalZ=1 AngleXU=0 Radius=1.6 StartAngle=4.36332 EndAngle=5.93412
    g11: GeomPoint [constr] X=-184.307 Y=22.4804 Z=0
    g12: ArcOfCircle CenterX=-183.895 CenterY=28.2899 CenterZ=0 NormalX=0 NormalY=0 NormalZ=1 AngleXU=0 Radius=1.6 StartAngle=5.93412 EndAngle=7.50492
    g13: GeomPoint [constr] X=-181.844 Y=29.2462 Z=0
  constraints (30):
    c: Coincident(g2,g3)
    c: Coincident(g3,g0)
    c: Symmetric(g13,g0,g4)
    c: Distance(g11,g3) = 7.2
    c: Distance(g0,g2) = 7.2
    c: Parallel(g3,g1)
    c: Parallel(g2,g0)
    c: Perpendicular(g2,g3)
    c: Coincident(g5,g6)
    c: Coincident(g6,g7)
    c: Coincident(g7,g8)
    c: Coincident(g8,g5)
    c: Symmetric(g7,g5,g9)
    c: Distance(g6,g8) = 4
    c: Distance(g5,g7) = 4
    c: Coincident(g9,g4)
    c: Parallel(g8,g6)
    c: Parallel(g7,g5)
    c: Perpendicular(g7,g8)
    c: Tangent(g8,g-3)
    c: Tangent(g2,g-4)
    c: PointOnObject(g11,g1)
    c: PointOnObject(g11,g0)
    c: Tangent(g1,g10) = -1.5708
    c: Tangent(g0,g10) = -1.5708
    c: PointOnObject(g13,g1)
    c: Tangent(g1,g12) = -1.5708
    c: Tangent(g2,g12) = -1.5708
    c: Equal(g10,g12)
    c: Coincident(g10,g5)
FEATURE [Part::Extrusion] Extrude072  label="Extrude perno per blocco switch"
  Base = -> Sketch067
  Dir = (0,-1,2e-16)
  DirMode = 2
  FaceMakerClass = Part::FaceMakerBullseye
  FaceMakerMode = 3
  LengthFwd = 25.2
  LengthRev = 0
  Solid = true
  Symmetric = true
FEATURE [Part::MultiFuse] Fusion
  Refine = true
  Shapes = -> [Extrude,Sweep,Extrude007,Extrude011,Extrude005,Extrude012,Extrude013,Extrude016,Extrude031,Extrude039,Extrude045,Extrude072]
FEATURE [Part::Cut] Cut
  Base = -> Fusion
  Refine = true
  Tool = -> Extrude001
FEATURE [Part::Cut] Cut001
  Base = -> Cut
  Refine = true
  Tool = -> Extrude004
FEATURE [Part::Cut] Cut002
  Base = -> Cut001
  Refine = true
  Tool = -> Extrude006
FEATURE [Part::Cut] Cut003
  Base = -> Cut002
  Refine = true
  Tool = -> Extrude008
FEATURE [Part::Cut] Cut004
  Base = -> Cut003
  Refine = true
  Tool = -> Extrude009
FEATURE [Part::Cut] Cut005
  Base = -> Cut004
  Refine = true
  Tool = -> Extrude010
FEATURE [Part::Cut] Cut006
  Base = -> Cut005
  Refine = true
  Tool = -> Extrude014
FEATURE [Part::Cut] Cut007
  Base = -> Cut006
  Refine = true
  Tool = -> Extrude015
FEATURE [Part::Cut] Cut008
  Base = -> Cut007
  Refine = true
  Tool = -> Extrude018
FEATURE [Part::Cut] Cut009
  Base = -> Cut008
  Refine = true
  Tool = -> Extrude019
FEATURE [Part::Cut] Cut010
  Base = -> Cut009
  Refine = true
  Tool = -> Extrude020
FEATURE [Part::Cut] Cut011
  Base = -> Cut010
  Refine = true
  Tool = -> Extrude021
FEATURE [Part::Cut] Cut012
  Base = -> Cut011
  Refine = true
  Tool = -> Extrude022
FEATURE [Part::Cut] Cut013
  Base = -> Cut012
  Refine = true
  Tool = -> Extrude023
FEATURE [Part::Cut] Cut014
  Base = -> Cut013
  Refine = true
  Tool = -> Extrude032
FEATURE [Part::Cut] Cut015
  Base = -> Cut014
  Refine = true
  Tool = -> Extrude033
FEATURE [Part::Cut] Cut016
  Base = -> Cut015
  Refine = true
  Tool = -> Extrude034
FEATURE [Part::Cut] Cut017
  Base = -> Cut016
  Refine = true
  Tool = -> Extrude035
FEATURE [Part::Cut] Cut018
  Base = -> Cut017
  Refine = true
  Tool = -> Extrude036
FEATURE [Part::Cut] Cut019
  Base = -> Cut018
  Refine = true
  Tool = -> Extrude037
FEATURE [Part::Cut] Cut020
  Base = -> Cut019
  Refine = true
  Tool = -> Extrude030
FEATURE [Part::Cut] Cut022
  Base = -> Cut020
  Refine = true
  Tool = -> Extrude038
FEATURE [Part::Cut] Cut023
  Base = -> Cut022
  Refine = true
  Tool = -> Extrude041
FEATURE [Part::Cut] Cut024
  Base = -> Cut023
  Refine = true
  Tool = -> Extrude040
FEATURE [Part::Cut] Cut025
  Base = -> Cut024
  Refine = true
  Tool = -> Extrude042
FEATURE [Part::Cut] Cut026
  Base = -> Cut025
  Refine = true
  Tool = -> Extrude043
FEATURE [Part::Cut] Cut027
  Base = -> Cut026
  Refine = true
  Tool = -> Extrude044
FEATURE [Part::Cut] Cut028
  Base = -> Cut027
  Refine = true
  Tool = -> Extrude046
FEATURE [Part::Cut] Cut029
  Base = -> Cut028
  Refine = true
  Tool = -> Extrude047
FEATURE [Part::Cut] Cut033
  Base = -> Cut029
  Refine = true
  Tool = -> Extrude055
FEATURE [Part::Cut] Cut034
  Base = -> Cut033
  Refine = true
  Tool = -> Extrude056
FEATURE [Part::Cut] Cut035
  Base = -> Cut034
  Refine = true
  Tool = -> Extrude057
FEATURE [Part::Cut] Cut037
  Base = -> Cut035
  Refine = true
  Tool = -> Extrude060
FEATURE [Part::Cut] Cut038
  Base = -> Cut037
  Refine = true
  Tool = -> Extrude061
FEATURE [Part::Cut] Cut039
  Base = -> Cut038
  Refine = true
  Tool = -> Extrude063
FEATURE [Part::Cut] Cut040
  Base = -> Cut039
  Refine = true
  Tool = -> Extrude064
FEATURE [Part::Cut] Cut041
  Base = -> Cut040
  Refine = true
  Tool = -> Extrude062
FEATURE [Sketcher::SketchObject] Sketch068  label="base con smusso sopra neopixel"
  ArcFitTolerance = 1e-06
  AttachmentSupport = -> [YZ_Plane002]
  FullyConstrained = true
  MakeInternals = false
  MapMode = 5
  Placement = pos=(0,0,0) rot=(0.57735,0.57735,0.57735;2.0944rad)
  sketch-geometry (5):
    g0: LineSegment StartX=-9.5 StartY=-6.1 StartZ=0 EndX=9.5 EndY=-6.1 EndZ=0
    g1: LineSegment StartX=9.5 StartY=-6.1 StartZ=0 EndX=9.5 EndY=6.1 EndZ=0
    g2: LineSegment StartX=9.5 StartY=6.1 StartZ=0 EndX=-9.5 EndY=6.1 EndZ=0
    g3: LineSegment StartX=-9.5 StartY=6.1 StartZ=0 EndX=-9.5 EndY=-6.1 EndZ=0
    g4: GeomPoint [constr] X=0 Y=0 Z=0
  constraints (12):
    c: Coincident(g0,g1)
    c: Coincident(g1,g2)
    c: Coincident(g2,g3)
    c: Coincident(g3,g0)
    c: Horizontal(g0)
    c: Horizontal(g2)
    c: Vertical(g1)
    c: Vertical(g3)
    c: Symmetric(g2,g0,g4)
    c: Distance(g1,g3) = 19
    c: Distance(g0,g2) = 12.2
    c: Coincident(g4,g-1)
FEATURE [Sketcher::SketchObject] Sketch069  label="cilindro minore"
  ArcFitTolerance = 1e-06
  AttachmentSupport = -> [XZ_Plane004]
  FullyConstrained = true
  MakeInternals = false
  MapMode = 5
  Placement = pos=(0,0,0) rot=(1,0,0;1.5708rad)
  sketch-geometry (1):
    g0: Circle CenterX=0 CenterY=0 CenterZ=0 NormalX=0 NormalY=0 NormalZ=1 AngleXU=0 Radius=5.8
  constraints (2):
    c: Diameter(g0) = 11.6
    c: Coincident(g0,g-1)
FEATURE [Sketcher::SketchObject] Sketch070  label="cilindro maggiore"
  ArcFitTolerance = 1e-06
  AttachmentSupport = -> [XZ_Plane004]
  ExternalGeometry = -> [Sketch069]
  FullyConstrained = true
  MakeInternals = false
  MapMode = 5
  Placement = pos=(0,0,0) rot=(1,0,0;1.5708rad)
  sketch-geometry (1):
    g0: Circle CenterX=0 CenterY=0 CenterZ=0 NormalX=0 NormalY=0 NormalZ=1 AngleXU=0 Radius=6.5
  constraints (2):
    c: Coincident(g0,g-1)
    c: Diameter(g0) = 13
FEATURE [Sketcher::SketchObject] Sketch071  label="buco interno"
  ArcFitTolerance = 1e-06
  AttachmentSupport = -> [XZ_Plane004]
  ExternalGeometry = -> [Sketch069]
  FullyConstrained = true
  MakeInternals = false
  MapMode = 5
  Placement = pos=(0,0,0) rot=(1,0,0;1.5708rad)
  sketch-geometry (1):
    g0: Circle CenterX=0 CenterY=0 CenterZ=0 NormalX=0 NormalY=0 NormalZ=1 AngleXU=0 Radius=5
  constraints (2):
    c: Coincident(g0,g-1)
    c: Diameter(g0) = 10
FEATURE [PartDesign::Pad] Pad
  Direction = (0,-1,2e-16)
  Length = 1.2
  Length2 = 10
  Placement = pos=(0,0,0) rot=(1,0,0;1.5708rad)
  Profile = -> Sketch070
  ReferenceAxis = -> Sketch070 [N_Axis]
  Refine = true
  Suppressed = false
  Type = 0
FEATURE [PartDesign::Pad] Pad001
  BaseFeature = -> Pad
  Direction = (0,-1,2e-16)
  Length = 5.6
  Length2 = 10
  Placement = pos=(0,0,0) rot=(1,0,0;1.5708rad)
  Profile = -> Sketch069
  ReferenceAxis = -> Sketch069 [N_Axis]
  Refine = true
  Suppressed = false
  Type = 0
FEATURE [PartDesign::Pocket] Pocket
  BaseFeature = -> Pad001
  Direction = (0,1,-2e-16)
  Length = 7
  Length2 = 5
  Midplane = true
  Placement = pos=(0,0,0) rot=(1,0,0;1.5708rad)
  Profile = -> Sketch071
  ReferenceAxis = -> Sketch071 [N_Axis]
  Refine = true
  Suppressed = false
  Type = 0
FEATURE [PartDesign::Fillet] Fillet
  Base = -> Pocket [Face7]
  BaseFeature = -> Pocket
  Placement = pos=(0,0,0) rot=(1,0,0;1.5708rad)
  Radius = 1
  Refine = true
  SupportTransform = false
  Suppressed = false
  UseAllEdges = false
FEATURE [PartDesign::Body] Body004  label="pulsanti lato sinistro"
  AllowCompound = false
  Group = -> [Sketch069,Sketch070,Sketch071,Pad,Pad001,Pocket,Fillet]
  Origin = -> Origin004
  Tip = -> Fillet
FEATURE [Sketcher::SketchObject] Sketch072  label="buco per saldature e diodo driver solenoide"
  ArcFitTolerance = 1e-06
  AttachmentSupport = -> [XZ_Plane]
  ExternalGeometry = -> [Sketch038]
  FullyConstrained = true
  MakeInternals = false
  MapMode = 5
  Placement = pos=(0,0,0) rot=(1,0,0;1.5708rad)
  sketch-geometry (4):
    g0: LineSegment StartX=-211.362 StartY=-44.3309 StartZ=0 EndX=-206.291 EndY=-33.4552 EndZ=0
    g1: LineSegment StartX=-206.291 StartY=-33.4552 StartZ=0 EndX=-208.647 EndY=-32.3564 EndZ=0
    g2: LineSegment StartX=-208.647 StartY=-32.3564 StartZ=0 EndX=-213.719 EndY=-43.2321 EndZ=0
    g3: LineSegment StartX=-213.719 StartY=-43.2321 StartZ=0 EndX=-211.362 EndY=-44.3309 EndZ=0
  constraints (11):
    c: Coincident(g1,g0)
    c: Coincident(g2,g1)
    c: Coincident(g3,g2)
    c: Coincident(g3,g0)
    c: Parallel(g-3,g0)
    c: Parallel(g0,g2)
    c: Perpendicular(g0,g3)
    c: Perpendicular(g1,g0)
    c: Distance(g3) = 2.6
    c: Distance(g2) = 12
    c: Coincident(g0,g-3)
FEATURE [Part::Extrusion] Extrude074  label="Extrude buco per saldature e diodo driver solenoide"
  Base = -> Sketch072
  Dir = (0,-1,2e-16)
  DirMode = 2
  FaceMakerClass = Part::FaceMakerBullseye
  FaceMakerMode = 3
  LengthFwd = 14.6
  LengthRev = 0
  Solid = true
  Symmetric = true
FEATURE [Part::Cut] Cut042
  Base = -> Cut041
  Refine = true
  Tool = -> Extrude074
FEATURE [Sketcher::SketchObject] Sketch073  label="fori slargati blocco solenoide"
  ArcFitTolerance = 1e-06
  AttachmentSupport = -> [XY_Plane]
  ExternalGeometry = -> [Sketch030]
  FullyConstrained = true
  MakeInternals = false
  MapMode = 5
  sketch-geometry (2):
    g0: Circle CenterX=-152.209 CenterY=6.95 CenterZ=0 NormalX=0 NormalY=0 NormalZ=1 AngleXU=0 Radius=3.7
    g1: Circle CenterX=-130.41 CenterY=-6.95 CenterZ=0 NormalX=0 NormalY=0 NormalZ=1 AngleXU=0 Radius=3.7
  constraints (4):
    c: Diameter(g0) = 7.4
    c: Coincident(g0,g-3)
    c: Diameter(g1) = 7.4
    c: Coincident(g1,g-4)
FEATURE [Part::Extrusion] Extrude075  label="Extrude fori slargati blocco solenoide"
  Base = -> Sketch073
  Dir = (0,0,1)
  DirMode = 2
  FaceMakerClass = Part::FaceMakerBullseye
  FaceMakerMode = 3
  LengthFwd = 1.5
  LengthRev = 0
  Placement = pos=(0,0,36.4) rot=(0,0,1;0rad)
  Solid = true
  Symmetric = false
FEATURE [Part::Cut] Cut043
  Base = -> Cut042
  Refine = true
  Tool = -> Extrude075
FEATURE [Sketcher::SketchObject] Sketch074  label="lato sx pistola"
  ArcFitTolerance = 1e-06
  AttachmentSupport = -> [XZ_Plane]
  ExternalGeometry = -> [Sketch016,Sketch,Sketch058]
  FullyConstrained = true
  MakeInternals = false
  MapMode = 5
  Placement = pos=(0,0,0) rot=(1,0,0;1.5708rad)
  sketch-geometry (37):
    g0: LineSegment StartX=-82.8 StartY=3.2 StartZ=0 EndX=0 EndY=3.2 EndZ=0
    g1: LineSegment StartX=-82.8 StartY=3.2 StartZ=0 EndX=-82.8 EndY=6.2 EndZ=0
    g2: LineSegment [constr] StartX=-107.6 StartY=18 StartZ=0 EndX=-107.6 EndY=20 EndZ=0
    g3: LineSegment [constr] StartX=-132.428 StartY=18 StartZ=0 EndX=-132.428 EndY=20 EndZ=0
    g4: LineSegment StartX=-132.428 StartY=20 StartZ=0 EndX=-107.6 EndY=20 EndZ=0
    g5: ArcOfCircle CenterX=-107.6 CenterY=4 CenterZ=0 NormalX=0 NormalY=0 NormalZ=1 AngleXU=0 Radius=16 StartAngle=0.137937 EndAngle=1.5708
    g6: LineSegment StartX=-82.8 StartY=6.2 StartZ=0 EndX=-91.752 EndY=6.2 EndZ=0
    g7: LineSegment [constr] StartX=-145.743 StartY=8.32624 StartZ=0 EndX=-147.645 EndY=8.94427 EndZ=0
    g8: ArcOfCircle CenterX=-132.428 CenterY=4 CenterZ=0 NormalX=0 NormalY=0 NormalZ=1 AngleXU=0 Radius=16 StartAngle=1.5708 EndAngle=2.82743
    g9: LineSegment StartX=-215.932 StartY=-80.4316 StartZ=0 EndX=-176.685 EndY=-80.4316 EndZ=0
    g10: LineSegment StartX=-147.645 StartY=8.94427 StartZ=0 EndX=-176.685 EndY=-80.4316 EndZ=0
    g11: LineSegment [constr] StartX=-193.988 StartY=-2.33927 StartZ=0 EndX=-192.176 EndY=-3.18451 EndZ=0
    g12: LineSegment [constr] StartX=-217.232 StartY=-52.1862 StartZ=0 EndX=-215.42 EndY=-53.0314 EndZ=0
    g13: LineSegment StartX=-192.176 StartY=-3.18451 StartZ=0 EndX=-215.42 EndY=-53.0314 EndZ=0
    g14: ArcOfCircle CenterX=-184.801 CenterY=-67.3089 CenterZ=0 NormalX=0 NormalY=0 NormalZ=1 AngleXU=0 Radius=33.7833 StartAngle=2.70526 EndAngle=3.54053
    g15: ArcOfCircle CenterX=-207.583 CenterY=4 CenterZ=0 NormalX=0 NormalY=0 NormalZ=1 AngleXU=0 Radius=17 StartAngle=5.84685 EndAngle=7.56663
    g16: LineSegment StartX=-202.765 StartY=20.303 StartZ=0 EndX=-195.887 EndY=39.2 EndZ=0
    g17: LineSegment [constr] StartX=-193.885 StartY=33.0037 StartZ=0 EndX=-197.644 EndY=34.3718 EndZ=0
    g18: LineSegment StartX=-195.887 StartY=39.2 StartZ=0 EndX=0 EndY=39.2 EndZ=0
    g19: LineSegment StartX=0 StartY=3.2 StartZ=0 EndX=0 EndY=39.2 EndZ=0
    g20: LineSegment StartX=-189.939 StartY=31.5672 StartZ=0 EndX=-192.333 EndY=24.9893 EndZ=0
    g21: LineSegment StartX=-196.467 StartY=26.4942 StartZ=0 EndX=-194.073 EndY=33.0721 EndZ=0
    g22: Circle CenterX=-213.443 CenterY=-76.8316 CenterZ=0 NormalX=0 NormalY=0 NormalZ=1 AngleXU=0 Radius=1.8
    g23: Circle CenterX=-179.305 CenterY=-76.8316 CenterZ=0 NormalX=0 NormalY=0 NormalZ=1 AngleXU=0 Radius=1.8
    g24: Circle CenterX=-184.08 CenterY=34.8 CenterZ=0 NormalX=0 NormalY=0 NormalZ=1 AngleXU=0 Radius=1.8
    g25: Circle CenterX=-78.51 CenterY=34.8 CenterZ=0 NormalX=0 NormalY=0 NormalZ=1 AngleXU=0 Radius=1.8
    g26: Circle CenterX=-78.51 CenterY=7.6 CenterZ=0 NormalX=0 NormalY=0 NormalZ=1 AngleXU=0 Radius=1.8
    g27: Circle CenterX=-5.6 CenterY=34.8 CenterZ=0 NormalX=0 NormalY=0 NormalZ=1 AngleXU=0 Radius=1.8
    g28: Circle CenterX=-5.6 CenterY=7.6 CenterZ=0 NormalX=0 NormalY=0 NormalZ=1 AngleXU=0 Radius=1.8
    g29: LineSegment StartX=-190.127 StartY=31.6356 StartZ=0 EndX=-189.939 EndY=31.5672 EndZ=0
    g30: LineSegment StartX=-194.073 StartY=33.0721 StartZ=0 EndX=-193.885 EndY=33.0037 EndZ=0
    g31: LineSegment StartX=-193.885 StartY=33.0037 StartZ=0 EndX=-190.127 EndY=31.6356 EndZ=0
    g32: LineSegment StartX=-196.467 StartY=26.4942 StartZ=0 EndX=-192.333 EndY=24.9893 EndZ=0
    g33: Circle CenterX=-19 CenterY=21.2 CenterZ=0 NormalX=0 NormalY=0 NormalZ=1 AngleXU=0 Radius=6.3
    g34: Circle CenterX=-42 CenterY=21.2 CenterZ=0 NormalX=0 NormalY=0 NormalZ=1 AngleXU=0 Radius=6.3
    g35: Circle CenterX=-65 CenterY=21.2 CenterZ=0 NormalX=0 NormalY=0 NormalZ=1 AngleXU=0 Radius=6.3
    g36: LineSegment [constr] StartX=-4 StartY=21.2 StartZ=0 EndX=-65 EndY=21.2 EndZ=0
  constraints (96):
    c: Coincident(g0,g-41)
    c: Horizontal(g0)
    c: PointOnObject(g0,g-39)
    c: Coincident(g1,g0)
    c: Vertical(g1)
    c: DistanceY(g1,g1) = 3
    c: Coincident(g2,g-17)
    c: Vertical(g2)
    c: Coincident(g3,g-16)
    c: Vertical(g3)
    c: DistanceY(g2,g2) = 2
    c: DistanceY(g3,g3) = 2
    c: Coincident(g4,g3)
    c: Coincident(g4,g2)
    c: Coincident(g5,g-17)
    c: Coincident(g5,g2)
    c: Coincident(g6,g1)
    c: Horizontal(g6)
    c: Coincident(g6,g5)
    c: Coincident(g7,g-15)
    c: Coincident(g8,g7)
    c: Coincident(g8,g3)
    c: Coincident(g8,g-15)
    c: Horizontal(g9)
    c: DistanceY(g-13,g9) = 2
    c: Coincident(g10,g7)
    c: Parallel(g10,g-14)
    c: Coincident(g9,g10)
    c: Distance(g11) = 2
    c: Coincident(g11,g-11)
    c: Perpendicular(g-11,g11)
    c: Distance(g12) = 2
    c: Coincident(g12,g-12)
    c: Perpendicular(g-11,g12)
    c: Coincident(g13,g11)
    c: Coincident(g13,g12)
    c: Coincident(g14,g-32)
    c: Coincident(g14,g12)
    c: Coincident(g14,g9)
    c: Coincident(g15,g-10)
    c: Coincident(g15,g11)
    c: Parallel(g16,g-22)
    c: Distance(g17) = 4
    c: PointOnObject(g17,g16)
    c: Coincident(g15,g16)
    c: Horizontal(g18)
    c: Coincident(g18,g16)
    c: Coincident(g19,g0)
    c: PointOnObject(g19,g-39)
    c: DistanceY(g19,g-36) = 2
    c: Coincident(g18,g19)
    c: Diameter(g22) = 3.6
    c: Coincident(g22,g-9)
    c: Diameter(g23) = 3.6
    c: Coincident(g23,g-8)
    c: Diameter(g24) = 3.6
    c: Diameter(g25) = 3.6
    c: Diameter(g26) = 3.6
    c: Diameter(g27) = 3.6
    c: Diameter(g28) = 3.6
    c: Coincident(g27,g-4)
    c: Coincident(g28,g-3)
    c: Coincident(g25,g-6)
    c: Coincident(g26,g-5)
    c: Coincident(g24,g-7)
    c: Parallel(g20,g-21)
    c: Equal(g20,g-21)
    c: Parallel(g21,g-19)
    c: Equal(g21,g-19)
    c: Distance(g29) = 0.2
    c: Distance(g30) = 0.2
    c: Parallel(g29,g-20)
    c: Parallel(g31,g-20)
    c: Equal(g31,g-20)
    c: Coincident(g30,g31)
    c: Coincident(g31,g29)
    c: Coincident(g29,g-21)
    c: Parallel(g30,g31)
    c: Coincident(g17,g30)
    c: Coincident(g20,g29)
    c: Coincident(g21,g30)
    c: Perpendicular(g16,g17)
    c: Coincident(g32,g21)
    c: Coincident(g32,g20)
    c: Perpendicular(g10,g7)
    c: Diameter(g33) = 12.6
    c: Diameter(g34) = 12.6
    c: Diameter(g35) = 12.6
    c: Horizontal(g36)
    c: PointOnObject(g33,g36)
    c: PointOnObject(g34,g36)
    c: DistanceX(g34,g33) = 23
    c: DistanceX(g35,g34) = 23
    c: DistanceX(g33,g36) = 15
    c: Symmetric(g-24,g-24,g36)
    c: Coincident(g36,g35)
FEATURE [Sketcher::SketchObject] Sketch075  label="lato dx pistola"
  ArcFitTolerance = 1e-06
  AttachmentSupport = -> [XZ_Plane]
  ExternalGeometry = -> [Sketch016,Sketch,Sketch058,Sketch074]
  FullyConstrained = true
  MakeInternals = false
  MapMode = 5
  Placement = pos=(0,0,0) rot=(1,0,0;1.5708rad)
  sketch-geometry (61):
    g0: LineSegment StartX=-82.8 StartY=3.2 StartZ=0 EndX=0 EndY=3.2 EndZ=0
    g1: LineSegment StartX=-82.8 StartY=3.2 StartZ=0 EndX=-82.8 EndY=6.2 EndZ=0
    g2: LineSegment [constr] StartX=-107.6 StartY=18 StartZ=0 EndX=-107.6 EndY=20 EndZ=0
    g3: LineSegment [constr] StartX=-132.428 StartY=18 StartZ=0 EndX=-132.428 EndY=20 EndZ=0
    g4: LineSegment StartX=-132.428 StartY=20 StartZ=0 EndX=-107.6 EndY=20 EndZ=0
    g5: ArcOfCircle CenterX=-107.6 CenterY=4 CenterZ=0 NormalX=0 NormalY=0 NormalZ=1 AngleXU=0 Radius=16 StartAngle=0.137937 EndAngle=1.5708
    g6: LineSegment StartX=-82.8 StartY=6.2 StartZ=0 EndX=-91.752 EndY=6.2 EndZ=0
    g7: LineSegment [constr] StartX=-145.743 StartY=8.32624 StartZ=0 EndX=-147.645 EndY=8.94427 EndZ=0
    g8: ArcOfCircle CenterX=-132.428 CenterY=4 CenterZ=0 NormalX=0 NormalY=0 NormalZ=1 AngleXU=0 Radius=16 StartAngle=1.5708 EndAngle=2.82743
    g9: LineSegment StartX=-215.932 StartY=-80.4316 StartZ=0 EndX=-176.685 EndY=-80.4316 EndZ=0
    g10: LineSegment StartX=-147.645 StartY=8.94427 StartZ=0 EndX=-176.685 EndY=-80.4316 EndZ=0
    g11: LineSegment [constr] StartX=-193.988 StartY=-2.33927 StartZ=0 EndX=-192.176 EndY=-3.18451 EndZ=0
    g12: LineSegment [constr] StartX=-217.232 StartY=-52.1862 StartZ=0 EndX=-215.42 EndY=-53.0314 EndZ=0
    g13: LineSegment StartX=-192.176 StartY=-3.18451 StartZ=0 EndX=-215.42 EndY=-53.0314 EndZ=0
    g14: ArcOfCircle CenterX=-184.801 CenterY=-67.3089 CenterZ=0 NormalX=0 NormalY=0 NormalZ=1 AngleXU=0 Radius=33.7833 StartAngle=2.70526 EndAngle=3.54053
    g15: ArcOfCircle CenterX=-207.583 CenterY=4 CenterZ=0 NormalX=0 NormalY=0 NormalZ=1 AngleXU=0 Radius=17 StartAngle=5.84685 EndAngle=7.56663
    g16: LineSegment StartX=-202.765 StartY=20.303 StartZ=0 EndX=-195.887 EndY=39.2 EndZ=0
    g17: LineSegment [constr] StartX=-193.885 StartY=33.0037 StartZ=0 EndX=-197.644 EndY=34.3718 EndZ=0
    g18: LineSegment StartX=-195.887 StartY=39.2 StartZ=0 EndX=0 EndY=39.2 EndZ=0
    g19: LineSegment StartX=0 StartY=3.2 StartZ=0 EndX=0 EndY=39.2 EndZ=0
    g20: LineSegment StartX=-189.939 StartY=31.5672 StartZ=0 EndX=-192.333 EndY=24.9893 EndZ=0
    g21: LineSegment StartX=-196.467 StartY=26.4942 StartZ=0 EndX=-194.073 EndY=33.0721 EndZ=0
    g22: Circle CenterX=-213.443 CenterY=-76.8316 CenterZ=0 NormalX=0 NormalY=0 NormalZ=1 AngleXU=0 Radius=1.8
    g23: Circle CenterX=-179.305 CenterY=-76.8316 CenterZ=0 NormalX=0 NormalY=0 NormalZ=1 AngleXU=0 Radius=1.8
    g24: Circle CenterX=-184.08 CenterY=34.8 CenterZ=0 NormalX=0 NormalY=0 NormalZ=1 AngleXU=0 Radius=1.8
    g25: Circle CenterX=-78.51 CenterY=34.8 CenterZ=0 NormalX=0 NormalY=0 NormalZ=1 AngleXU=0 Radius=1.8
    g26: Circle CenterX=-78.51 CenterY=7.6 CenterZ=0 NormalX=0 NormalY=0 NormalZ=1 AngleXU=0 Radius=1.8
    g27: Circle CenterX=-5.6 CenterY=34.8 CenterZ=0 NormalX=0 NormalY=0 NormalZ=1 AngleXU=0 Radius=1.8
    g28: Circle CenterX=-5.6 CenterY=7.6 CenterZ=0 NormalX=0 NormalY=0 NormalZ=1 AngleXU=0 Radius=1.8
    g29: LineSegment StartX=-190.127 StartY=31.6356 StartZ=0 EndX=-189.939 EndY=31.5672 EndZ=0
    g30: LineSegment StartX=-194.073 StartY=33.0721 StartZ=0 EndX=-193.885 EndY=33.0037 EndZ=0
    g31: LineSegment StartX=-193.885 StartY=33.0037 StartZ=0 EndX=-190.127 EndY=31.6356 EndZ=0
    g32: LineSegment StartX=-196.467 StartY=26.4942 StartZ=0 EndX=-192.333 EndY=24.9893 EndZ=0
    g33: LineSegment [constr] StartX=-4 StartY=21.2 StartZ=0 EndX=-87.91 EndY=21.2 EndZ=0
    g34: GeomPoint [constr] X=-4 Y=21.2 Z=0
    g35: LineSegment [constr] StartX=-15.2 StartY=33.7 StartZ=0 EndX=-15.2 EndY=8.7 EndZ=0
    g36: LineSegment [constr] StartX=-15.2 StartY=33.7 StartZ=0 EndX=-56.2 EndY=33.7 EndZ=0
    g37: LineSegment [constr] StartX=-15.2 StartY=8.7 StartZ=0 EndX=-56.2 EndY=8.7 EndZ=0
    g38: LineSegment [constr] StartX=-56.2 StartY=33.7 StartZ=0 EndX=-56.2 EndY=8.7 EndZ=0
    g39: Circle CenterX=-18.6 CenterY=30.3 CenterZ=0 NormalX=0 NormalY=0 NormalZ=1 AngleXU=0 Radius=3.4
    g40: Circle CenterX=-18.6 CenterY=12.1 CenterZ=0 NormalX=0 NormalY=0 NormalZ=1 AngleXU=0 Radius=3.4
    g41: Circle CenterX=-43.2 CenterY=30.3 CenterZ=0 NormalX=0 NormalY=0 NormalZ=1 AngleXU=0 Radius=3.4
    g42: Circle CenterX=-43.2 CenterY=12.1 CenterZ=0 NormalX=0 NormalY=0 NormalZ=1 AngleXU=0 Radius=3.4
    g43: LineSegment [constr] StartX=-4 StartY=21.2 StartZ=0 EndX=-15.2 EndY=21.2 EndZ=0
    g44: LineSegment [constr] StartX=-15.2 StartY=21.2 StartZ=0 EndX=-36.2 EndY=21.2 EndZ=0
    g45: LineSegment [constr] StartX=-41.5 StartY=16.2 StartZ=0 EndX=-30.9 EndY=16.2 EndZ=0
    g46: LineSegment [constr] StartX=-30.9 StartY=16.2 StartZ=0 EndX=-30.9 EndY=26.2 EndZ=0
    g47: LineSegment [constr] StartX=-30.9 StartY=26.2 StartZ=0 EndX=-41.5 EndY=26.2 EndZ=0
    g48: LineSegment [constr] StartX=-41.5 StartY=26.2 StartZ=0 EndX=-41.5 EndY=16.2 EndZ=0
    g49: GeomPoint [constr] X=-36.2 Y=21.2 Z=0
    g50: Circle CenterX=-36.2 CenterY=21.2 CenterZ=0 NormalX=0 NormalY=0 NormalZ=1 AngleXU=0 Radius=2.8
    g51: LineSegment [constr] StartX=-24.2 StartY=26.7 StartZ=0 EndX=-24.2 EndY=15.7 EndZ=0
    g52: Circle CenterX=-24.2 CenterY=26.7 CenterZ=0 NormalX=0 NormalY=0 NormalZ=1 AngleXU=0 Radius=3
    g53: Circle CenterX=-24.2 CenterY=15.7 CenterZ=0 NormalX=0 NormalY=0 NormalZ=1 AngleXU=0 Radius=3
    g54: GeomPoint X=-18.6 Y=30.3 Z=0
    g55: GeomPoint X=-18.6 Y=12.1 Z=0
    g56: GeomPoint X=-43.2 Y=12.1 Z=0
    g57: GeomPoint X=-43.2 Y=30.3 Z=0
    g58: Circle CenterX=-65 CenterY=21.2 CenterZ=0 NormalX=0 NormalY=0 NormalZ=1 AngleXU=0 Radius=1.5
    g59: Circle CenterX=-42 CenterY=21.2 CenterZ=0 NormalX=0 NormalY=0 NormalZ=1 AngleXU=0 Radius=1.5
    g60: Circle CenterX=-19 CenterY=21.2 CenterZ=0 NormalX=0 NormalY=0 NormalZ=1 AngleXU=0 Radius=1.5
  constraints (149):
    c: Coincident(g0,g-41)
    c: Horizontal(g0)
    c: PointOnObject(g0,g-39)
    c: Coincident(g1,g0)
    c: Vertical(g1)
    c: DistanceY(g1,g1) = 3
    c: Coincident(g2,g-17)
    c: Vertical(g2)
    c: Coincident(g3,g-16)
    c: Vertical(g3)
    c: DistanceY(g2,g2) = 2
    c: DistanceY(g3,g3) = 2
    c: Coincident(g4,g3)
    c: Coincident(g4,g2)
    c: Coincident(g5,g-17)
    c: Coincident(g5,g2)
    c: Coincident(g6,g1)
    c: Horizontal(g6)
    c: Coincident(g6,g5)
    c: Coincident(g7,g-15)
    c: Coincident(g8,g7)
    c: Coincident(g8,g3)
    c: Coincident(g8,g-15)
    c: Horizontal(g9)
    c: DistanceY(g-13,g9) = 2
    c: Coincident(g10,g7)
    c: Parallel(g10,g-14)
    c: Coincident(g9,g10)
    c: Distance(g11) = 2
    c: Coincident(g11,g-11)
    c: Perpendicular(g-11,g11)
    c: Distance(g12) = 2
    c: Coincident(g12,g-12)
    c: Perpendicular(g-11,g12)
    c: Coincident(g13,g11)
    c: Coincident(g13,g12)
    c: Coincident(g14,g-32)
    c: Coincident(g14,g12)
    c: Coincident(g14,g9)
    c: Coincident(g15,g-10)
    c: Coincident(g15,g11)
    c: Parallel(g16,g-22)
    c: Distance(g17) = 4
    c: PointOnObject(g17,g16)
    c: Coincident(g15,g16)
    c: Horizontal(g18)
    c: Coincident(g18,g16)
    c: Coincident(g19,g0)
    c: PointOnObject(g19,g-39)
    c: DistanceY(g19,g-36) = 2
    c: Coincident(g18,g19)
    c: Diameter(g22) = 3.6
    c: Coincident(g22,g-9)
    c: Diameter(g23) = 3.6
    c: Coincident(g23,g-8)
    c: Diameter(g24) = 3.6
    c: Diameter(g25) = 3.6
    c: Diameter(g26) = 3.6
    c: Diameter(g27) = 3.6
    c: Diameter(g28) = 3.6
    c: Coincident(g27,g-4)
    c: Coincident(g28,g-3)
    c: Coincident(g25,g-6)
    c: Coincident(g26,g-5)
    c: Coincident(g24,g-7)
    c: Parallel(g20,g-21)
    c: Equal(g20,g-21)
    c: Parallel(g21,g-19)
    c: Equal(g21,g-19)
    c: Distance(g29) = 0.2
    c: Distance(g30) = 0.2
    c: Parallel(g29,g-20)
    c: Parallel(g31,g-20)
    c: Equal(g31,g-20)
    c: Coincident(g30,g31)
    c: Coincident(g31,g29)
    c: Coincident(g29,g-21)
    c: Parallel(g30,g31)
    c: Coincident(g17,g30)
    c: Coincident(g20,g29)
    c: Coincident(g21,g30)
    c: Perpendicular(g16,g17)
    c: Coincident(g32,g21)
    c: Coincident(g32,g20)
    c: Perpendicular(g10,g7)
    c: Horizontal(g33)
    c: Symmetric(g-24,g-24,g33)
    c: PointOnObject(g33,g-28)
    c: Symmetric(g-24,g-24,g34)
    c: DistanceY(g35,g35) = 25
    c: Symmetric(g35,g35,g33)
    c: Distance(g36) = 41
    c: Coincident(g36,g35)
    c: Horizontal(g36)
    c: Coincident(g37,g35)
    c: Horizontal(g37)
    c: Coincident(g38,g36)
    c: Vertical(g38)
    c: Coincident(g37,g38)
    c: Diameter(g39) = 6.8
    c: Diameter(g40) = 6.8
    c: Tangent(g39,g36)
    c: Tangent(g40,g37)
    c: Tangent(g39,g35)
    c: Tangent(g40,g35)
    c: Diameter(g41) = 6.8
    c: Diameter(g42) = 6.8
    c: Tangent(g41,g36)
    c: Tangent(g42,g37)
    c: DistanceX(g41,g39) = 24.6
    c: DistanceX(g42,g40) = 24.6
    c: Distance(g43) = 11.2
    c: Coincident(g43,g33)
    c: PointOnObject(g43,g33)
    c: PointOnObject(g43,g35)
    c: Distance(g44) = 21
    c: Coincident(g44,g43)
    c: PointOnObject(g44,g33)
    c: Coincident(g45,g46)
    c: Coincident(g46,g47)
    c: Coincident(g47,g48)
    c: Coincident(g48,g45)
    c: Horizontal(g45)
    c: Horizontal(g47)
    c: Vertical(g46)
    c: Vertical(g48)
    c: Symmetric(g47,g45,g49)
    c: Distance(g46,g48) = 10.6
    c: Distance(g45,g47) = 10
    c: Coincident(g49,g44)
    c: Diameter(g50) = 5.6
    c: Coincident(g50,g44)
    c: Distance(g51) = 11
    c: Symmetric(g51,g51,g33)
    c: DistanceX(g51,g43) = 9
    c: Diameter(g52) = 6
    c: Coincident(g52,g51)
    c: Diameter(g53) = 6
    c: Coincident(g53,g51)
    c: Coincident(g40,g55)
    c: Coincident(g39,g54)
    c: Coincident(g41,g57)
    c: Coincident(g42,g56)
    c: Diameter(g58) = 3
    c: Diameter(g59) = 3
    c: Diameter(g60) = 3
    c: Coincident(g58,g-44)
    c: Coincident(g59,g-46)
    c: Coincident(g60,g-45)
FEATURE [Sketcher::SketchObject] Sketch078
  ArcFitTolerance = 1e-06
  AttachmentSupport = -> [XZ_Plane005]
  FullyConstrained = true
  MakeInternals = false
  MapMode = 5
  Placement = pos=(0,0,0) rot=(1,0,0;1.5708rad)
  sketch-geometry (5):
    g0: LineSegment [constr] StartX=0 StartY=5.5 StartZ=0 EndX=0 EndY=-5.5 EndZ=0
    g1: ArcOfCircle CenterX=0 CenterY=5.5 CenterZ=0 NormalX=0 NormalY=0 NormalZ=1 AngleXU=0 Radius=2.7 StartAngle=0 EndAngle=3.14159
    g2: ArcOfCircle CenterX=0 CenterY=-5.5 CenterZ=0 NormalX=0 NormalY=0 NormalZ=1 AngleXU=0 Radius=2.7 StartAngle=3.1416 EndAngle=6.28318
    g3: LineSegment StartX=-2.7 StartY=5.5 StartZ=0 EndX=-2.7 EndY=-5.50001 EndZ=0
    g4: LineSegment StartX=2.7 StartY=5.5 StartZ=0 EndX=2.7 EndY=-5.50001 EndZ=0
  constraints (13):
    c: Distance(g0) = 11
    c: Vertical(g0)
    c: Symmetric(g0,g0,g-1)
    c: Radius(g1) = 2.7
    c: Coincident(g1,g0)
    c: Radius(g2) = 2.7
    c: Coincident(g2,g0)
    c: Vertical(g3)
    c: Vertical(g4)
    c: Coincident(g2,g4)
    c: Coincident(g2,g3)
    c: Tangent(g3,g1) = -1.5708
    c: Tangent(g4,g1) = 1.5708
FEATURE [PartDesign::Pad] Pad002
  Direction = (0,-1,2e-16)
  Length = 0.8
  Length2 = 10
  Placement = pos=(0,0,0) rot=(1,0,0;1.5708rad)
  Profile = -> Sketch078
  ReferenceAxis = -> Sketch078 [N_Axis]
  Refine = true
  Suppressed = false
  Type = 0
FEATURE [Sketcher::SketchObject] Sketch079
  ArcFitTolerance = 1e-06
  AttachmentSupport = -> [XZ_Plane005]
  ExternalGeometry = -> [Sketch078]
  FullyConstrained = true
  MakeInternals = false
  MapMode = 5
  Placement = pos=(0,0,0) rot=(1,0,0;1.5708rad)
  sketch-geometry (2):
    g0: Circle CenterX=-1e-16 CenterY=5.5 CenterZ=0 NormalX=0 NormalY=0 NormalZ=1 AngleXU=0 Radius=2.7
    g1: Circle CenterX=0 CenterY=-5.5 CenterZ=0 NormalX=0 NormalY=0 NormalZ=1 AngleXU=0 Radius=2.7
  constraints (4):
    c: Coincident(g0,g-3)
    c: PointOnObject(g-3,g0)
    c: Coincident(g1,g-4)
    c: Equal(g1,g-4)
FEATURE [PartDesign::Pad] Pad003
  BaseFeature = -> Pad002
  Direction = (0,-1,2e-16)
  Length = 5
  Length2 = 10
  Placement = pos=(0,0,0) rot=(1,0,0;1.5708rad)
  Profile = -> Sketch079
  ReferenceAxis = -> Sketch079 [N_Axis]
  Refine = true
  Suppressed = false
  Type = 0
FEATURE [PartDesign::Fillet] Fillet001
  Base = -> Pad003 [Edge16,Edge14]
  BaseFeature = -> Pad003
  Placement = pos=(0,0,0) rot=(1,0,0;1.5708rad)
  Radius = 0.4
  Refine = true
  SupportTransform = false
  Suppressed = false
  UseAllEdges = false
FEATURE [PartDesign::Body] Body005  label="pulsanti lato destro"
  AllowCompound = false
  Group = -> [Sketch078,Pad002,Sketch079,Pad003,Fillet001]
  Origin = -> Origin005
  Tip = -> Fillet001
FEATURE [PartDesign::SubShapeBinder] Binder
  BindCopyOnChange = 0
  BindMode = 0
  ClaimChildren = false
  Context = -> Body006 [Binder.]
  Fuse = false
  MakeFace = true
  OffsetFill = false
  OffsetIntersection = false
  OffsetJoinType = 0
  OffsetOpenResult = false
  PartialLoad = false
  Refine = true
  Relative = true
  Support = -> [Body[Sketch074.]]
  _Version = 2
FEATURE [PartDesign::SubShapeBinder] Binder001
  BindCopyOnChange = 0
  BindMode = 0
  ClaimChildren = false
  Context = -> Body007 [Binder001.]
  Fuse = false
  MakeFace = true
  OffsetFill = false
  OffsetIntersection = false
  OffsetJoinType = 0
  OffsetOpenResult = false
  PartialLoad = false
  Refine = true
  Relative = true
  Support = -> [Body[Sketch075.]]
  _Version = 2
FEATURE [Mesh::Feature] logo_per_PCB_definitivo_positivo
  Placement = pos=(-191,17,-66) rot=(0,1,1;0rad)
FEATURE [Sketcher::SketchObject] Sketch114  label="Sketch114 - base lato DX"
  ArcFitTolerance = 1e-06
  AttachmentSupport = -> [Binder001]
  ExternalGeometry = -> [Binder001]
  FullyConstrained = true
  MakeInternals = false
  MapMode = 5
  Placement = pos=(0,1e-15,0) rot=(0,0.707107,0.707107;3.14159rad)
  sketch-geometry (30):
    g0: Circle CenterX=5.6 CenterY=34.8 CenterZ=0 NormalX=0 NormalY=0 NormalZ=1 AngleXU=0 Radius=1.8
    g1: Circle CenterX=5.6 CenterY=7.6 CenterZ=0 NormalX=0 NormalY=0 NormalZ=1 AngleXU=0 Radius=1.8
    g2: Circle CenterX=24.2 CenterY=26.7 CenterZ=0 NormalX=0 NormalY=0 NormalZ=1 AngleXU=0 Radius=3
    g3: Circle CenterX=24.2 CenterY=15.7 CenterZ=0 NormalX=0 NormalY=0 NormalZ=1 AngleXU=0 Radius=3
    g4: Circle CenterX=36.2 CenterY=21.2 CenterZ=0 NormalX=0 NormalY=0 NormalZ=1 AngleXU=0 Radius=2.8
    g5: Circle CenterX=78.51 CenterY=34.8 CenterZ=0 NormalX=0 NormalY=0 NormalZ=1 AngleXU=0 Radius=1.8
    g6: Circle CenterX=78.51 CenterY=7.6 CenterZ=0 NormalX=0 NormalY=0 NormalZ=1 AngleXU=0 Radius=1.8
    g7: Circle CenterX=184.08 CenterY=34.8 CenterZ=0 NormalX=0 NormalY=0 NormalZ=1 AngleXU=0 Radius=1.8
    g8: Circle CenterX=213.443 CenterY=-76.8316 CenterZ=0 NormalX=0 NormalY=0 NormalZ=1 AngleXU=0 Radius=1.8
    g9: Circle CenterX=179.305 CenterY=-76.8316 CenterZ=0 NormalX=0 NormalY=0 NormalZ=1 AngleXU=0 Radius=1.8
    g10: ArcOfCircle [constr] CenterX=132.428 CenterY=4 CenterZ=0 NormalX=0 NormalY=0 NormalZ=1 AngleXU=0 Radius=16 StartAngle=0.314159 EndAngle=1.5708
    g11: ArcOfCircle CenterX=107.6 CenterY=4 CenterZ=0 NormalX=0 NormalY=0 NormalZ=1 AngleXU=0 Radius=16 StartAngle=1.5708 EndAngle=3.00366
    g12: ArcOfCircle CenterX=207.583 CenterY=4 CenterZ=0 NormalX=0 NormalY=0 NormalZ=1 AngleXU=0 Radius=17 StartAngle=1.85815 EndAngle=3.57792
    g13: ArcOfCircle CenterX=184.801 CenterY=-67.3089 CenterZ=0 NormalX=0 NormalY=0 NormalZ=1 AngleXU=0 Radius=33.7833 StartAngle=5.88425 EndAngle=6.71952
    g14: LineSegment StartX=0 StartY=39.2 StartZ=0 EndX=0 EndY=3.2 EndZ=0
    g15: LineSegment StartX=0 StartY=3.2 StartZ=0 EndX=82.8 EndY=3.2 EndZ=0
    g16: LineSegment StartX=82.8 StartY=3.2 StartZ=0 EndX=82.8 EndY=6.2 EndZ=0
    g17: LineSegment StartX=82.8 StartY=6.2 StartZ=0 EndX=91.752 EndY=6.2 EndZ=0
    g18: LineSegment StartX=107.6 StartY=20 StartZ=0 EndX=132.428 EndY=20 EndZ=0
    g19: LineSegment StartX=147.645 StartY=8.94427 StartZ=0 EndX=176.685 EndY=-80.4316 EndZ=0
    g20: LineSegment StartX=176.685 StartY=-80.4316 StartZ=0 EndX=215.932 EndY=-80.4316 EndZ=0
    g21: LineSegment StartX=215.42 StartY=-53.0314 StartZ=0 EndX=192.176 EndY=-3.18451 EndZ=0
    g22: LineSegment StartX=202.765 StartY=20.303 StartZ=0 EndX=195.887 EndY=39.2 EndZ=0
    g23: LineSegment StartX=195.887 StartY=39.2 StartZ=0 EndX=0 EndY=39.2 EndZ=0
    g24: LineSegment StartX=196.467 StartY=26.4942 StartZ=0 EndX=194.073 EndY=33.0721 EndZ=0
    g25: LineSegment StartX=194.073 StartY=33.0721 StartZ=0 EndX=189.939 EndY=31.5672 EndZ=0
    g26: LineSegment StartX=189.939 StartY=31.5672 StartZ=0 EndX=192.333 EndY=24.9893 EndZ=0
    g27: LineSegment StartX=192.333 StartY=24.9893 StartZ=0 EndX=196.467 EndY=26.4942 EndZ=0
    g28: LineSegment StartX=132.428 StartY=20 StartZ=0 EndX=144.053 EndY=20 EndZ=0
    g29: LineSegment StartX=144.053 StartY=20 StartZ=0 EndX=147.645 EndY=8.94427 EndZ=0
  constraints (65):
    c: Equal(g0,g-25)
    c: Equal(g2,g-29)
    c: Equal(g3,g-30)
    c: Equal(g4,g-28)
    c: Equal(g1,g-26)
    c: Coincident(g0,g-25)
    c: Coincident(g1,g-26)
    c: Coincident(g2,g-29)
    c: Coincident(g3,g-30)
    c: Coincident(g4,g-28)
    c: Equal(g5,g-23)
    c: Equal(g6,g-24)
    c: Coincident(g5,g-23)
    c: Coincident(g6,g-24)
    c: Equal(g7,g-20)
    c: Coincident(g7,g-20)
    c: Equal(g9,g-22)
    c: Coincident(g9,g-22)
    c: Equal(g8,g-21)
    c: Coincident(g8,g-21)
    c: Equal(g13,g-12)
    c: Equal(g12,g-14)
    c: Equal(g10,g-9)
    c: Equal(g11,g-7)
    c: Coincident(g14,g-27)
    c: Coincident(g14,g-27)
    c: Coincident(g15,g14)
    c: Coincident(g15,g-5)
    c: Coincident(g16,g15)
    c: Coincident(g16,g-6)
    c: Coincident(g17,g16)
    c: Coincident(g17,g-7)
    c: Coincident(g11,g17)
    c: Coincident(g11,g-8)
    c: Coincident(g18,g11)
    c: Coincident(g18,g-9)
    c: Coincident(g10,g18)
    c: Coincident(g10,g-10)
    c: Coincident(g19,g10)
    c: Coincident(g19,g-11)
    c: Coincident(g20,g19)
    c: Coincident(g20,g-12)
    c: Coincident(g13,g20)
    c: Coincident(g13,g-13)
    c: Coincident(g21,g13)
    c: Coincident(g21,g-14)
    c: Coincident(g12,g21)
    c: Coincident(g12,g-15)
    c: Coincident(g22,g12)
    c: Coincident(g22,g-15)
    c: Coincident(g23,g22)
    c: Coincident(g23,g14)
    c: Coincident(g24,g-18)
    c: Coincident(g24,g-16)
    c: Coincident(g25,g24)
    c: Coincident(g25,g-19)
    c: Coincident(g26,g25)
    c: Coincident(g26,g-19)
    c: Coincident(g27,g26)
    c: Coincident(g27,g24)
    c: Coincident(g29,g10)
    c: Coincident(g28,g10)
    c: Coincident(g29,g28)
    c: Parallel(g28,g18)
    c: Parallel(g29,g19)
FEATURE [PartDesign::Pad] Pad011
  Direction = (0,1,-2e-16)
  Length = 2
  Length2 = 10
  Profile = -> Sketch114
  ReferenceAxis = -> Sketch114 [N_Axis]
  Refine = true
  Reversed = true
  Suppressed = false
  Type = 0
FEATURE [Sketcher::SketchObject] Sketch115
  ArcFitTolerance = 1e-06
  AttachmentSupport = -> [Pad011]
  ExternalGeometry = -> [Binder001]
  FullyConstrained = true
  MakeInternals = false
  MapMode = 5
  Placement = pos=(0,1.7e-15,0) rot=(0,0.707107,0.707107;3.14159rad)
  sketch-geometry (4):
    g0: ArcOfCircle CenterX=24.2 CenterY=26.7 CenterZ=0 NormalX=0 NormalY=0 NormalZ=1 AngleXU=0 Radius=3 StartAngle=4.48384e-08 EndAngle=3.14159
    g1: ArcOfCircle CenterX=24.2 CenterY=15.7 CenterZ=0 NormalX=0 NormalY=0 NormalZ=1 AngleXU=0 Radius=3 StartAngle=3.14159 EndAngle=6.28318
    g2: LineSegment StartX=21.2 StartY=26.7 StartZ=0 EndX=21.2 EndY=15.7 EndZ=0
    g3: LineSegment StartX=27.2 StartY=26.7 StartZ=0 EndX=27.2 EndY=15.7 EndZ=0
  constraints (12):
    c: Equal(g1,g-4)
    c: Equal(g0,g-3)
    c: Coincident(g0,g-3)
    c: Coincident(g1,g-4)
    c: Vertical(g2)
    c: Vertical(g3)
    c: Tangent(g3,g-3)
    c: Tangent(g2,g-3)
    c: Coincident(g0,g2)
    c: Coincident(g0,g3)
    c: Coincident(g1,g2)
    c: Coincident(g3,g1)
FEATURE [Sketcher::SketchObject] Sketch117  label="Sketch117 - fori per inserto M3 x 3 x 4.5"
  ArcFitTolerance = 1e-06
  AttachmentSupport = -> [Pad011]
  ExternalGeometry = -> [Binder001]
  FullyConstrained = true
  MakeInternals = false
  MapMode = 5
  Placement = pos=(0,1.7e-15,0) rot=(0,0.707107,0.707107;3.14159rad)
  sketch-geometry (4):
    g0: Circle CenterX=43.2 CenterY=30.3 CenterZ=0 NormalX=0 NormalY=0 NormalZ=1 AngleXU=0 Radius=2.25
    g1: Circle CenterX=43.2 CenterY=12.1 CenterZ=0 NormalX=0 NormalY=0 NormalZ=1 AngleXU=0 Radius=2.25
    g2: Circle CenterX=18.6 CenterY=30.3 CenterZ=0 NormalX=0 NormalY=0 NormalZ=1 AngleXU=0 Radius=2.25
    g3: Circle CenterX=18.6 CenterY=12.1 CenterZ=0 NormalX=0 NormalY=0 NormalZ=1 AngleXU=0 Radius=2.25
  constraints (8):
    c: Diameter(g0) = 4.5
    c: Diameter(g1) = 4.5
    c: Diameter(g2) = 4.5
    c: Diameter(g3) = 4.5
    c: Coincident(g2,g-3)
    c: Coincident(g3,g-6)
    c: Coincident(g0,g-4)
    c: Coincident(g1,g-5)
FEATURE [Sketcher::SketchObject] Sketch118
  ArcFitTolerance = 1e-06
  AttachmentSupport = -> [Pad011]
  ExternalGeometry = -> [Binder001]
  FullyConstrained = true
  MakeInternals = false
  MapMode = 5
  Placement = pos=(0,-2,0) rot=(1,0,0;1.5708rad)
  sketch-geometry (12):
    g0: Circle CenterX=-78.51 CenterY=34.8 CenterZ=0 NormalX=0 NormalY=0 NormalZ=1 AngleXU=0 Radius=1.8
    g1: Circle CenterX=-78.51 CenterY=7.6 CenterZ=0 NormalX=0 NormalY=0 NormalZ=1 AngleXU=0 Radius=1.8
    g2: Circle CenterX=-5.6 CenterY=34.8 CenterZ=0 NormalX=0 NormalY=0 NormalZ=1 AngleXU=0 Radius=1.8
    g3: Circle CenterX=-5.6 CenterY=7.6 CenterZ=0 NormalX=0 NormalY=0 NormalZ=1 AngleXU=0 Radius=1.8
    g4: LineSegment StartX=0 StartY=39.2 StartZ=0 EndX=0 EndY=3.2 EndZ=0
    g5: LineSegment StartX=0 StartY=3.2 StartZ=0 EndX=-82.8 EndY=3.2 EndZ=0
    g6: LineSegment StartX=-82.8 StartY=3.2 StartZ=0 EndX=-82.8 EndY=39.2 EndZ=0
    g7: LineSegment StartX=-82.8 StartY=39.2 StartZ=0 EndX=0 EndY=39.2 EndZ=0
    g8: ArcOfCircle CenterX=-65 CenterY=21.2 CenterZ=0 NormalX=0 NormalY=0 NormalZ=1 AngleXU=0 Radius=10 StartAngle=1.5708 EndAngle=4.71239
    g9: ArcOfCircle CenterX=-19 CenterY=21.2 CenterZ=0 NormalX=0 NormalY=0 NormalZ=1 AngleXU=0 Radius=10 StartAngle=4.71239 EndAngle=7.85398
    g10: LineSegment StartX=-65 StartY=31.2 StartZ=0 EndX=-19 EndY=31.2 EndZ=0
    g11: LineSegment StartX=-65 StartY=11.2 StartZ=0 EndX=-19 EndY=11.2 EndZ=0
  constraints (25):
    c: Equal(g2,g-5)
    c: Equal(g3,g-7)
    c: Equal(g1,g-6)
    c: Equal(g0,g-4)
    c: Coincident(g0,g-4)
    c: Coincident(g1,g-6)
    c: Coincident(g3,g-7)
    c: Coincident(g2,g-5)
    c: Coincident(g4,g-8)
    c: Coincident(g4,g-9)
    c: Coincident(g5,g4)
    c: Coincident(g5,g-10)
    c: Coincident(g6,g5)
    c: PointOnObject(g6,g-3)
    c: Vertical(g6)
    c: Coincident(g7,g6)
    c: Coincident(g7,g4)
    c: Tangent(g8,g10) = 1.5708
    c: Tangent(g8,g11) = -1.5708
    c: Tangent(g9,g10) = 1.5708
    c: Tangent(g9,g11) = -1.5708
    c: Equal(g8,g9)
    c: Radius(g8) = 10
    c: Coincident(g8,g-11)
    c: Coincident(g9,g-12)
FEATURE [Sketcher::SketchObject] Sketch120
  ArcFitTolerance = 1e-06
  AttachmentSupport = -> [Pad011]
  ExternalGeometry = -> [Binder001]
  FullyConstrained = true
  MakeInternals = false
  MapMode = 5
  Placement = pos=(0,-2,0) rot=(1,0,0;1.5708rad)
  sketch-geometry (4):
    g0: LineSegment StartX=-137.815 StartY=39.2 StartZ=0 EndX=-142.655 EndY=24.303 EndZ=0
    g1: LineSegment StartX=-137.815 StartY=39.2 StartZ=0 EndX=-110.815 EndY=39.2 EndZ=0
    g2: LineSegment StartX=-142.655 StartY=24.303 StartZ=0 EndX=-110.815 EndY=24.303 EndZ=0
    g3: ArcOfCircle CenterX=-92.2534 CenterY=31.7515 CenterZ=0 NormalX=0 NormalY=0 NormalZ=1 AngleXU=0 Radius=20 StartAngle=2.75997 EndAngle=3.52321
  constraints (12):
    c: PointOnObject(g0,g-3)
    c: Coincident(g1,g0)
    c: PointOnObject(g1,g-3)
    c: Coincident(g2,g0)
    c: Horizontal(g2)
    c: Tangent(g0,g-4)
    c: Vertical(g2,g1)
    c: DistanceX(g1,g1) = 27
    c: DistanceY(g-6,g0) = 4
    c: Radius(g3) = 20
    c: Coincident(g3,g1)
    c: Coincident(g3,g2)
FEATURE [Sketcher::SketchObject] Sketch121
  ArcFitTolerance = 1e-06
  AttachmentSupport = -> [Pad011]
  ExternalGeometry = -> [Binder001]
  FullyConstrained = true
  MakeInternals = false
  MapMode = 5
  Placement = pos=(0,-2,0) rot=(1,0,0;1.5708rad)
  sketch-geometry (15):
    g0: LineSegment StartX=-137.815 StartY=39.2 StartZ=0 EndX=-143.955 EndY=20.303 EndZ=0
    g1: LineSegment StartX=-143.955 StartY=20.303 StartZ=0 EndX=-190.141 EndY=20.303 EndZ=0
    g2: LineSegment StartX=-190.141 StartY=20.303 StartZ=0 EndX=-186.139 EndY=31.3 EndZ=0
    g3: LineSegment StartX=-178.754 StartY=39.2 StartZ=0 EndX=-180.791 EndY=33.6029 EndZ=0
    g4: ArcOfCircle CenterX=-184.08 CenterY=34.8 CenterZ=0 NormalX=0 NormalY=0 NormalZ=1 AngleXU=0 Radius=3.5 StartAngle=4.71239 EndAngle=5.93412
    g5: LineSegment StartX=-184.08 StartY=31.3 StartZ=0 EndX=-186.139 EndY=31.3 EndZ=0
    g6: LineSegment StartX=-137.815 StartY=39.2 StartZ=0 EndX=-156.815 EndY=39.2 EndZ=0
    g7: LineSegment StartX=-168.815 StartY=39.2 StartZ=0 EndX=-178.754 EndY=39.2 EndZ=0
    g8: LineSegment StartX=-157.815 StartY=39.2 StartZ=0 EndX=-167.815 EndY=39.2 EndZ=0
    g9: LineSegment StartX=-168.815 StartY=31.2 StartZ=0 EndX=-156.815 EndY=31.2 EndZ=0
    g10: LineSegment StartX=-167.436 StartY=36.2 StartZ=0 EndX=-157.436 EndY=36.2 EndZ=0
    g11: ArcOfCircle CenterX=-176.411 CenterY=35.2 CenterZ=0 NormalX=0 NormalY=0 NormalZ=1 AngleXU=0 Radius=20 StartAngle=6.08183 EndAngle=6.48454
    g12: ArcOfCircle CenterX=-188.411 CenterY=35.2 CenterZ=0 NormalX=0 NormalY=0 NormalZ=1 AngleXU=0 Radius=20 StartAngle=6.08183 EndAngle=6.48454
    g13: ArcOfCircle CenterX=-177.411 CenterY=35.2 CenterZ=0 NormalX=0 NormalY=0 NormalZ=1 AngleXU=0 Radius=20 StartAngle=0.0500209 EndAngle=0.201358
    g14: ArcOfCircle CenterX=-187.411 CenterY=35.2 CenterZ=0 NormalX=0 NormalY=0 NormalZ=1 AngleXU=0 Radius=20 StartAngle=0.0500209 EndAngle=0.201358
  constraints (46):
    c: PointOnObject(g0,g-3)
    c: Tangent(g0,g-5)
    c: Coincident(g1,g0)
    c: Horizontal(g1)
    c: Coincident(g2,g1)
    c: PointOnObject(g3,g-3)
    c: Parallel(g3,g-6)
    c: Parallel(g2,g-6)
    c: Radius(g4) = 3.5
    c: Coincident(g4,g-7)
    c: Tangent(g3,g4) = 1.5708
    c: Horizontal(g5)
    c: Tangent(g5,g4) = 1.5708
    c: DistanceX(g-8,g5) = 3.8
    c: Coincident(g2,g5)
    c: Coincident(g6,g0)
    c: PointOnObject(g6,g-3)
    c: DistanceX(g6,g6) = 19
    c: PointOnObject(g7,g-3)
    c: DistanceX(g7,g6) = 12
    c: Coincident(g7,g3)
    c: PointOnObject(g8,g-3)
    c: PointOnObject(g8,g-3)
    c: DistanceX(g8,g8) = 10
    c: DistanceX(g8,g6) = 1
    c: Horizontal(g9)
    c: Vertical(g7,g9)
    c: Vertical(g6,g9)
    c: DistanceY(g9,g7) = 8
    c: Horizontal(g10)
    c: Equal(g8,g10)
    c: DistanceY(g10,g8) = 3
    c: Radius(g11) = 20
    c: Coincident(g11,g6)
    c: Coincident(g11,g9)
    c: Radius(g12) = 20
    c: Coincident(g12,g7)
    c: Coincident(g12,g9)
    c: Equal(g13,g11)
    c: Coincident(g13,g8)
    c: Coincident(g13,g10)
    c: Horizontal(g13,g11)
    c: Equal(g14,g12)
    c: Coincident(g14,g8)
    c: Coincident(g14,g10)
    c: Horizontal(g1,g-6)
FEATURE [Sketcher::SketchObject] Sketch122
  ArcFitTolerance = 1e-06
  AttachmentSupport = -> [Pad011]
  ExternalGeometry = -> [Binder001]
  FullyConstrained = true
  MakeInternals = false
  MapMode = 5
  Placement = pos=(0,-2,0) rot=(1,0,0;1.5708rad)
  sketch-geometry (8):
    g0: LineSegment StartX=-202.765 StartY=20.303 StartZ=0 EndX=-143.955 EndY=20.303 EndZ=0
    g1: ArcOfCircle CenterX=-184.801 CenterY=-67.3089 CenterZ=0 NormalX=0 NormalY=0 NormalZ=1 AngleXU=0 Radius=33.7833 StartAngle=2.70526 EndAngle=3.54053
    g2: LineSegment StartX=-176.685 StartY=-80.4316 StartZ=0 EndX=-215.932 EndY=-80.4316 EndZ=0
    g3: LineSegment StartX=-215.42 StartY=-53.0315 StartZ=0 EndX=-192.176 EndY=-3.18454 EndZ=0
    g4: ArcOfCircle CenterX=-207.583 CenterY=4 CenterZ=0 NormalX=0 NormalY=0 NormalZ=1 AngleXU=0 Radius=17 StartAngle=5.84685 EndAngle=7.56663
    g5: Circle CenterX=-213.443 CenterY=-76.8316 CenterZ=0 NormalX=0 NormalY=0 NormalZ=1 AngleXU=0 Radius=3
    g6: Circle CenterX=-179.305 CenterY=-76.8316 CenterZ=0 NormalX=0 NormalY=0 NormalZ=1 AngleXU=0 Radius=3
    g7: LineSegment StartX=-143.955 StartY=20.303 StartZ=0 EndX=-176.685 EndY=-80.4316 EndZ=0
  constraints (18):
    c: Coincident(g0,g-6)
    c: Coincident(g1,g-7)
    c: Coincident(g1,g-8)
    c: Coincident(g2,g1)
    c: Tangent(g3,g-5)
    c: Coincident(g4,g-6)
    c: Coincident(g4,g0)
    c: Coincident(g3,g4)
    c: Coincident(g1,g3)
    c: Diameter(g5) = 6
    c: Diameter(g6) = 6
    c: Coincident(g5,g-9)
    c: Coincident(g6,g-10)
    c: Horizontal(g0)
    c: Horizontal(g2)
    c: Coincident(g7,g0)
    c: Coincident(g7,g2)
    c: Tangent(g7,g-4)
FEATURE [Sketcher::SketchObject] Sketch123
  ArcFitTolerance = 1e-06
  AttachmentSupport = -> [Pad011]
  ExternalGeometry = -> [Binder001]
  FullyConstrained = true
  MakeInternals = false
  MapMode = 5
  Placement = pos=(0,-2,0) rot=(1,0,0;1.5708rad)
  sketch-geometry (4):
    g0: LineSegment StartX=-108 StartY=36.8 StartZ=0 EndX=-90 EndY=36.8 EndZ=0
    g1: LineSegment StartX=-108 StartY=36.8 StartZ=0 EndX=-108 EndY=26.8 EndZ=0
    g2: LineSegment StartX=-108 StartY=26.8 StartZ=0 EndX=-90 EndY=26.8 EndZ=0
    g3: ArcOfCircle CenterX=-94 CenterY=31.8 CenterZ=0 NormalX=0 NormalY=0 NormalZ=1 AngleXU=0 Radius=6.40312 StartAngle=5.38713 EndAngle=7.17924
  constraints (13):
    c: Horizontal(g0)
    c: Coincident(g1,g0)
    c: Vertical(g1)
    c: Coincident(g2,g1)
    c: Horizontal(g2)
    c: DistanceX(g0,g0) = 18
    c: DistanceY(g1,g1) = 10
    c: Equal(g0,g2)
    c: DistanceX(g0,g-3) = 90
    c: DistanceY(g0,g-3) = 2.4
    c: Coincident(g3,g0)
    c: Coincident(g3,g2)
    c: DistanceX(g3,g0) = 4
FEATURE [PartDesign::Chamfer] Chamfer014
  Angle = 45
  Base = -> Pad011 [Edge80,Edge4,Edge7]
  BaseFeature = -> Pad011
  ChamferType = 0
  FlipDirection = false
  Refine = true
  Size = 1.9
  Size2 = 1
  SupportTransform = false
  Suppressed = false
  UseAllEdges = false
FEATURE [PartDesign::Pocket] Pocket006
  BaseFeature = -> Chamfer014
  Direction = (0,-1,2e-16)
  Length = 1.2
  Length2 = 5
  Profile = -> Sketch115
  ReferenceAxis = -> Sketch115 [N_Axis]
  Refine = true
  Suppressed = false
  Type = 0
FEATURE [Sketcher::SketchObject] Sketch116  label="Sketch116 - pieno per inserto M3 x 3 x 4,5"
  ArcFitTolerance = 1e-06
  AttachmentSupport = -> [Pocket006]
  ExternalGeometry = -> [Binder001]
  FullyConstrained = true
  MakeInternals = false
  MapMode = 5
  Placement = pos=(0,1.7e-15,0) rot=(0,0.707107,0.707107;3.14159rad)
  sketch-geometry (4):
    g0: Circle CenterX=43.2 CenterY=30.3 CenterZ=0 NormalX=0 NormalY=0 NormalZ=1 AngleXU=0 Radius=3.4
    g1: Circle CenterX=43.2 CenterY=12.1 CenterZ=0 NormalX=0 NormalY=0 NormalZ=1 AngleXU=0 Radius=3.4
    g2: Circle CenterX=18.6 CenterY=30.3 CenterZ=0 NormalX=0 NormalY=0 NormalZ=1 AngleXU=0 Radius=3.4
    g3: Circle CenterX=18.6 CenterY=12.1 CenterZ=0 NormalX=0 NormalY=0 NormalZ=1 AngleXU=0 Radius=3.4
  constraints (8):
    c: Diameter(g0) = 6.8
    c: Diameter(g1) = 6.8
    c: Diameter(g2) = 6.8
    c: Diameter(g3) = 6.8
    c: Coincident(g2,g-3)
    c: Coincident(g0,g-4)
    c: Coincident(g3,g-6)
    c: Coincident(g1,g-5)
FEATURE [PartDesign::Pad] Pad012
  BaseFeature = -> Pocket006
  Direction = (0,1,-2e-16)
  Length = 2.4
  Length2 = 10
  Profile = -> Sketch116
  ReferenceAxis = -> Sketch116 [N_Axis]
  Refine = true
  Suppressed = false
  Type = 0
FEATURE [PartDesign::Pocket] Pocket007
  BaseFeature = -> Pad012
  Direction = (0,-1,2e-16)
  Length = 0.6
  Length2 = 2.4
  Profile = -> Sketch117
  ReferenceAxis = -> Sketch117 [N_Axis]
  Refine = true
  Suppressed = false
  Type = 4
FEATURE [PartDesign::Pad] Pad013
  BaseFeature = -> Pocket007
  Direction = (0,-1,2e-16)
  Length = 1.6
  Length2 = 10
  Profile = -> Sketch118
  ReferenceAxis = -> Sketch118 [N_Axis]
  Refine = true
  Suppressed = false
  Type = 0
FEATURE [Sketcher::SketchObject] Sketch119
  ArcFitTolerance = 1e-06
  AttachmentSupport = -> [Pad013]
  ExternalGeometry = -> [Binder001]
  FullyConstrained = true
  MakeInternals = false
  MapMode = 5
  Placement = pos=(0,-3.6,0) rot=(1,0,0;1.5708rad)
  sketch-geometry (21):
    g0: LineSegment [constr] StartX=-82.8 StartY=3.2 StartZ=0 EndX=-82.8 EndY=39.2 EndZ=0
    g1: ArcOfCircle CenterX=-78.51 CenterY=34.8 CenterZ=0 NormalX=0 NormalY=0 NormalZ=1 AngleXU=0 Radius=3.5 StartAngle=4.71239 EndAngle=6.28319
    g2: ArcOfCircle CenterX=-78.51 CenterY=7.6 CenterZ=0 NormalX=0 NormalY=0 NormalZ=1 AngleXU=0 Radius=3.5 StartAngle=0 EndAngle=1.5708
    g3: ArcOfCircle CenterX=-5.6 CenterY=34.8 CenterZ=0 NormalX=0 NormalY=0 NormalZ=1 AngleXU=0 Radius=3.5 StartAngle=3.14159 EndAngle=4.71239
    g4: ArcOfCircle CenterX=-5.6 CenterY=7.6 CenterZ=0 NormalX=0 NormalY=0 NormalZ=1 AngleXU=0 Radius=3.5 StartAngle=1.5708 EndAngle=3.14159
    g5: LineSegment StartX=0 StartY=39.2 StartZ=0 EndX=0 EndY=31.3 EndZ=0
    g6: LineSegment StartX=0 StartY=39.2 StartZ=0 EndX=-9.1 EndY=39.2 EndZ=0
    g7: LineSegment StartX=0 StartY=3.2 StartZ=0 EndX=0 EndY=11.1 EndZ=0
    g8: LineSegment StartX=0 StartY=3.2 StartZ=0 EndX=-9.1 EndY=3.2 EndZ=0
    g9: LineSegment StartX=-82.8 StartY=3.2 StartZ=0 EndX=-75.01 EndY=3.2 EndZ=0
    g10: LineSegment StartX=-82.8 StartY=3.2 StartZ=0 EndX=-82.8 EndY=11.1 EndZ=0
    g11: LineSegment StartX=-82.8 StartY=39.2 StartZ=0 EndX=-82.8 EndY=31.3 EndZ=0
    g12: LineSegment StartX=-82.8 StartY=39.2 StartZ=0 EndX=-75.01 EndY=39.2 EndZ=0
    g13: LineSegment StartX=-82.8 StartY=31.3 StartZ=0 EndX=-78.51 EndY=31.3 EndZ=0
    g14: LineSegment StartX=-75.01 StartY=39.2 StartZ=0 EndX=-75.01 EndY=34.8 EndZ=0
    g15: LineSegment StartX=-82.8 StartY=11.1 StartZ=0 EndX=-78.51 EndY=11.1 EndZ=0
    g16: LineSegment StartX=-75.01 StartY=3.2 StartZ=0 EndX=-75.01 EndY=7.6 EndZ=0
    g17: LineSegment StartX=-9.1 StartY=39.2 StartZ=0 EndX=-9.1 EndY=34.8 EndZ=0
    g18: LineSegment StartX=0 StartY=31.3 StartZ=0 EndX=-5.6 EndY=31.3 EndZ=0
    g19: LineSegment StartX=0 StartY=11.1 StartZ=0 EndX=-5.6 EndY=11.1 EndZ=0
    g20: LineSegment StartX=-9.1 StartY=3.2 StartZ=0 EndX=-9.1 EndY=7.6 EndZ=0
  constraints (51):
    c: Coincident(g0,g-10)
    c: PointOnObject(g0,g-8)
    c: Vertical(g0)
    c: Coincident(g1,g-3)
    c: Coincident(g2,g-4)
    c: Coincident(g3,g-5)
    c: Coincident(g4,g-6)
    c: Radius(g4) = 3.5
    c: Radius(g3) = 3.5
    c: Radius(g1) = 3.5
    c: Radius(g2) = 3.5
    c: Coincident(g5,g-9)
    c: PointOnObject(g5,g-9)
    c: Coincident(g6,g5)
    c: PointOnObject(g6,g-8)
    c: Coincident(g7,g-9)
    c: PointOnObject(g7,g-9)
    c: Coincident(g8,g7)
    c: PointOnObject(g8,g-7)
    c: Coincident(g9,g0)
    c: PointOnObject(g9,g-7)
    c: Coincident(g10,g0)
    c: PointOnObject(g10,g0)
    c: Coincident(g11,g0)
    c: PointOnObject(g11,g0)
    c: Coincident(g12,g0)
    c: PointOnObject(g12,g-8)
    c: Coincident(g13,g11)
    c: Horizontal(g13)
    c: Coincident(g14,g12)
    c: Vertical(g14)
    c: Coincident(g15,g10)
    c: Horizontal(g15)
    c: Coincident(g16,g9)
    c: Vertical(g16)
    c: Coincident(g17,g6)
    c: Vertical(g17)
    c: Coincident(g18,g5)
    c: Horizontal(g18)
    c: Coincident(g19,g7)
    c: Horizontal(g19)
    c: Coincident(g20,g8)
    c: Vertical(g20)
    c: Tangent(g20,g4) = 1.5708
    c: Tangent(g4,g19) = -1.5708
    c: Tangent(g18,g3) = 1.5708
    c: Tangent(g3,g17) = -1.5708
    c: Tangent(g13,g1) = -1.5708
    c: Tangent(g1,g14) = 1.5708
    c: Tangent(g16,g2) = -1.5708
    c: Tangent(g2,g15) = 1.5708
FEATURE [PartDesign::Pocket] Pocket008
  BaseFeature = -> Pad013
  Direction = (0,1,-2e-16)
  Length = 1.6
  Length2 = 5
  Profile = -> Sketch119
  ReferenceAxis = -> Sketch119 [N_Axis]
  Refine = true
  Suppressed = false
  Type = 0
FEATURE [PartDesign::Pad] Pad017
  BaseFeature = -> Pocket008
  Direction = (0,-1,2e-16)
  Length = 1.6
  Length2 = 10
  Profile = -> Sketch123
  ReferenceAxis = -> Sketch123 [N_Axis]
  Refine = true
  Suppressed = false
  Type = 0
FEATURE [Sketcher::SketchObject] Sketch125
  ArcFitTolerance = 1e-06
  AttachmentSupport = -> [Pad017]
  ExternalGeometry = -> [Pad017]
  FullyConstrained = true
  MakeInternals = false
  MapMode = 5
  Placement = pos=(0,-3.6,8e-16) rot=(1,0,0;1.5708rad)
  sketch-geometry (20):
    g0: LineSegment StartX=-108 StartY=35.8 StartZ=0 EndX=-108 EndY=35 EndZ=0
    g1: LineSegment StartX=-108 StartY=35 StartZ=0 EndX=-97 EndY=35 EndZ=0
    g2: LineSegment StartX=-97 StartY=35 StartZ=0 EndX=-97 EndY=35.8 EndZ=0
    g3: LineSegment StartX=-97 StartY=35.8 StartZ=0 EndX=-108 EndY=35.8 EndZ=0
    g4: LineSegment StartX=-108 StartY=28.6 StartZ=0 EndX=-108 EndY=27.8 EndZ=0
    g5: LineSegment StartX=-108 StartY=27.8 StartZ=0 EndX=-97 EndY=27.8 EndZ=0
    g6: LineSegment StartX=-97 StartY=27.8 StartZ=0 EndX=-97 EndY=28.6 EndZ=0
    g7: LineSegment StartX=-97 StartY=28.6 StartZ=0 EndX=-108 EndY=28.6 EndZ=0
    g8: LineSegment StartX=-108 StartY=30.4 StartZ=0 EndX=-108 EndY=29.6 EndZ=0
    g9: LineSegment StartX=-108 StartY=29.6 StartZ=0 EndX=-97 EndY=29.6 EndZ=0
    g10: LineSegment StartX=-97 StartY=29.6 StartZ=0 EndX=-97 EndY=30.4 EndZ=0
    g11: LineSegment StartX=-97 StartY=30.4 StartZ=0 EndX=-108 EndY=30.4 EndZ=0
    g12: LineSegment StartX=-108 StartY=32.2 StartZ=0 EndX=-108 EndY=31.4 EndZ=0
    g13: LineSegment StartX=-108 StartY=31.4 StartZ=0 EndX=-97 EndY=31.4 EndZ=0
    g14: LineSegment StartX=-97 StartY=31.4 StartZ=0 EndX=-97 EndY=32.2 EndZ=0
    g15: LineSegment StartX=-97 StartY=32.2 StartZ=0 EndX=-108 EndY=32.2 EndZ=0
    g16: LineSegment StartX=-108 StartY=34 StartZ=0 EndX=-108 EndY=33.2 EndZ=0
    g17: LineSegment StartX=-108 StartY=33.2 StartZ=0 EndX=-97 EndY=33.2 EndZ=0
    g18: LineSegment StartX=-97 StartY=33.2 StartZ=0 EndX=-97 EndY=34 EndZ=0
    g19: LineSegment StartX=-97 StartY=34 StartZ=0 EndX=-108 EndY=34 EndZ=0
  constraints (55):
    c: Coincident(g1,g0)
    c: Horizontal(g1)
    c: Coincident(g2,g1)
    c: Vertical(g2)
    c: Coincident(g3,g2)
    c: Horizontal(g3)
    c: Coincident(g3,g0)
    c: DistanceX(g1,g1) = 11
    c: DistanceY(g2,g2) = 0.8
    c: Coincident(g5,g4)
    c: Horizontal(g5)
    c: Coincident(g6,g5)
    c: Vertical(g6)
    c: Coincident(g7,g6)
    c: Horizontal(g7)
    c: Coincident(g7,g4)
    c: Coincident(g9,g8)
    c: Horizontal(g9)
    c: Coincident(g10,g9)
    c: Vertical(g10)
    c: Coincident(g11,g10)
    c: Horizontal(g11)
    c: Coincident(g11,g8)
    c: Coincident(g13,g12)
    c: Horizontal(g13)
    c: Coincident(g14,g13)
    c: Vertical(g14)
    c: Coincident(g15,g14)
    c: Horizontal(g15)
    c: Coincident(g15,g12)
    c: Coincident(g17,g16)
    c: Horizontal(g17)
    c: Coincident(g18,g17)
    c: Vertical(g18)
    c: Coincident(g19,g18)
    c: Horizontal(g19)
    c: Coincident(g19,g16)
    c: Equal(g3,g19)
    c: Equal(g3,g15)
    c: Equal(g3,g11)
    c: Equal(g3,g7)
    c: Equal(g2,g18)
    c: Equal(g2,g14)
    c: Equal(g2,g10)
    c: Equal(g2,g6)
    c: DistanceY(g-4,g4) = 1
    c: DistanceY(g4,g8) = 1
    c: DistanceY(g8,g12) = 1
    c: DistanceY(g12,g16) = 1
    c: DistanceY(g16,g0) = 1
    c: Tangent(g0,g-5)
    c: Tangent(g16,g-5)
    c: Tangent(g12,g-5)
    c: Tangent(g8,g-5)
    c: Tangent(g4,g-5)
FEATURE [PartDesign::Chamfer] Chamfer009
  Angle = 45
  Base = -> Pad017 [Edge151,Edge154]
  BaseFeature = -> Pad017
  ChamferType = 1
  FlipDirection = false
  Refine = true
  Size = 1.5
  Size2 = 2.8
  SupportTransform = false
  Suppressed = false
  UseAllEdges = false
FEATURE [PartDesign::Pocket] Pocket009
  BaseFeature = -> Chamfer009
  Direction = (0,1,-2e-16)
  Length = 1
  Length2 = 5
  Profile = -> Sketch125
  ReferenceAxis = -> Sketch125 [N_Axis]
  Refine = true
  Suppressed = false
  Type = 0
FEATURE [PartDesign::Pad] Pad014
  BaseFeature = -> Pocket009
  Direction = (0,-1,2e-16)
  Length = 0.8
  Length2 = 10
  Profile = -> Sketch120
  ReferenceAxis = -> Sketch120 [N_Axis]
  Refine = true
  Suppressed = false
  Type = 0
FEATURE [Sketcher::SketchObject] Sketch124
  ArcFitTolerance = 1e-06
  AttachmentSupport = -> [Pad014]
  ExternalGeometry = -> [Binder001]
  FullyConstrained = true
  MakeInternals = false
  MapMode = 5
  Placement = pos=(0,-2.8,6e-16) rot=(1,0,0;1.5708rad)
  sketch-geometry (4):
    g0: LineSegment StartX=-129 StartY=39.2 StartZ=0 EndX=-131.599 EndY=31.2 EndZ=0
    g1: LineSegment StartX=-118 StartY=39.2 StartZ=0 EndX=-120.599 EndY=31.2 EndZ=0
    g2: LineSegment StartX=-129 StartY=39.2 StartZ=0 EndX=-118 EndY=39.2 EndZ=0
    g3: LineSegment StartX=-120.599 StartY=31.2 StartZ=0 EndX=-131.599 EndY=31.2 EndZ=0
  constraints (12):
    c: PointOnObject(g0,g-3)
    c: PointOnObject(g1,g-3)
    c: Parallel(g-4,g0)
    c: Parallel(g-4,g1)
    c: Coincident(g2,g0)
    c: Coincident(g2,g1)
    c: DistanceX(g2,g2) = 11
    c: DistanceY(g1,g1) = 8
    c: Coincident(g3,g1)
    c: Horizontal(g3)
    c: Coincident(g3,g0)
    c: DistanceX(g1,g-3) = 118
FEATURE [PartDesign::Pad] Pad018
  BaseFeature = -> Pad014
  Direction = (0,-1,2e-16)
  Length = 1.2
  Length2 = 10
  Profile = -> Sketch124
  ReferenceAxis = -> Sketch124 [N_Axis]
  Refine = true
  Suppressed = false
  Type = 0
FEATURE [Sketcher::SketchObject] Sketch126
  ArcFitTolerance = 1e-06
  AttachmentSupport = -> [Pad018]
  ExternalGeometry = -> [Pad018]
  FullyConstrained = true
  MakeInternals = false
  MapMode = 5
  Placement = pos=(0,-4,0) rot=(1,0,0;1.5708rad)
  sketch-geometry (8):
    g0: LineSegment StartX=-129.877 StartY=36.5 StartZ=0 EndX=-130.137 EndY=35.7 EndZ=0
    g1: LineSegment StartX=-130.69 StartY=34 StartZ=0 EndX=-130.95 EndY=33.2 EndZ=0
    g2: LineSegment StartX=-129.877 StartY=36.5 StartZ=0 EndX=-118.877 EndY=36.5 EndZ=0
    g3: LineSegment StartX=-130.137 StartY=35.7 StartZ=0 EndX=-119.137 EndY=35.7 EndZ=0
    g4: LineSegment StartX=-130.69 StartY=34 StartZ=0 EndX=-119.69 EndY=34 EndZ=0
    g5: LineSegment StartX=-130.95 StartY=33.2 StartZ=0 EndX=-119.95 EndY=33.2 EndZ=0
    g6: LineSegment StartX=-118.877 StartY=36.5 StartZ=0 EndX=-119.137 EndY=35.7 EndZ=0
    g7: LineSegment StartX=-119.69 StartY=34 StartZ=0 EndX=-119.95 EndY=33.2 EndZ=0
  constraints (20):
    c: Coincident(g2,g0)
    c: Horizontal(g2)
    c: Coincident(g3,g0)
    c: Horizontal(g3)
    c: Coincident(g4,g1)
    c: Horizontal(g4)
    c: Coincident(g5,g1)
    c: Horizontal(g5)
    c: Coincident(g6,g2)
    c: Coincident(g6,g3)
    c: Coincident(g7,g4)
    c: Coincident(g7,g5)
    c: Tangent(g0,g-4)
    c: Tangent(g6,g-5)
    c: Tangent(g1,g-4)
    c: Tangent(g7,g-5)
    c: DistanceY(g3,g2) = 0.8
    c: DistanceY(g5,g4) = 0.8
    c: DistanceY(g-6,g1) = 2
    c: DistanceY(g-6,g0) = 4.5
FEATURE [PartDesign::Chamfer] Chamfer008
  Angle = 45
  Base = -> Pad018 [Edge257]
  BaseFeature = -> Pad018
  ChamferType = 1
  FlipDirection = false
  Refine = true
  Size = 1
  Size2 = 6
  SupportTransform = false
  Suppressed = false
  UseAllEdges = false
FEATURE [PartDesign::Pocket] Pocket010
  BaseFeature = -> Chamfer008
  Direction = (0,1,-2e-16)
  Length = 1
  Length2 = 5
  Profile = -> Sketch126
  ReferenceAxis = -> Sketch126 [N_Axis]
  Refine = true
  Suppressed = false
  Type = 0
FEATURE [PartDesign::Pad] Pad015
  BaseFeature = -> Pocket010
  Direction = (0,-1,2e-16)
  Length = 2
  Length2 = 10
  Profile = -> Sketch121
  ReferenceAxis = -> Sketch121 [N_Axis]
  Refine = true
  Suppressed = false
  Type = 0
FEATURE [PartDesign::Pad] Pad016
  BaseFeature = -> Pad015
  Direction = (0,-1,2e-16)
  Length = 1.6
  Length2 = 10
  Profile = -> Sketch122
  ReferenceAxis = -> Sketch122 [N_Axis]
  Refine = true
  Suppressed = false
  Type = 0
FEATURE [Sketcher::SketchObject] Sketch127
  ArcFitTolerance = 1e-06
  AttachmentSupport = -> [Pad016]
  ExternalGeometry = -> [Pad016]
  FullyConstrained = true
  MakeInternals = false
  MapMode = 5
  Placement = pos=(0,0,-80.4316) rot=(1,0,0;3.14159rad)
  sketch-geometry (8):
    g0: LineSegment StartX=-176.685 StartY=3.6 StartZ=0 EndX=-186.685 EndY=3.6 EndZ=0
    g1: LineSegment [constr] StartX=-186.685 StartY=3.6 StartZ=0 EndX=-186.685 EndY=-9e-16 EndZ=0
    g2: LineSegment StartX=-176.685 StartY=3.6 StartZ=0 EndX=-176.685 EndY=0 EndZ=0
    g3: ArcOfEllipse CenterX=-186.685 CenterY=-9e-16 CenterZ=0 NormalX=0 NormalY=0 NormalZ=1 MajorRadius=10 MinorRadius=3.6 AngleXU=1e-16 StartAngle=0 EndAngle=1.5708
    g4: LineSegment [constr] StartX=-176.685 StartY=-2e-15 StartZ=0 EndX=-196.685 EndY=-2e-15 EndZ=0
    g5: LineSegment [constr] StartX=-186.685 StartY=3.6 StartZ=0 EndX=-186.685 EndY=-3.6 EndZ=0
    g6: GeomPoint [constr] X=-177.356 Y=0 Z=0
    g7: GeomPoint [constr] X=-196.015 Y=-1.9e-15 Z=0
  constraints (13):
    c: Coincident(g0,g-4)
    c: PointOnObject(g0,g-4)
    c: DistanceX(g0,g0) = 10
    c: Coincident(g1,g0)
    c: PointOnObject(g1,g-5)
    c: Vertical(g1)
    c: Coincident(g2,g0)
    c: Coincident(g2,g-5)
    c: InternalAlignment(g4-g7 -> g3) x4
    c: Coincident(g3,g1)
    c: Coincident(g3,g0)
    c: Coincident(g3,g2)
    c: Horizontal(g4)
FEATURE [Sketcher::SketchObject] Sketch128
  ArcFitTolerance = 1e-06
  AttachmentSupport = -> [Pad016]
  ExternalGeometry = -> [Pad016]
  FullyConstrained = true
  MakeInternals = false
  MapMode = 5
  Placement = pos=(0,0,-80.4316) rot=(1,0,0;3.14159rad)
  sketch-geometry (8):
    g0: LineSegment StartX=-215.932 StartY=3.6 StartZ=0 EndX=-215.932 EndY=-1.3e-15 EndZ=0
    g1: LineSegment StartX=-215.932 StartY=3.6 StartZ=0 EndX=-205.932 EndY=3.6 EndZ=0
    g2: LineSegment [constr] StartX=-205.932 StartY=3.6 StartZ=0 EndX=-205.932 EndY=-9e-16 EndZ=0
    g3: ArcOfEllipse CenterX=-205.932 CenterY=-9e-16 CenterZ=0 NormalX=0 NormalY=0 NormalZ=1 MajorRadius=10 MinorRadius=3.6 AngleXU=-3.14159 StartAngle=4.71239 EndAngle=6.28319
    g4: LineSegment [constr] StartX=-215.932 StartY=-1e-15 StartZ=0 EndX=-195.932 EndY=-1e-15 EndZ=0
    g5: LineSegment [constr] StartX=-205.932 StartY=-3.6 StartZ=0 EndX=-205.932 EndY=3.6 EndZ=0
    g6: GeomPoint [constr] X=-215.262 Y=-2e-15 Z=0
    g7: GeomPoint [constr] X=-196.602 Y=-1e-15 Z=0
  constraints (13):
    c: Coincident(g0,g-4)
    c: Coincident(g0,g-5)
    c: Coincident(g1,g0)
    c: PointOnObject(g1,g-3)
    c: DistanceX(g1,g1) = 10
    c: Coincident(g2,g1)
    c: Vertical(g2)
    c: PointOnObject(g2,g-5)
    c: InternalAlignment(g4-g7 -> g3) x4
    c: Coincident(g3,g2)
    c: Coincident(g3,g1)
    c: Coincident(g3,g0)
    c: Horizontal(g4)
FEATURE [PartDesign::SubtractivePipe] SubtractivePipe002
  AuxilleryCurvelinear = true
  AuxillerySpineTangent = false
  BaseFeature = -> Pad016
  Binormal = (0,0,0)
  Mode = 0
  Profile = -> Sketch127
  Refine = true
  Spine = -> Pad016 [Edge254]
  SpineTangent = false
  Suppressed = false
  Transformation = 0
  Transition = 0
FEATURE [PartDesign::SubtractivePipe] SubtractivePipe003
  AuxilleryCurvelinear = true
  AuxillerySpineTangent = false
  BaseFeature = -> SubtractivePipe002
  Binormal = (0,0,0)
  Mode = 0
  Profile = -> Sketch128
  Refine = true
  Spine = -> Pad016 [Edge256,Edge251,Edge252]
  SpineTangent = false
  Suppressed = false
  Transformation = 0
  Transition = 0
FEATURE [Sketcher::SketchObject] Sketch129
  ArcFitTolerance = 1e-06
  AttachmentSupport = -> [Pad016]
  ExternalGeometry = -> [Binder001]
  FullyConstrained = true
  MakeInternals = false
  MapMode = 5
  Placement = pos=(0,-3.6,0) rot=(1,0,0;1.5708rad)
  sketch-geometry (12):
    g0: LineSegment [constr] StartX=-192.176 StartY=-3.18451 StartZ=0 EndX=-181.223 EndY=20.303 EndZ=0
    g1: LineSegment [constr] StartX=-202.765 StartY=20.303 StartZ=0 EndX=-181.223 EndY=20.303 EndZ=0
    g2: LineSegment StartX=-202.765 StartY=20.303 StartZ=0 EndX=-181.223 EndY=20.303 EndZ=0
    g3: LineSegment StartX=-192.176 StartY=-3.18451 StartZ=0 EndX=-196.804 EndY=-13.1107 EndZ=0
    g4: ArcOfCircle CenterX=-207.583 CenterY=4 CenterZ=0 NormalX=0 NormalY=0 NormalZ=1 AngleXU=0 Radius=17 StartAngle=5.84685 EndAngle=7.56663
    g5: ArcOfEllipse CenterX=-181.223 CenterY=8.55923 CenterZ=0 NormalX=0 NormalY=0 NormalZ=1 MajorRadius=23.4779 MinorRadius=11.7437 AngleXU=2e-16 StartAngle=4.71239 EndAngle=7.85398
    g6: LineSegment [constr] StartX=-157.745 StartY=8.55923 StartZ=0 EndX=-204.701 EndY=8.55923 EndZ=0
    g7: LineSegment [constr] StartX=-181.223 StartY=20.303 StartZ=0 EndX=-181.223 EndY=-3.18451 EndZ=0
    g8: GeomPoint [constr] X=-160.894 Y=8.55923 Z=0
    g9: GeomPoint [constr] X=-201.553 Y=8.55923 Z=0
    g10: ArcOfCircle CenterX=-181.223 CenterY=-20.3763 CenterZ=0 NormalX=0 NormalY=0 NormalZ=1 AngleXU=0 Radius=17.1918 StartAngle=1.57079 EndAngle=2.70526
    g11: GeomPoint [constr] X=-181.223 Y=-3.18451 Z=0
  constraints (23):
    c: Coincident(g0,g-5)
    c: Coincident(g1,g-6)
    c: Horizontal(g1)
    c: Coincident(g1,g0)
    c: Parallel(g0,g-4)
    c: Coincident(g2,g1)
    c: Coincident(g2,g0)
    c: Coincident(g3,g0)
    c: Equal(g4,g-5)
    c: Coincident(g4,g1)
    c: Coincident(g4,g0)
    c: InternalAlignment(g6-g9 -> g5) x4
    c: Vertical(g5,g0)
    c: Horizontal(g6)
    c: Coincident(g5,g0)
    c: DistanceX(g6,g-3) = 10.1
    c: Tangent(g10,g3) = -1.5708
    c: PointOnObject(g11,g10)
    c: Tangent(g5,g10,g11) = 1.5708
    c: Coincident(g10,g5)
    c: Coincident(g11,g7)
    c: Parallel(g3,g-4)
    c: Horizontal(g5,g0)
FEATURE [Sketcher::SketchObject] Sketch130
  ArcFitTolerance = 1e-06
  AttachmentOffset = pos=(0,0,-1.6) rot=(0,0,1;0rad)
  AttachmentSupport = -> [Pad016]
  ExternalGeometry = -> [Binder001]
  FullyConstrained = true
  MakeInternals = false
  MapMode = 5
  Placement = pos=(0,-2,-4e-16) rot=(1,0,0;1.5708rad)
  sketch-geometry (12):
    g0: LineSegment [constr] StartX=-192.176 StartY=-3.18451 StartZ=0 EndX=-181.223 EndY=20.303 EndZ=0
    g1: LineSegment [constr] StartX=-202.765 StartY=20.303 StartZ=0 EndX=-181.223 EndY=20.303 EndZ=0
    g2: LineSegment StartX=-202.765 StartY=20.303 StartZ=0 EndX=-181.223 EndY=20.303 EndZ=0
    g3: LineSegment StartX=-192.176 StartY=-3.18451 StartZ=0 EndX=-193.827 EndY=-6.72678 EndZ=0
    g4: ArcOfCircle CenterX=-207.583 CenterY=4 CenterZ=0 NormalX=0 NormalY=0 NormalZ=1 AngleXU=0 Radius=17 StartAngle=5.84685 EndAngle=7.56663
    g5: ArcOfEllipse CenterX=-181.223 CenterY=10.803 CenterZ=0 NormalX=0 NormalY=0 NormalZ=1 MajorRadius=14.4779 MinorRadius=9.5 AngleXU=0 StartAngle=4.71239 EndAngle=7.85398
    g6: LineSegment [constr] StartX=-166.745 StartY=10.803 StartZ=0 EndX=-195.701 EndY=10.803 EndZ=0
    g7: LineSegment [constr] StartX=-181.223 StartY=20.303 StartZ=0 EndX=-181.223 EndY=1.30297 EndZ=0
    g8: GeomPoint [constr] X=-170.298 Y=10.803 Z=0
    g9: GeomPoint [constr] X=-192.148 Y=10.803 Z=0
    g10: ArcOfCircle CenterX=-181.223 CenterY=-12.6042 CenterZ=0 NormalX=0 NormalY=0 NormalZ=1 AngleXU=0 Radius=13.9072 StartAngle=1.5708 EndAngle=2.70526
    g11: GeomPoint [constr] X=-181.223 Y=1.30297 Z=0
  constraints (23):
    c: Coincident(g0,g-5)
    c: Coincident(g1,g-6)
    c: Horizontal(g1)
    c: Coincident(g1,g0)
    c: Parallel(g0,g-4)
    c: Coincident(g2,g1)
    c: Coincident(g2,g0)
    c: Coincident(g3,g0)
    c: Equal(g4,g-5)
    c: Coincident(g4,g1)
    c: Coincident(g4,g0)
    c: InternalAlignment(g6-g9 -> g5) x4
    c: Vertical(g5,g0)
    c: Horizontal(g6)
    c: Coincident(g5,g0)
    c: DistanceX(g6,g-3) = 19.1
    c: Tangent(g10,g3) = -1.5708
    c: PointOnObject(g11,g10)
    c: Tangent(g5,g10,g11) = 1.5708
    c: Coincident(g10,g5)
    c: Coincident(g11,g7)
    c: Parallel(g3,g-4)
    c: DistanceY(g5,g0) = 19
FEATURE [Part::Part2DObjectPython] Clone2D001  label="Sketch130 (2D)"  # Draft 2D object (typed FeaturePython)
  Fuse = false
  Objects = -> [Sketch130]
  Placement = pos=(0,-2,-4e-16) rot=(1,0,0;1.5708rad)
  Scale = (1,1,1)
FEATURE [Sketcher::SketchObject] Sketch131
  ArcFitTolerance = 1e-06
  AttachmentOffset = pos=(0,0,-3.5) rot=(0,0,1;0rad)
  AttachmentSupport = -> [Pad016]
  ExternalGeometry = -> [Binder001]
  FullyConstrained = true
  MakeInternals = false
  MapMode = 5
  Placement = pos=(0,-0.1,-8e-16) rot=(1,0,0;1.5708rad)
  sketch-geometry (1):
    g0: GeomPoint X=-197.47 Y=8.55923 Z=0
  constraints (1):
    c: Symmetric(g-6,g-4,g0)
FEATURE [PartDesign::SubtractiveLoft] SubtractiveLoft002
  BaseFeature = -> SubtractivePipe003
  Closed = false
  Profile = -> Sketch129
  Refine = true
  Ruled = false
  Sections = -> [Sketch130]
  Suppressed = false
FEATURE [PartDesign::SubtractiveLoft] SubtractiveLoft003
  BaseFeature = -> SubtractiveLoft002
  Closed = false
  Profile = -> Clone2D001
  Refine = true
  Ruled = false
  Sections = -> [Sketch131]
  Suppressed = false
FEATURE [PartDesign::Chamfer] Chamfer010
  Angle = 45
  Base = -> SubtractiveLoft003 [Edge200,Edge201,Edge203,Edge202,Edge194]
  BaseFeature = -> SubtractiveLoft003
  ChamferType = 0
  FlipDirection = false
  Refine = true
  Size = 1.5
  Size2 = 1
  SupportTransform = false
  Suppressed = false
  UseAllEdges = false
FEATURE [PartDesign::Chamfer] Chamfer011
  Angle = 45
  Base = -> Chamfer010 [Edge15]
  BaseFeature = -> Chamfer010
  ChamferType = 0
  FlipDirection = false
  Refine = true
  Size = 1.6
  Size2 = 1
  SupportTransform = false
  Suppressed = false
  UseAllEdges = false
FEATURE [PartDesign::Chamfer] Chamfer012
  Angle = 45
  Base = -> Chamfer011 [Edge10]
  BaseFeature = -> Chamfer011
  ChamferType = 0
  FlipDirection = false
  Refine = true
  Size = 3.5
  Size2 = 1
  SupportTransform = false
  Suppressed = false
  UseAllEdges = false
FEATURE [PartDesign::Chamfer] Chamfer013
  Angle = 45
  Base = -> Chamfer012 [Edge145,Edge94]
  BaseFeature = -> Chamfer012
  ChamferType = 0
  FlipDirection = false
  Refine = true
  Size = 1.9
  Size2 = 1
  SupportTransform = false
  Suppressed = false
  UseAllEdges = false
FEATURE [Sketcher::SketchObject] Sketch132
  ArcFitTolerance = 1e-06
  AttachmentSupport = -> [Pad016]
  ExternalGeometry = -> [Binder001]
  FullyConstrained = true
  MakeInternals = false
  MapMode = 5
  Placement = pos=(0,-3.6,0) rot=(1,0,0;1.5708rad)
  sketch-geometry (3):
    g0: LineSegment [constr] StartX=-215.42 StartY=-53.0314 StartZ=0 EndX=-167.782 EndY=-53.0314 EndZ=0
    g1: Circle CenterX=-191.282 CenterY=-53.0314 CenterZ=0 NormalX=0 NormalY=0 NormalZ=1 AngleXU=0 Radius=11.5
    g2: Circle CenterX=-191.282 CenterY=-53.0314 CenterZ=0 NormalX=0 NormalY=0 NormalZ=1 AngleXU=0 Radius=10.7
  constraints (8):
    c: Coincident(g0,g-3)
    c: PointOnObject(g0,g-4)
    c: Horizontal(g0)
    c: Diameter(g1) = 23
    c: PointOnObject(g1,g0)
    c: DistanceX(g1,g0) = 23.5
    c: Diameter(g2) = 21.4
    c: Coincident(g2,g1)
FEATURE [PartDesign::Fillet] Fillet007
  Base = -> Chamfer013 [Edge83]
  BaseFeature = -> Chamfer013
  Radius = 1.1
  Refine = true
  SupportTransform = false
  Suppressed = false
  UseAllEdges = false
FEATURE [PartDesign::Fillet] Fillet008
  Base = -> Fillet007 [Edge76]
  BaseFeature = -> Fillet007
  Radius = 1.9
  Refine = true
  SupportTransform = false
  Suppressed = false
  UseAllEdges = false
FEATURE [PartDesign::Pocket] Pocket011
  BaseFeature = -> Fillet008
  Direction = (0,1,-2e-16)
  Length = 0.8
  Length2 = 5
  Profile = -> Sketch132
  ReferenceAxis = -> Sketch132 [N_Axis]
  Refine = true
  Suppressed = false
  Type = 0
FEATURE [Part::Part2DObjectPython] ShapeString  # Draft 2D object (typed FeaturePython)
  FontFile = <path>
  Fuse = false
  Justification = 6
  JustificationReference = 0
  KeepLeftMargin = false
  MakeFace = true
  ObliqueAngle = 0
  Placement = pos=(-199,-3.6,-57.5) rot=(1,0,0;1.5708rad)
  ScaleToSize = true
  Size = 10
  String = AS
  Tracking = 0
FEATURE [PartDesign::Pocket] Pocket012
  BaseFeature = -> Pocket011
  Direction = (0,1,0)
  Length = 1
  Length2 = 5
  Profile = -> ShapeString
  ReferenceAxis = -> ShapeString [N_Axis]
  Refine = true
  Suppressed = false
  Type = 0
FEATURE [PartDesign::Body] Body007  label="lato DX"
  AllowCompound = false
  Group = -> [Binder001,Sketch114,Pad011,Chamfer014,Sketch115,Pocket006,Sketch116,Pad012,Sketch117,Pocket007,Sketch118,Pad013,Sketch119,Pocket008,Pad017,Chamfer009,Pocket009,Sketch123,Sketch120,Pad014,Pad018,Chamfer008,Pocket010,Sketch121,Pad015,Sketch122,Pad016,Sketch124,Sketch125,Sketch126,Sketch127,Sketch128,SubtractivePipe002,SubtractivePipe003,Sketch129,Sketch130,Clone2D001,Sketch131,SubtractiveLoft002,+11 more]
  Origin = -> Origin007
  Tip = -> Pocket012
FEATURE [Sketcher::SketchObject] Sketch133
  ArcFitTolerance = 1e-06
  AttachmentSupport = -> [Binder]
  ExternalGeometry = -> [Binder]
  FullyConstrained = true
  MakeInternals = false
  MapMode = 5
  Placement = pos=(0,9e-16,0) rot=(0,0.707107,0.707107;3.14159rad)
  sketch-geometry (30):
    g0: LineSegment StartX=0 StartY=39.2 StartZ=0 EndX=0 EndY=3.2 EndZ=0
    g1: LineSegment StartX=0 StartY=3.2 StartZ=0 EndX=82.8 EndY=3.2 EndZ=0
    g2: LineSegment StartX=82.8 StartY=3.2 StartZ=0 EndX=82.8 EndY=6.2 EndZ=0
    g3: LineSegment StartX=82.8 StartY=6.2 StartZ=0 EndX=91.752 EndY=6.2 EndZ=0
    g4: LineSegment StartX=0 StartY=39.2 StartZ=0 EndX=195.887 EndY=39.2 EndZ=0
    g5: LineSegment StartX=195.887 StartY=39.2 StartZ=0 EndX=202.765 EndY=20.303 EndZ=0
    g6: LineSegment StartX=192.333 StartY=24.9893 StartZ=0 EndX=196.467 EndY=26.4942 EndZ=0
    g7: LineSegment StartX=196.467 StartY=26.4942 StartZ=0 EndX=194.073 EndY=33.0721 EndZ=0
    g8: LineSegment StartX=194.073 StartY=33.0721 StartZ=0 EndX=189.939 EndY=31.5672 EndZ=0
    g9: LineSegment StartX=189.939 StartY=31.5672 StartZ=0 EndX=192.333 EndY=24.9893 EndZ=0
    g10: ArcOfCircle CenterX=107.6 CenterY=4 CenterZ=0 NormalX=0 NormalY=0 NormalZ=1 AngleXU=0 Radius=16 StartAngle=1.5708 EndAngle=3.00366
    g11: LineSegment StartX=107.6 StartY=20 StartZ=0 EndX=132.428 EndY=20 EndZ=0
    g12: ArcOfCircle [constr] CenterX=132.428 CenterY=4 CenterZ=0 NormalX=0 NormalY=0 NormalZ=1 AngleXU=0 Radius=16 StartAngle=0.314159 EndAngle=1.5708
    g13: LineSegment StartX=147.645 StartY=8.94427 StartZ=0 EndX=176.685 EndY=-80.4316 EndZ=0
    g14: LineSegment StartX=176.685 StartY=-80.4316 StartZ=0 EndX=215.932 EndY=-80.4316 EndZ=0
    g15: ArcOfCircle CenterX=207.583 CenterY=4 CenterZ=0 NormalX=0 NormalY=0 NormalZ=1 AngleXU=0 Radius=17 StartAngle=1.85815 EndAngle=3.57792
    g16: ArcOfCircle CenterX=184.801 CenterY=-67.3089 CenterZ=0 NormalX=0 NormalY=0 NormalZ=1 AngleXU=0 Radius=33.7833 StartAngle=5.88425 EndAngle=6.71952
    g17: LineSegment StartX=192.176 StartY=-3.18451 StartZ=0 EndX=215.42 EndY=-53.0314 EndZ=0
    g18: Circle CenterX=5.6 CenterY=34.8 CenterZ=0 NormalX=0 NormalY=0 NormalZ=1 AngleXU=0 Radius=1.8
    g19: Circle CenterX=5.6 CenterY=7.6 CenterZ=0 NormalX=0 NormalY=0 NormalZ=1 AngleXU=0 Radius=1.8
    g20: Circle CenterX=78.51 CenterY=34.8 CenterZ=0 NormalX=0 NormalY=0 NormalZ=1 AngleXU=0 Radius=1.8
    g21: Circle CenterX=78.51 CenterY=7.6 CenterZ=0 NormalX=0 NormalY=0 NormalZ=1 AngleXU=0 Radius=1.8
    g22: Circle CenterX=184.08 CenterY=34.8 CenterZ=0 NormalX=0 NormalY=0 NormalZ=1 AngleXU=0 Radius=1.8
    g23: Circle CenterX=179.305 CenterY=-76.8316 CenterZ=0 NormalX=0 NormalY=0 NormalZ=1 AngleXU=0 Radius=1.8
    g24: Circle CenterX=213.443 CenterY=-76.8316 CenterZ=0 NormalX=0 NormalY=0 NormalZ=1 AngleXU=0 Radius=1.8
    g25: Circle CenterX=19 CenterY=21.2 CenterZ=0 NormalX=0 NormalY=0 NormalZ=1 AngleXU=0 Radius=6.3
    g26: Circle CenterX=42 CenterY=21.2 CenterZ=0 NormalX=0 NormalY=0 NormalZ=1 AngleXU=0 Radius=6.3
    g27: Circle CenterX=65 CenterY=21.2 CenterZ=0 NormalX=0 NormalY=0 NormalZ=1 AngleXU=0 Radius=6.3
    g28: LineSegment StartX=132.428 StartY=20 StartZ=0 EndX=144.053 EndY=20 EndZ=0
    g29: LineSegment StartX=147.645 StartY=8.94427 StartZ=0 EndX=144.053 EndY=20 EndZ=0
  constraints (65):
    c: Coincident(g0,g-4)
    c: Coincident(g0,g-5)
    c: Coincident(g1,g0)
    c: Coincident(g1,g-6)
    c: Coincident(g2,g1)
    c: Coincident(g2,g-7)
    c: Coincident(g3,g2)
    c: Coincident(g3,g-8)
    c: Coincident(g4,g0)
    c: Coincident(g4,g-16)
    c: Coincident(g5,g4)
    c: Coincident(g5,g-16)
    c: Coincident(g6,g-20)
    c: Coincident(g6,g-21)
    c: Coincident(g7,g6)
    c: Coincident(g7,g-23)
    c: Coincident(g8,g7)
    c: Coincident(g8,g-22)
    c: Coincident(g9,g8)
    c: Coincident(g9,g6)
    c: Equal(g10,g-8)
    c: Coincident(g10,g3)
    c: Coincident(g10,g-9)
    c: Coincident(g11,g10)
    c: Coincident(g11,g-10)
    c: Equal(g12,g-10)
    c: Coincident(g12,g11)
    c: Coincident(g12,g-11)
    c: Coincident(g13,g12)
    c: Coincident(g13,g-12)
    c: Coincident(g14,g13)
    c: Coincident(g14,g-13)
    c: Equal(g15,g-15)
    c: Coincident(g15,g5)
    c: Coincident(g15,g-15)
    c: Equal(g16,g-13)
    c: Coincident(g16,g14)
    c: Coincident(g16,g-14)
    c: Coincident(g17,g15)
    c: Coincident(g17,g16)
    c: Equal(g18,g-28)
    c: Equal(g19,g-29)
    c: Equal(g20,g-26)
    c: Equal(g21,g-27)
    c: Equal(g22,g-17)
    c: Equal(g24,g-25)
    c: Equal(g23,g-24)
    c: Coincident(g23,g-24)
    c: Coincident(g24,g-25)
    c: Coincident(g22,g-17)
    c: Coincident(g20,g-26)
    c: Coincident(g21,g-27)
    c: Coincident(g18,g-28)
    c: Coincident(g19,g-29)
    c: Equal(g25,g-30)
    c: Equal(g26,g-31)
    c: Equal(g27,g-32)
    c: Coincident(g25,g-30)
    c: Coincident(g26,g-31)
    c: Coincident(g27,g-32)
    c: Parallel(g28,g11)
    c: Parallel(g29,g13)
    c: Coincident(g28,g11)
    c: Coincident(g29,g12)
    c: Coincident(g29,g28)
FEATURE [PartDesign::Pad] Pad019
  Direction = (0,1,-2e-16)
  Length = 2
  Length2 = 10
  Profile = -> Sketch133
  ReferenceAxis = -> Sketch133 [N_Axis]
  Refine = true
  Suppressed = false
  Type = 0
FEATURE [Sketcher::SketchObject] Sketch091  label="Sketch091 - forma anteriore"
  ArcFitTolerance = 1e-06
  AttachmentSupport = -> [Pad019]
  ExternalGeometry = -> [Binder]
  FullyConstrained = true
  MakeInternals = false
  MapMode = 5
  Placement = pos=(0,2,0) rot=(0,0.707107,0.707107;3.14159rad)
  sketch-geometry (12):
    g0: Circle CenterX=5.6 CenterY=34.8 CenterZ=0 NormalX=0 NormalY=0 NormalZ=1 AngleXU=0 Radius=1.8
    g1: Circle CenterX=5.6 CenterY=7.6 CenterZ=0 NormalX=0 NormalY=0 NormalZ=1 AngleXU=0 Radius=1.8
    g2: Circle CenterX=78.51 CenterY=34.8 CenterZ=0 NormalX=0 NormalY=0 NormalZ=1 AngleXU=0 Radius=1.8
    g3: Circle CenterX=78.51 CenterY=7.6 CenterZ=0 NormalX=0 NormalY=0 NormalZ=1 AngleXU=0 Radius=1.8
    g4: LineSegment StartX=0 StartY=39.2 StartZ=0 EndX=0 EndY=3.2 EndZ=0
    g5: LineSegment StartX=0 StartY=3.2 StartZ=0 EndX=82.8 EndY=3.2 EndZ=0
    g6: LineSegment StartX=82.8 StartY=3.2 StartZ=0 EndX=82.8 EndY=39.2 EndZ=0
    g7: LineSegment StartX=82.8 StartY=39.2 StartZ=0 EndX=0 EndY=39.2 EndZ=0
    g8: ArcOfCircle CenterX=19 CenterY=21.2 CenterZ=0 NormalX=0 NormalY=0 NormalZ=1 AngleXU=0 Radius=10 StartAngle=1.5708 EndAngle=4.71239
    g9: ArcOfCircle CenterX=65 CenterY=21.2 CenterZ=0 NormalX=0 NormalY=0 NormalZ=1 AngleXU=0 Radius=10 StartAngle=4.71239 EndAngle=7.85398
    g10: LineSegment StartX=19 StartY=31.2 StartZ=0 EndX=65 EndY=31.2 EndZ=0
    g11: LineSegment StartX=19 StartY=11.2 StartZ=0 EndX=65 EndY=11.2 EndZ=0
  constraints (25):
    c: Equal(g2,g-7)
    c: Equal(g3,g-8)
    c: Equal(g1,g-13)
    c: Equal(g0,g-12)
    c: Coincident(g0,g-12)
    c: Coincident(g1,g-13)
    c: Coincident(g3,g-8)
    c: Coincident(g2,g-7)
    c: Coincident(g4,g-4)
    c: Coincident(g4,g-5)
    c: Coincident(g5,g4)
    c: Coincident(g5,g-6)
    c: Coincident(g6,g5)
    c: PointOnObject(g6,g-3)
    c: Vertical(g6)
    c: Coincident(g7,g6)
    c: Coincident(g7,g4)
    c: Tangent(g8,g10) = 1.5708
    c: Tangent(g8,g11) = -1.5708
    c: Tangent(g9,g10) = 1.5708
    c: Tangent(g9,g11) = -1.5708
    c: Equal(g8,g9)
    c: Radius(g8) = 10
    c: Coincident(g8,g-11)
    c: Coincident(g9,g-9)
FEATURE [Sketcher::SketchObject] Sketch093  label="Sketch093 - scavi interni pulsanti"
  ArcFitTolerance = 1e-06
  AttachmentSupport = -> [Pad019]
  ExternalGeometry = -> [Binder]
  FullyConstrained = true
  MakeInternals = false
  MapMode = 5
  Placement = pos=(0,1.8e-15,0) rot=(1,0,0;1.5708rad)
  sketch-geometry (3):
    g0: Circle CenterX=-65 CenterY=21.2 CenterZ=0 NormalX=0 NormalY=0 NormalZ=1 AngleXU=0 Radius=7.3
    g1: Circle CenterX=-42 CenterY=21.2 CenterZ=0 NormalX=0 NormalY=0 NormalZ=1 AngleXU=0 Radius=7.3
    g2: Circle CenterX=-19 CenterY=21.2 CenterZ=0 NormalX=0 NormalY=0 NormalZ=1 AngleXU=0 Radius=7.3
  constraints (6):
    c: Coincident(g0,g-3)
    c: Coincident(g1,g-4)
    c: Coincident(g2,g-5)
    c: Diameter(g0) = 14.6
    c: Diameter(g1) = 14.6
    c: Diameter(g2) = 14.6
FEATURE [Sketcher::SketchObject] Sketch094  label="Sketch094 - forma centrale"
  ArcFitTolerance = 1e-06
  AttachmentSupport = -> [Pad019]
  ExternalGeometry = -> [Binder]
  FullyConstrained = true
  MakeInternals = false
  MapMode = 5
  Placement = pos=(0,2,0) rot=(0,0.707107,0.707107;3.14159rad)
  sketch-geometry (4):
    g0: LineSegment StartX=137.815 StartY=39.2 StartZ=0 EndX=142.655 EndY=24.303 EndZ=0
    g1: LineSegment StartX=110.815 StartY=24.303 StartZ=0 EndX=142.655 EndY=24.303 EndZ=0
    g2: LineSegment StartX=137.815 StartY=39.2 StartZ=0 EndX=110.815 EndY=39.2 EndZ=0
    g3: ArcOfCircle CenterX=92.2534 CenterY=31.7515 CenterZ=0 NormalX=0 NormalY=0 NormalZ=1 AngleXU=0 Radius=20 StartAngle=5.90156 EndAngle=6.66481
  constraints (12):
    c: PointOnObject(g0,g-3)
    c: Tangent(g0,g-5)
    c: Horizontal(g1)
    c: Coincident(g1,g0)
    c: Coincident(g2,g0)
    c: PointOnObject(g2,g-3)
    c: DistanceX(g2,g2) = 27
    c: Vertical(g1,g2)
    c: Coincident(g3,g2)
    c: Radius(g3) = 20
    c: Coincident(g3,g1)
    c: DistanceY(g-6,g0) = 4
FEATURE [Sketcher::SketchObject] Sketch095  label="Sketch095 - forma posteriore"
  ArcFitTolerance = 1e-06
  AttachmentSupport = -> [Pad019]
  ExternalGeometry = -> [Binder]
  FullyConstrained = true
  MakeInternals = false
  MapMode = 5
  Placement = pos=(0,2,0) rot=(0,0.707107,0.707107;3.14159rad)
  sketch-geometry (15):
    g0: LineSegment StartX=137.815 StartY=39.2 StartZ=0 EndX=143.955 EndY=20.303 EndZ=0
    g1: LineSegment StartX=143.955 StartY=20.303 StartZ=0 EndX=190.141 EndY=20.303 EndZ=0
    g2: ArcOfCircle CenterX=184.08 CenterY=34.8 CenterZ=0 NormalX=0 NormalY=0 NormalZ=1 AngleXU=0 Radius=3.5 StartAngle=3.49066 EndAngle=4.71239
    g3: LineSegment StartX=180.791 StartY=33.6029 StartZ=0 EndX=178.754 EndY=39.2 EndZ=0
    g4: LineSegment StartX=184.08 StartY=31.3 StartZ=0 EndX=186.139 EndY=31.3 EndZ=0
    g5: LineSegment StartX=190.141 StartY=20.303 StartZ=0 EndX=186.139 EndY=31.3 EndZ=0
    g6: LineSegment StartX=137.815 StartY=39.2 StartZ=0 EndX=156.815 EndY=39.2 EndZ=0
    g7: LineSegment StartX=178.754 StartY=39.2 StartZ=0 EndX=168.815 EndY=39.2 EndZ=0
    g8: LineSegment StartX=156.815 StartY=31.2 StartZ=0 EndX=168.815 EndY=31.2 EndZ=0
    g9: ArcOfCircle CenterX=176.411 CenterY=35.2 CenterZ=0 NormalX=0 NormalY=0 NormalZ=1 AngleXU=0 Radius=20 StartAngle=2.94023 EndAngle=3.34295
    g10: ArcOfCircle CenterX=188.411 CenterY=35.2 CenterZ=0 NormalX=0 NormalY=0 NormalZ=1 AngleXU=0 Radius=20 StartAngle=2.94023 EndAngle=3.34295
    g11: LineSegment StartX=157.815 StartY=39.2 StartZ=0 EndX=167.815 EndY=39.2 EndZ=0
    g12: LineSegment StartX=157.436 StartY=36.2 StartZ=0 EndX=167.436 EndY=36.2 EndZ=0
    g13: ArcOfCircle CenterX=177.411 CenterY=35.2 CenterZ=0 NormalX=0 NormalY=0 NormalZ=1 AngleXU=0 Radius=20 StartAngle=2.94023 EndAngle=3.09157
    g14: ArcOfCircle CenterX=187.411 CenterY=35.2 CenterZ=0 NormalX=0 NormalY=0 NormalZ=1 AngleXU=0 Radius=20 StartAngle=2.94023 EndAngle=3.09157
  constraints (46):
    c: PointOnObject(g0,g-3)
    c: Tangent(g0,g-6)
    c: Coincident(g1,g0)
    c: Horizontal(g1)
    c: Radius(g2) = 3.5
    c: Coincident(g2,g-5)
    c: PointOnObject(g3,g-3)
    c: Parallel(g3,g-4)
    c: Tangent(g3,g2) = 1.5708
    c: Horizontal(g4)
    c: Tangent(g4,g2) = -1.5708
    c: Coincident(g5,g1)
    c: Parallel(g5,g-4)
    c: Coincident(g5,g4)
    c: DistanceX(g4,g-8) = 3.8
    c: Coincident(g6,g0)
    c: PointOnObject(g6,g-3)
    c: Coincident(g7,g3)
    c: PointOnObject(g7,g-3)
    c: Horizontal(g8)
    c: DistanceX(g6,g7) = 12
    c: Vertical(g8,g6)
    c: Vertical(g7,g8)
    c: DistanceY(g8,g6) = 8
    c: Coincident(g9,g8)
    c: Coincident(g9,g6)
    c: Coincident(g10,g7)
    c: Coincident(g10,g8)
    c: Radius(g9) = 20
    c: Radius(g10) = 20
    c: PointOnObject(g11,g-3)
    c: PointOnObject(g11,g-3)
    c: DistanceX(g11,g11) = 10
    c: DistanceX(g6,g11) = 1
    c: Horizontal(g12)
    c: Equal(g12,g11)
    c: DistanceY(g12,g11) = 3
    c: Coincident(g13,g11)
    c: Coincident(g13,g12)
    c: Radius(g13) = 20
    c: Coincident(g14,g11)
    c: Coincident(g14,g12)
    c: Radius(g14) = 20
    c: DistanceX(g0,g6) = 19
    c: Horizontal(g9,g13)
    c: Horizontal(g0,g-4)
FEATURE [Sketcher::SketchObject] Sketch096  label="Sketch096 - forma impugnatura"
  ArcFitTolerance = 1e-06
  AttachmentSupport = -> [Pad019]
  ExternalGeometry = -> [Binder]
  FullyConstrained = true
  MakeInternals = false
  MapMode = 5
  Placement = pos=(0,2,0) rot=(0,0.707107,0.707107;3.14159rad)
  sketch-geometry (8):
    g0: LineSegment StartX=176.685 StartY=-80.4316 StartZ=0 EndX=143.955 EndY=20.303 EndZ=0
    g1: LineSegment StartX=176.685 StartY=-80.4316 StartZ=0 EndX=215.932 EndY=-80.4316 EndZ=0
    g2: Circle CenterX=179.305 CenterY=-76.8316 CenterZ=0 NormalX=0 NormalY=0 NormalZ=1 AngleXU=0 Radius=3
    g3: Circle CenterX=213.443 CenterY=-76.8316 CenterZ=0 NormalX=0 NormalY=0 NormalZ=1 AngleXU=0 Radius=3
    g4: LineSegment StartX=143.955 StartY=20.303 StartZ=0 EndX=202.765 EndY=20.303 EndZ=0
    g5: LineSegment StartX=215.42 StartY=-53.0314 StartZ=0 EndX=192.176 EndY=-3.18451 EndZ=0
    g6: ArcOfCircle CenterX=184.801 CenterY=-67.3089 CenterZ=0 NormalX=0 NormalY=0 NormalZ=1 AngleXU=0 Radius=33.7833 StartAngle=5.88425 EndAngle=6.71952
    g7: ArcOfCircle CenterX=207.583 CenterY=4 CenterZ=0 NormalX=0 NormalY=0 NormalZ=1 AngleXU=0 Radius=17 StartAngle=1.85815 EndAngle=3.57792
  constraints (19):
    c: Coincident(g0,g-4)
    c: PointOnObject(g0,g-3)
    c: Horizontal(g0,g-7)
    c: Coincident(g1,g0)
    c: Coincident(g1,g-5)
    c: Diameter(g2) = 6
    c: Diameter(g3) = 6
    c: Coincident(g2,g-9)
    c: Coincident(g3,g-10)
    c: Coincident(g4,g0)
    c: Coincident(g5,g-6)
    c: Coincident(g6,g1)
    c: Coincident(g6,g5)
    c: Equal(g-5,g6)
    c: Coincident(g5,g-7)
    c: Coincident(g4,g-7)
    c: Tangent(g7,g-7)
    c: Coincident(g7,g4)
    c: Coincident(g7,g5)
FEATURE [Sketcher::SketchObject] Sketch097
  ArcFitTolerance = 1e-06
  AttachmentSupport = -> [Pad019]
  ExternalGeometry = -> [Binder]
  FullyConstrained = true
  MakeInternals = false
  MapMode = 5
  Placement = pos=(0,2,0) rot=(0,0.707107,0.707107;3.14159rad)
  sketch-geometry (4):
    g0: LineSegment StartX=90 StartY=36.8 StartZ=0 EndX=108 EndY=36.8 EndZ=0
    g1: LineSegment StartX=108 StartY=36.8 StartZ=0 EndX=108 EndY=26.8 EndZ=0
    g2: LineSegment StartX=108 StartY=26.8 StartZ=0 EndX=90 EndY=26.8 EndZ=0
    g3: ArcOfCircle CenterX=94 CenterY=31.8 CenterZ=0 NormalX=0 NormalY=0 NormalZ=1 AngleXU=0 Radius=6.40312 StartAngle=2.24554 EndAngle=4.03765
  constraints (13):
    c: Horizontal(g0)
    c: Coincident(g1,g0)
    c: Vertical(g1)
    c: DistanceX(g0,g0) = 18
    c: DistanceY(g1,g1) = 10
    c: Coincident(g2,g1)
    c: Horizontal(g2)
    c: Equal(g2,g0)
    c: DistanceY(g0,g-3) = 2.4
    c: Coincident(g3,g0)
    c: Coincident(g3,g2)
    c: DistanceX(g2,g3) = 4
    c: DistanceX(g-3,g0) = 90
FEATURE [PartDesign::Chamfer] Chamfer015
  Angle = 45
  Base = -> Pad019 [Edge19,Edge22,Edge79]
  BaseFeature = -> Pad019
  ChamferType = 0
  FlipDirection = false
  Refine = true
  Size = 1.9
  Size2 = 1
  SupportTransform = false
  Suppressed = false
  UseAllEdges = false
FEATURE [PartDesign::Pocket] Pocket002
  BaseFeature = -> Chamfer015
  Direction = (0,1,-2e-16)
  Length = 1.2
  Length2 = 5
  Profile = -> Sketch093
  ReferenceAxis = -> Sketch093 [N_Axis]
  Refine = true
  Suppressed = false
  Type = 0
FEATURE [PartDesign::Pad] Pad005
  BaseFeature = -> Pocket002
  Direction = (0,1,-2e-16)
  Length = 1.6
  Length2 = 10
  Profile = -> Sketch091
  ReferenceAxis = -> Sketch091 [N_Axis]
  Refine = true
  Suppressed = false
  Type = 0
FEATURE [Sketcher::SketchObject] Sketch092  label="Sketch092 - scavi per viti anteriori"
  ArcFitTolerance = 1e-06
  AttachmentSupport = -> [Pad005]
  ExternalGeometry = -> [Binder]
  FullyConstrained = true
  MakeInternals = false
  MapMode = 5
  Placement = pos=(0,3.6,0) rot=(0,0.707107,0.707107;3.14159rad)
  sketch-geometry (20):
    g0: ArcOfCircle CenterX=5.6 CenterY=7.6 CenterZ=0 NormalX=0 NormalY=0 NormalZ=1 AngleXU=0 Radius=3.5 StartAngle=0 EndAngle=1.5708
    g1: ArcOfCircle CenterX=5.6 CenterY=34.8 CenterZ=0 NormalX=0 NormalY=0 NormalZ=1 AngleXU=0 Radius=3.5 StartAngle=4.71239 EndAngle=6.28319
    g2: ArcOfCircle CenterX=78.51 CenterY=34.8 CenterZ=0 NormalX=0 NormalY=0 NormalZ=1 AngleXU=0 Radius=3.5 StartAngle=3.14159 EndAngle=4.71239
    g3: ArcOfCircle CenterX=78.51 CenterY=7.6 CenterZ=0 NormalX=0 NormalY=0 NormalZ=1 AngleXU=0 Radius=3.5 StartAngle=1.5708 EndAngle=3.14159
    g4: LineSegment StartX=0 StartY=3.2 StartZ=0 EndX=0 EndY=11.1 EndZ=0
    g5: LineSegment StartX=0 StartY=11.1 StartZ=0 EndX=5.6 EndY=11.1 EndZ=0
    g6: LineSegment StartX=0 StartY=3.2 StartZ=0 EndX=9.1 EndY=3.2 EndZ=0
    g7: LineSegment StartX=9.1 StartY=3.2 StartZ=0 EndX=9.1 EndY=7.6 EndZ=0
    g8: LineSegment StartX=0 StartY=39.2 StartZ=0 EndX=0 EndY=31.3 EndZ=0
    g9: LineSegment StartX=0 StartY=31.3 StartZ=0 EndX=5.6 EndY=31.3 EndZ=0
    g10: LineSegment StartX=0 StartY=39.2 StartZ=0 EndX=9.1 EndY=39.2 EndZ=0
    g11: LineSegment StartX=9.1 StartY=39.2 StartZ=0 EndX=9.1 EndY=34.8 EndZ=0
    g12: LineSegment StartX=82.8 StartY=39.2 StartZ=0 EndX=75.01 EndY=39.2 EndZ=0
    g13: LineSegment StartX=82.8 StartY=39.2 StartZ=0 EndX=82.8 EndY=31.3 EndZ=0
    g14: LineSegment StartX=82.8 StartY=31.3 StartZ=0 EndX=78.51 EndY=31.3 EndZ=0
    g15: LineSegment StartX=82.8 StartY=3.2 StartZ=0 EndX=75.01 EndY=3.2 EndZ=0
    g16: LineSegment StartX=75.01 StartY=3.2 StartZ=0 EndX=75.01 EndY=7.6 EndZ=0
    g17: LineSegment StartX=82.8 StartY=3.2 StartZ=0 EndX=82.8 EndY=11.1 EndZ=0
    g18: LineSegment StartX=82.8 StartY=11.1 StartZ=0 EndX=78.51 EndY=11.1 EndZ=0
    g19: LineSegment StartX=75.01 StartY=39.2 StartZ=0 EndX=75.01 EndY=34.8 EndZ=0
  constraints (48):
    c: Radius(g0) = 3.5
    c: Coincident(g0,g-10)
    c: Radius(g1) = 3.5
    c: Coincident(g1,g-9)
    c: Radius(g2) = 3.5
    c: Coincident(g2,g-8)
    c: Radius(g3) = 3.5
    c: Coincident(g3,g-7)
    c: Coincident(g4,g-5)
    c: PointOnObject(g4,g-4)
    c: Coincident(g5,g4)
    c: Horizontal(g5)
    c: Coincident(g6,g4)
    c: PointOnObject(g6,g-5)
    c: Coincident(g7,g6)
    c: Vertical(g7)
    c: Coincident(g8,g-4)
    c: PointOnObject(g8,g-4)
    c: Coincident(g9,g8)
    c: Horizontal(g9)
    c: Coincident(g10,g8)
    c: PointOnObject(g10,g-3)
    c: Coincident(g11,g10)
    c: Vertical(g11)
    c: PointOnObject(g12,g-3)
    c: PointOnObject(g12,g-3)
    c: Coincident(g13,g12)
    c: Vertical(g13)
    c: Coincident(g14,g13)
    c: Horizontal(g14)
    c: Coincident(g15,g-6)
    c: PointOnObject(g15,g-5)
    c: Coincident(g16,g15)
    c: Vertical(g16)
    c: Coincident(g17,g15)
    c: Coincident(g18,g17)
    c: Horizontal(g18)
    c: Tangent(g3,g18) = -1.5708
    c: Tangent(g16,g3) = 1.5708
    c: Coincident(g19,g12)
    c: Vertical(g19)
    c: Tangent(g2,g19) = -1.5708
    c: Tangent(g2,g14) = 1.5708
    c: Tangent(g0,g7) = -1.5708
    c: Tangent(g0,g5) = 1.5708
    c: Tangent(g9,g1) = -1.5708
    c: Tangent(g1,g11) = 1.5708
    c: Tangent(g17,g13)
FEATURE [PartDesign::Pocket] Pocket001
  BaseFeature = -> Pad005
  Direction = (0,-1,2e-16)
  Length = 1.6
  Length2 = 5
  Profile = -> Sketch092
  ReferenceAxis = -> Sketch092 [N_Axis]
  Refine = true
  Suppressed = false
  Type = 0
FEATURE [PartDesign::Pad] Pad006
  BaseFeature = -> Pocket001
  Direction = (0,1,-2e-16)
  Length = 0.8
  Length2 = 10
  Profile = -> Sketch094
  ReferenceAxis = -> Sketch094 [N_Axis]
  Refine = true
  Suppressed = false
  Type = 0
FEATURE [PartDesign::Pad] Pad007
  BaseFeature = -> Pad006
  Direction = (0,1,-2e-16)
  Length = 2
  Length2 = 10
  Profile = -> Sketch095
  ReferenceAxis = -> Sketch095 [N_Axis]
  Refine = true
  Suppressed = false
  Type = 0
FEATURE [PartDesign::Pad] Pad008  label="Pad008 - forma impugnatura"
  BaseFeature = -> Pad007
  Direction = (0,1,-2e-16)
  Length = 1.6
  Length2 = 10
  Profile = -> Sketch096
  ReferenceAxis = -> Sketch096 [N_Axis]
  Refine = true
  Suppressed = false
  Type = 0
FEATURE [PartDesign::Pad] Pad009
  BaseFeature = -> Pad008
  Direction = (0,1,-2e-16)
  Length = 1.6
  Length2 = 10
  Profile = -> Sketch097
  ReferenceAxis = -> Sketch097 [N_Axis]
  Refine = true
  Suppressed = false
  Type = 0
FEATURE [Sketcher::SketchObject] Sketch098
  ArcFitTolerance = 1e-06
  AttachmentSupport = -> [Pad006]
  ExternalGeometry = -> [Binder]
  FullyConstrained = true
  MakeInternals = false
  MapMode = 5
  Placement = pos=(0,2.8,-7e-16) rot=(0,0.707107,0.707107;3.14159rad)
  sketch-geometry (4):
    g0: LineSegment StartX=118 StartY=39.2 StartZ=0 EndX=129 EndY=39.2 EndZ=0
    g1: LineSegment StartX=120.599 StartY=31.2 StartZ=0 EndX=131.599 EndY=31.2 EndZ=0
    g2: LineSegment StartX=129 StartY=39.2 StartZ=0 EndX=131.599 EndY=31.2 EndZ=0
    g3: LineSegment StartX=118 StartY=39.2 StartZ=0 EndX=120.599 EndY=31.2 EndZ=0
  constraints (12):
    c: PointOnObject(g0,g-3)
    c: PointOnObject(g0,g-3)
    c: DistanceX(g0,g0) = 11
    c: Horizontal(g1)
    c: Equal(g1,g0)
    c: Coincident(g2,g0)
    c: Coincident(g3,g0)
    c: Parallel(g-4,g2)
    c: Coincident(g1,g2)
    c: Coincident(g1,g3)
    c: DistanceY(g1,g0) = 8
    c: DistanceX(g-3,g0) = 118
FEATURE [Sketcher::SketchObject] Sketch099
  ArcFitTolerance = 1e-06
  AttachmentSupport = -> [Pad008]
  ExternalGeometry = -> [Binder]
  FullyConstrained = true
  MakeInternals = false
  MapMode = 5
  Placement = pos=(0,3.6,0) rot=(0,0.707107,0.707107;3.14159rad)
  sketch-geometry (13):
    g0: LineSegment StartX=192.176 StartY=-3.18451 StartZ=0 EndX=196.804 EndY=-13.1108 EndZ=0
    g1: LineSegment [constr] StartX=202.765 StartY=20.303 StartZ=0 EndX=181.223 EndY=20.303 EndZ=0
    g2: LineSegment [constr] StartX=181.223 StartY=20.303 StartZ=0 EndX=181.223 EndY=-3.18451 EndZ=0
    g3: ArcOfCircle CenterX=181.223 CenterY=-20.3764 CenterZ=0 NormalX=0 NormalY=0 NormalZ=1 AngleXU=0 Radius=17.1918 StartAngle=0.436332 EndAngle=1.57079
    g4: ArcOfEllipse CenterX=181.223 CenterY=8.55923 CenterZ=0 NormalX=0 NormalY=0 NormalZ=1 MajorRadius=23.4779 MinorRadius=11.7437 AngleXU=0 StartAngle=1.5708 EndAngle=4.71239
    g5: LineSegment [constr] StartX=204.701 StartY=8.55923 StartZ=0 EndX=157.745 EndY=8.55923 EndZ=0
    g6: LineSegment [constr] StartX=181.223 StartY=20.303 StartZ=0 EndX=181.223 EndY=-3.18451 EndZ=0
    g7: GeomPoint [constr] X=201.553 Y=8.55923 Z=0
    g8: GeomPoint [constr] X=160.894 Y=8.55923 Z=0
    g9: GeomPoint [constr] X=181.223 Y=-3.18451 Z=0
    g10: LineSegment StartX=181.223 StartY=20.303 StartZ=0 EndX=202.765 EndY=20.303 EndZ=0
    g11: ArcOfCircle CenterX=207.583 CenterY=4 CenterZ=0 NormalX=0 NormalY=0 NormalZ=1 AngleXU=0 Radius=17 StartAngle=1.85815 EndAngle=3.57792
    g12: LineSegment [constr] StartX=172.411 StartY=39.2 StartZ=0 EndX=192.176 EndY=-3.18451 EndZ=0
  constraints (27):
    c: Coincident(g1,g-7)
    c: Horizontal(g1)
    c: Coincident(g2,g1)
    c: Vertical(g2)
    c: Horizontal(g2,g0)
    c: Coincident(g3,g0)
    c: Coincident(g3,g2)
    c: InternalAlignment(g5-g8 -> g4) x4
    c: Horizontal(g5)
    c: PointOnObject(g4,g2)
    c: Coincident(g4,g1)
    c: DistanceX(g-3,g5) = 10.1
    c: Coincident(g4,g2)
    c: Tangent(g3,g-5)
    c: PointOnObject(g9,g4)
    c: PointOnObject(g9,g3)
    c: Tangent(g4,g3,g9) = 1.5708
    c: Coincident(g10,g1)
    c: Coincident(g10,g1)
    c: Equal(g11,g-4)
    c: Coincident(g11,g1)
    c: Coincident(g11,g0)
    c: PointOnObject(g12,g-6)
    c: PointOnObject(g1,g12)
    c: Tangent(g12,g-5) = -1.5708
    c: Tangent(g0,g-5) = -1.5708
    c: Horizontal(g9,g12)
FEATURE [Sketcher::SketchObject] Sketch106  label="Sketch106 - smusso impuniatura interno"
  ArcFitTolerance = 1e-06
  AttachmentSupport = -> [Pad008]
  ExternalGeometry = -> [Pad008]
  FullyConstrained = true
  MakeInternals = false
  MapMode = 5
  Placement = pos=(0,-1.586e-13,-80.4316) rot=(1,0,0;3.14159rad)
  sketch-geometry (9):
    g0: LineSegment StartX=-176.685 StartY=-3.6 StartZ=0 EndX=-176.685 EndY=-1.91e-13 EndZ=0
    g1: LineSegment [constr] StartX=-176.685 StartY=-1.416e-13 StartZ=0 EndX=-176.685 EndY=-1.909e-13 EndZ=0
    g2: LineSegment [constr] StartX=-186.685 StartY=-3.6 StartZ=0 EndX=-186.685 EndY=-1.91e-13 EndZ=0
    g3: ArcOfEllipse CenterX=-186.685 CenterY=-1.909e-13 CenterZ=0 NormalX=0 NormalY=0 NormalZ=1 MajorRadius=10 MinorRadius=3.6 AngleXU=3.14159 StartAngle=1.5708 EndAngle=3.14159
    g4: LineSegment [constr] StartX=-196.685 StartY=-1.416e-13 StartZ=0 EndX=-176.685 EndY=-1.416e-13 EndZ=0
    g5: LineSegment [constr] StartX=-186.685 StartY=-3.6 StartZ=0 EndX=-186.685 EndY=3.6 EndZ=0
    g6: GeomPoint [constr] X=-196.015 Y=-1.399e-13 Z=0
    g7: GeomPoint [constr] X=-177.356 Y=-1.416e-13 Z=0
    g8: LineSegment StartX=-176.685 StartY=-3.6 StartZ=0 EndX=-186.685 EndY=-3.6 EndZ=0
  constraints (15):
    c: PointOnObject(g2,g-3)
    c: Coincident(g1,g-5)
    c: DistanceY(g1,g1) = 0
    c: Coincident(g0,g1)
    c: DistanceX(g2,g-5) = 10
    c: Vertical(g2)
    c: Horizontal(g2,g0)
    c: InternalAlignment(g4-g7 -> g3) x4
    c: Coincident(g3,g2)
    c: Horizontal(g4)
    c: Coincident(g3,g0)
    c: Tangent(g0,g-5) = 1.5708
    c: Coincident(g3,g2)
    c: Coincident(g8,g0)
    c: Coincident(g8,g2)
FEATURE [Sketcher::SketchObject] Sketch107  label="Sketch107 - smusso impugnatura esterno"
  ArcFitTolerance = 1e-06
  AttachmentSupport = -> [Pad008]
  ExternalGeometry = -> [Pad008]
  FullyConstrained = true
  MakeInternals = false
  MapMode = 5
  Placement = pos=(0,-1.586e-13,-80.4316) rot=(1,0,0;3.14159rad)
  sketch-geometry (9):
    g0: LineSegment [constr] StartX=-215.932 StartY=1.79e-14 StartZ=0 EndX=-215.932 EndY=2.42e-14 EndZ=0
    g1: LineSegment StartX=-215.932 StartY=-3.6 StartZ=0 EndX=-215.932 EndY=2.44e-14 EndZ=0
    g2: LineSegment StartX=-215.932 StartY=-3.6 StartZ=0 EndX=-205.932 EndY=-3.6 EndZ=0
    g3: LineSegment [constr] StartX=-205.932 StartY=-3.6 StartZ=0 EndX=-205.932 EndY=2.44e-14 EndZ=0
    g4: ArcOfEllipse CenterX=-205.932 CenterY=2.42e-14 CenterZ=0 NormalX=0 NormalY=0 NormalZ=1 MajorRadius=10 MinorRadius=3.6 AngleXU=3.14159 StartAngle=1e-16 EndAngle=1.5708
    g5: LineSegment [constr] StartX=-215.932 StartY=1.79e-14 StartZ=0 EndX=-195.932 EndY=1.79e-14 EndZ=0
    g6: LineSegment [constr] StartX=-205.932 StartY=-3.6 StartZ=0 EndX=-205.932 EndY=3.6 EndZ=0
    g7: GeomPoint [constr] X=-215.262 Y=2.45e-14 Z=0
    g8: GeomPoint [constr] X=-196.602 Y=1.78e-14 Z=0
  constraints (16):
    c: Coincident(g0,g-6)
    c: PointOnObject(g0,g-6)
    c: DistanceY(g0,g0) = 0
    c: Coincident(g1,g-6)
    c: Coincident(g1,g0)
    c: Tangent(g2,g-3)
    c: DistanceX(g2,g2) = 10
    c: Coincident(g3,g2)
    c: Vertical(g3)
    c: Horizontal(g3,g0)
    c: InternalAlignment(g5-g8 -> g4) x4
    c: Coincident(g4,g3)
    c: Horizontal(g5)
    c: Coincident(g4,g0)
    c: Coincident(g4,g2)
    c: PointOnObject(g2,g1)
FEATURE [Sketcher::SketchObject] Sketch108
  ArcFitTolerance = 1e-06
  AttachmentOffset = pos=(0,0,-1.6) rot=(0,0,1;0rad)
  AttachmentSupport = -> [Pad008]
  ExternalGeometry = -> [Binder]
  FullyConstrained = true
  MakeInternals = false
  MapMode = 5
  Placement = pos=(0,2,4e-16) rot=(0,0.707107,0.707107;3.14159rad)
  sketch-geometry (14):
    g0: LineSegment StartX=192.176 StartY=-3.18451 StartZ=0 EndX=193.827 EndY=-6.72678 EndZ=0
    g1: LineSegment [constr] StartX=202.765 StartY=20.303 StartZ=0 EndX=181.223 EndY=20.303 EndZ=0
    g2: LineSegment [constr] StartX=181.223 StartY=20.303 StartZ=0 EndX=181.223 EndY=1.30297 EndZ=0
    g3: ArcOfCircle CenterX=181.223 CenterY=-12.6042 CenterZ=0 NormalX=0 NormalY=0 NormalZ=1 AngleXU=0 Radius=13.9072 StartAngle=0.436332 EndAngle=1.5708
    g4: ArcOfEllipse CenterX=181.223 CenterY=10.803 CenterZ=0 NormalX=0 NormalY=0 NormalZ=1 MajorRadius=14.4779 MinorRadius=9.5 AngleXU=0 StartAngle=1.5708 EndAngle=4.71239
    g5: LineSegment [constr] StartX=195.701 StartY=10.803 StartZ=0 EndX=166.745 EndY=10.803 EndZ=0
    g6: LineSegment [constr] StartX=181.223 StartY=20.303 StartZ=0 EndX=181.223 EndY=1.30297 EndZ=0
    g7: GeomPoint [constr] X=192.148 Y=10.803 Z=0
    g8: GeomPoint [constr] X=170.298 Y=10.803 Z=0
    g9: LineSegment StartX=181.223 StartY=20.303 StartZ=0 EndX=202.765 EndY=20.303 EndZ=0
    g10: ArcOfCircle CenterX=207.583 CenterY=4 CenterZ=0 NormalX=0 NormalY=0 NormalZ=1 AngleXU=0 Radius=17 StartAngle=1.85815 EndAngle=3.57792
    g11: LineSegment [constr] StartX=172.411 StartY=39.2 StartZ=0 EndX=192.176 EndY=-3.18451 EndZ=0
    g12: GeomPoint [constr] X=181.223 Y=1.30297 Z=0
    g13: GeomPoint [constr] X=181.223 Y=1.30297 Z=0
  constraints (28):
    c: Coincident(g1,g-7)
    c: Horizontal(g1)
    c: Coincident(g2,g1)
    c: Vertical(g2)
    c: Coincident(g3,g2)
    c: InternalAlignment(g5-g8 -> g4) x4
    c: Horizontal(g5)
    c: PointOnObject(g4,g2)
    c: Coincident(g4,g1)
    c: DistanceX(g-3,g5) = 19.1
    c: Coincident(g4,g2)
    c: Coincident(g9,g1)
    c: Coincident(g9,g1)
    c: Coincident(g10,g1)
    c: Coincident(g10,g0)
    c: PointOnObject(g11,g-6)
    c: PointOnObject(g1,g11)
    c: DistanceY(g2,g1) = 19
    c: Coincident(g10,g-4)
    c: PointOnObject(g12,g4)
    c: PointOnObject(g12,g3)
    c: Tangent(g11,g-5) = -1.5708
    c: Tangent(g0,g-5) = -1.5708
    c: Tangent(g3,g0) = 1.5708
    c: PointOnObject(g13,g4)
    c: PointOnObject(g13,g3)
    c: Tangent(g4,g3,g13) = 1.5708
    c: Horizontal(g11,g0)
FEATURE [Part::Part2DObjectPython] Clone2D  label="Sketch108 (2D)"  # Draft 2D object (typed FeaturePython)
  Fuse = false
  Objects = -> [Sketch108]
  Placement = pos=(0,2,4e-16) rot=(0,0.707107,0.707107;3.14159rad)
  Scale = (1,1,1)
FEATURE [Sketcher::SketchObject] Sketch109
  ArcFitTolerance = 1e-06
  AttachmentOffset = pos=(0,0,-3.5) rot=(0,0,1;0rad)
  AttachmentSupport = -> [Pad008]
  ExternalGeometry = -> [Binder]
  FullyConstrained = true
  MakeInternals = false
  MapMode = 5
  Placement = pos=(0,0.1,8e-16) rot=(0,0.707107,0.707107;3.14159rad)
  sketch-geometry (1):
    g0: GeomPoint X=197.47 Y=8.55923 Z=0
  constraints (1):
    c: Symmetric(g-7,g-5,g0)
FEATURE [PartDesign::Chamfer] Chamfer005
  Angle = 45
  Base = -> Pad009 [Edge215,Edge212]
  BaseFeature = -> Pad009
  ChamferType = 1
  FlipDirection = false
  Refine = true
  Size = 1.5
  Size2 = 2.8
  SupportTransform = false
  Suppressed = false
  UseAllEdges = false
FEATURE [Sketcher::SketchObject] Sketch111
  ArcFitTolerance = 1e-06
  AttachmentSupport = -> [Pad009]
  ExternalGeometry = -> [Pad009]
  FullyConstrained = true
  MakeInternals = false
  MapMode = 5
  Placement = pos=(0,3.6,-8e-16) rot=(0,0.707107,0.707107;3.14159rad)
  sketch-geometry (21):
    g0: LineSegment [constr] StartX=97 StartY=36.8 StartZ=0 EndX=97 EndY=26.8 EndZ=0
    g1: LineSegment StartX=97 StartY=28.6 StartZ=0 EndX=97 EndY=27.8 EndZ=0
    g2: LineSegment StartX=97 StartY=27.8 StartZ=0 EndX=108 EndY=27.8 EndZ=0
    g3: LineSegment StartX=108 StartY=27.8 StartZ=0 EndX=108 EndY=28.6 EndZ=0
    g4: LineSegment StartX=108 StartY=28.6 StartZ=0 EndX=97 EndY=28.6 EndZ=0
    g5: LineSegment StartX=97 StartY=35.8 StartZ=0 EndX=97 EndY=35 EndZ=0
    g6: LineSegment StartX=97 StartY=35 StartZ=0 EndX=108 EndY=35 EndZ=0
    g7: LineSegment StartX=108 StartY=35 StartZ=0 EndX=108 EndY=35.8 EndZ=0
    g8: LineSegment StartX=108 StartY=35.8 StartZ=0 EndX=97 EndY=35.8 EndZ=0
    g9: LineSegment StartX=97 StartY=30.4 StartZ=0 EndX=97 EndY=29.6 EndZ=0
    g10: LineSegment StartX=97 StartY=29.6 StartZ=0 EndX=108 EndY=29.6 EndZ=0
    g11: LineSegment StartX=108 StartY=29.6 StartZ=0 EndX=108 EndY=30.4 EndZ=0
    g12: LineSegment StartX=108 StartY=30.4 StartZ=0 EndX=97 EndY=30.4 EndZ=0
    g13: LineSegment StartX=97 StartY=34 StartZ=0 EndX=97 EndY=33.2 EndZ=0
    g14: LineSegment StartX=97 StartY=33.2 StartZ=0 EndX=108 EndY=33.2 EndZ=0
    g15: LineSegment StartX=108 StartY=33.2 StartZ=0 EndX=108 EndY=34 EndZ=0
    g16: LineSegment StartX=108 StartY=34 StartZ=0 EndX=97 EndY=34 EndZ=0
    g17: LineSegment StartX=97 StartY=32.2 StartZ=0 EndX=97 EndY=31.4 EndZ=0
    g18: LineSegment StartX=97 StartY=31.4 StartZ=0 EndX=108 EndY=31.4 EndZ=0
    g19: LineSegment StartX=108 StartY=31.4 StartZ=0 EndX=108 EndY=32.2 EndZ=0
    g20: LineSegment StartX=108 StartY=32.2 StartZ=0 EndX=97 EndY=32.2 EndZ=0
  constraints (54):
    c: Vertical(g0)
    c: PointOnObject(g0,g-3)
    c: PointOnObject(g0,g-4)
    c: DistanceX(g0,g-5) = 11
    c: Coincident(g1,g2)
    c: Coincident(g2,g3)
    c: Coincident(g3,g4)
    c: Coincident(g4,g1)
    c: Horizontal(g2)
    c: Horizontal(g4)
    c: Tangent(g1,g0)
    c: Tangent(g3,g-5)
    c: DistanceY(g2,g3) = 0.8
    c: Coincident(g5,g6)
    c: Coincident(g6,g7)
    c: Coincident(g7,g8)
    c: Coincident(g8,g5)
    c: Horizontal(g6)
    c: Horizontal(g8)
    c: DistanceY(g6,g7) = 0.8
    c: Coincident(g9,g10)
    c: Coincident(g10,g11)
    c: Coincident(g11,g12)
    c: Coincident(g12,g9)
    c: Horizontal(g10)
    c: Horizontal(g12)
    c: DistanceY(g10,g11) = 0.8
    c: Tangent(g5,g0)
    c: Tangent(g7,g-5)
    c: Tangent(g9,g0)
    c: Tangent(g11,g-5)
    c: Coincident(g13,g14)
    c: Coincident(g14,g15)
    c: Coincident(g15,g16)
    c: Coincident(g16,g13)
    c: Horizontal(g14)
    c: Horizontal(g16)
    c: DistanceY(g14,g15) = 0.8
    c: Tangent(g13,g0)
    c: Tangent(g15,g-5)
    c: Coincident(g17,g18)
    c: Coincident(g18,g19)
    c: Coincident(g19,g20)
    c: Coincident(g20,g17)
    c: Horizontal(g18)
    c: Horizontal(g20)
    c: DistanceY(g18,g19) = 0.8
    c: Tangent(g17,g0)
    c: Tangent(g19,g-5)
    c: DistanceY(g1,g9) = 1
    c: DistanceY(g9,g17) = 1
    c: DistanceY(g17,g13) = 1
    c: DistanceY(g13,g5) = 1
    c: DistanceY(g0,g1) = 1
FEATURE [PartDesign::Pocket] Pocket004
  BaseFeature = -> Chamfer005
  Direction = (0,-1,2e-16)
  Length = 1
  Length2 = 5
  Profile = -> Sketch111
  ReferenceAxis = -> Sketch111 [N_Axis]
  Refine = true
  Suppressed = false
  Type = 0
FEATURE [PartDesign::Pad] Pad010
  BaseFeature = -> Pocket004
  Direction = (0,1,-2e-16)
  Length = 1.2
  Length2 = 10
  Profile = -> Sketch098
  ReferenceAxis = -> Sketch098 [N_Axis]
  Refine = true
  Suppressed = false
  Type = 0
FEATURE [PartDesign::Chamfer] Chamfer006
  Angle = 45
  Base = -> Pad010 [Edge291]
  BaseFeature = -> Pad010
  ChamferType = 1
  FlipDirection = false
  Refine = true
  Size = 1
  Size2 = 6
  SupportTransform = false
  Suppressed = false
  UseAllEdges = false
FEATURE [Sketcher::SketchObject] Sketch110
  ArcFitTolerance = 1e-06
  AttachmentSupport = -> [Pad010]
  ExternalGeometry = -> [Sketch098]
  FullyConstrained = true
  MakeInternals = false
  MapMode = 5
  Placement = pos=(0,4,-9e-16) rot=(0,0.707107,0.707107;3.14159rad)
  sketch-geometry (8):
    g0: LineSegment StartX=119.69 StartY=34 StartZ=0 EndX=130.69 EndY=34 EndZ=0
    g1: LineSegment StartX=119.95 StartY=33.2 StartZ=0 EndX=130.95 EndY=33.2 EndZ=0
    g2: LineSegment StartX=119.137 StartY=35.7 StartZ=0 EndX=130.137 EndY=35.7 EndZ=0
    g3: LineSegment StartX=118.877 StartY=36.5 StartZ=0 EndX=129.877 EndY=36.5 EndZ=0
    g4: LineSegment StartX=118.877 StartY=36.5 StartZ=0 EndX=119.137 EndY=35.7 EndZ=0
    g5: LineSegment StartX=129.877 StartY=36.5 StartZ=0 EndX=130.137 EndY=35.7 EndZ=0
    g6: LineSegment StartX=119.69 StartY=34 StartZ=0 EndX=119.95 EndY=33.2 EndZ=0
    g7: LineSegment StartX=130.69 StartY=34 StartZ=0 EndX=130.95 EndY=33.2 EndZ=0
  constraints (24):
    c: Horizontal(g0)
    c: Horizontal(g1)
    c: Horizontal(g2)
    c: Horizontal(g3)
    c: Equal(g1,g-5)
    c: Equal(g0,g-5)
    c: Equal(g2,g-5)
    c: Equal(g3,g-5)
    c: PointOnObject(g0,g-3)
    c: PointOnObject(g1,g-3)
    c: PointOnObject(g2,g-3)
    c: PointOnObject(g3,g-3)
    c: Coincident(g4,g3)
    c: Coincident(g4,g2)
    c: Coincident(g5,g3)
    c: Coincident(g5,g2)
    c: Coincident(g6,g0)
    c: Coincident(g6,g1)
    c: Coincident(g7,g0)
    c: Coincident(g7,g1)
    c: DistanceY(g1,g0) = 0.8
    c: DistanceY(g2,g3) = 0.8
    c: DistanceY(g-5,g1) = 2
    c: DistanceY(g-5,g2) = 4.5
FEATURE [PartDesign::Pocket] Pocket003
  BaseFeature = -> Chamfer006
  Direction = (0,-1,2e-16)
  Length = 1
  Length2 = 5
  Profile = -> Sketch110
  ReferenceAxis = -> Sketch110 [N_Axis]
  Refine = true
  Suppressed = false
  Type = 0
FEATURE [PartDesign::SubtractivePipe] SubtractivePipe
  AuxilleryCurvelinear = true
  AuxillerySpineTangent = false
  BaseFeature = -> Pocket003
  Binormal = (0,0,0)
  Mode = 0
  Profile = -> Sketch106
  Refine = true
  Spine = -> Pad008 [Edge215]
  SpineTangent = false
  Suppressed = false
  Transformation = 0
  Transition = 0
FEATURE [PartDesign::SubtractivePipe] SubtractivePipe001
  AuxilleryCurvelinear = true
  AuxillerySpineTangent = false
  BaseFeature = -> SubtractivePipe
  Binormal = (0,0,0)
  Mode = 0
  Profile = -> Sketch107
  Refine = true
  Spine = -> Pad008 [Edge213,Edge216,Edge210]
  SpineTangent = false
  Suppressed = false
  Transformation = 0
  Transition = 0
FEATURE [PartDesign::SubtractiveLoft] SubtractiveLoft
  BaseFeature = -> SubtractivePipe001
  Closed = false
  Profile = -> Sketch099
  Refine = true
  Ruled = false
  Sections = -> [Sketch108]
  Suppressed = false
FEATURE [PartDesign::SubtractiveLoft] SubtractiveLoft001
  BaseFeature = -> SubtractiveLoft
  Closed = false
  Profile = -> Clone2D
  Refine = true
  Ruled = false
  Sections = -> [Sketch109]
  Suppressed = false
FEATURE [Sketcher::SketchObject] Sketch112
  ArcFitTolerance = 1e-06
  AttachmentSupport = -> [Pad008]
  ExternalGeometry = -> [Binder]
  FullyConstrained = true
  MakeInternals = false
  MapMode = 5
  Placement = pos=(0,3.6,0) rot=(0,0.707107,0.707107;3.14159rad)
  sketch-geometry (4):
    g0: LineSegment [constr] StartX=167.782 StartY=-53.0314 StartZ=0 EndX=215.42 EndY=-53.0314 EndZ=0
    g1: GeomPoint [constr] X=191.282 Y=-53.0314 Z=0
    g2: Circle CenterX=191.282 CenterY=-53.0314 CenterZ=0 NormalX=0 NormalY=0 NormalZ=1 AngleXU=0 Radius=11.5
    g3: Circle CenterX=191.282 CenterY=-53.0314 CenterZ=0 NormalX=0 NormalY=0 NormalZ=1 AngleXU=0 Radius=10.7
  constraints (9):
    c: Horizontal(g0)
    c: PointOnObject(g0,g-3)
    c: Diameter(g2) = 23
    c: Coincident(g2,g1)
    c: Diameter(g3) = 21.4
    c: Coincident(g3,g1)
    c: DistanceX(g0,g1) = 23.5
    c: PointOnObject(g1,g0)
    c: Coincident(g0,g-4)
FEATURE [PartDesign::Chamfer] Chamfer016
  Angle = 45
  Base = -> SubtractiveLoft001 [Edge118,Edge117,Edge119,Edge120,Edge109]
  BaseFeature = -> SubtractiveLoft001
  ChamferType = 0
  FlipDirection = false
  Refine = true
  Size = 1.5
  Size2 = 1
  SupportTransform = false
  Suppressed = false
  UseAllEdges = false
FEATURE [PartDesign::Chamfer] Chamfer017
  Angle = 45
  Base = -> Chamfer016 [Edge15]
  BaseFeature = -> Chamfer016
  ChamferType = 0
  FlipDirection = false
  Refine = true
  Size = 1.6
  Size2 = 1
  SupportTransform = false
  Suppressed = false
  UseAllEdges = false
FEATURE [PartDesign::Chamfer] Chamfer018
  Angle = 45
  Base = -> Chamfer017 [Edge10]
  BaseFeature = -> Chamfer017
  ChamferType = 0
  FlipDirection = false
  Refine = true
  Size = 3.5
  Size2 = 1
  SupportTransform = false
  Suppressed = false
  UseAllEdges = false
FEATURE [PartDesign::Chamfer] Chamfer019
  Angle = 45
  Base = -> Chamfer018 [Edge94,Edge199]
  BaseFeature = -> Chamfer018
  ChamferType = 0
  FlipDirection = false
  Refine = true
  Size = 1.9
  Size2 = 1
  SupportTransform = false
  Suppressed = false
  UseAllEdges = false
FEATURE [PartDesign::Fillet] Fillet009
  Base = -> Chamfer019 [Edge83]
  BaseFeature = -> Chamfer019
  Radius = 1.1
  Refine = true
  SupportTransform = false
  Suppressed = false
  UseAllEdges = false
FEATURE [PartDesign::Fillet] Fillet010
  Base = -> Fillet009 [Edge77]
  BaseFeature = -> Fillet009
  Radius = 1.9
  Refine = true
  SupportTransform = false
  Suppressed = false
  UseAllEdges = false
FEATURE [PartDesign::Pocket] Pocket005
  BaseFeature = -> Fillet010
  Direction = (0,-1,2e-16)
  Length = 0.8
  Length2 = 5
  Profile = -> Sketch112
  ReferenceAxis = -> Sketch112 [N_Axis]
  Refine = true
  Suppressed = false
  Type = 0
FEATURE [Part::Part2DObjectPython] ShapeString001  # Draft 2D object (typed FeaturePython)
  FontFile = <path>
  Fuse = false
  Justification = 6
  JustificationReference = 0
  KeepLeftMargin = false
  MakeFace = true
  ObliqueAngle = 0
  Placement = pos=(-183.5,3.6,-57.5) rot=(0,0.707107,0.707107;3.14159rad)
  ScaleToSize = true
  Size = 10
  String = AS
  Tracking = 0
FEATURE [PartDesign::Pocket] Pocket013
  BaseFeature = -> Pocket005
  Direction = (-1e-16,-1,2e-16)
  Length = 1
  Length2 = 5
  Profile = -> ShapeString001
  ReferenceAxis = -> ShapeString001 [N_Axis]
  Refine = true
  Suppressed = false
  Type = 0
FEATURE [PartDesign::Body] Body006  label="lato SX"
  AllowCompound = false
  Group = -> [Binder,Pad019,Chamfer015,Pocket002,Sketch133,Sketch091,Pad005,Sketch092,Pocket001,Sketch093,Sketch094,Pad006,Sketch095,Pad007,Sketch096,Pad008,Sketch097,Pad009,Chamfer005,Pocket004,Sketch098,Pad010,Chamfer006,Pocket003,SubtractivePipe,SubtractivePipe001,Sketch099,Sketch106,Sketch107,Sketch108,Clone2D,Sketch109,SubtractiveLoft,SubtractiveLoft001,Sketch110,Sketch111,Sketch112,Chamfer016,Chamfer017,+7 more]
  Origin = -> Origin006
  Tip = -> Pocket013
FEATURE [PartDesign::Pad] Pad020
  Direction = (0,-1,2e-16)
  Length = 25.2
  Length2 = 10
  Midplane = true
  Placement = pos=(0,0,0) rot=(1,0,0;1.5708rad)
  Profile = -> Sketch021
  ReferenceAxis = -> Sketch021 [N_Axis]
  Refine = true
  Suppressed = false
  Type = 0
FEATURE [PartDesign::Body] Body001  label="perno fermo rumble e driver solenoide"
  AllowCompound = false
  Group = -> [Sketch021,Pad020]
  Origin = -> Origin001
  Tip = -> Pad020
FEATURE [PartDesign::Pad] Pad021
  Direction = (0,-1,2e-16)
  Length = 16.8
  Length2 = 10
  Midplane = true
  Placement = pos=(0,0,0) rot=(1,0,0;1.5708rad)
  Profile = -> Sketch061
  ReferenceAxis = -> Sketch061 [N_Axis]
  Refine = true
  Suppressed = false
  Type = 0
FEATURE [PartDesign::Pocket] Pocket014
  BaseFeature = -> Pad021
  Direction = (0,1,-2e-16)
  Length = 12.8
  Length2 = 5
  Midplane = true
  Placement = pos=(0,0,0) rot=(1,0,0;1.5708rad)
  Profile = -> Sketch062
  ReferenceAxis = -> Sketch062 [N_Axis]
  Refine = true
  Suppressed = false
  Type = 0
FEATURE [PartDesign::Pad] Pad022
  BaseFeature = -> Pocket014
  Direction = (0,-1,2e-16)
  Length = 7.6
  Length2 = 10
  Midplane = true
  Placement = pos=(0,0,0) rot=(1,0,0;1.5708rad)
  Profile = -> Sketch063
  ReferenceAxis = -> Sketch063 [N_Axis]
  Refine = true
  Suppressed = false
  Type = 0
FEATURE [PartDesign::Body] Body003  label="blocco switch"
  AllowCompound = false
  Group = -> [Sketch061,Sketch062,Sketch063,Pad021,Pocket014,Pad022]
  Origin = -> Origin003
  Tip = -> Pad022
FEATURE [PartDesign::Pad] Pad024
  Direction = (0,-1,2e-16)
  Length = 17
  Length2 = 10
  Midplane = true
  Placement = pos=(0,0,0) rot=(1,0,0;1.5708rad)
  Profile = -> Sketch045
  ReferenceAxis = -> Sketch045 [N_Axis]
  Refine = true
  Suppressed = false
  Type = 0
FEATURE [PartDesign::Pocket] Pocket015
  BaseFeature = -> Pad024
  Direction = (-1,0,0)
  Length = 8
  Length2 = 5
  Placement = pos=(0,0,0) rot=(1,0,0;1.5708rad)
  Profile = -> Sketch047
  ReferenceAxis = -> Sketch047 [N_Axis]
  Refine = true
  Reversed = true
  Suppressed = false
  Type = 0
FEATURE [PartDesign::Pocket] Pocket016
  BaseFeature = -> Pocket015
  Direction = (-1,0,0)
  Length = 1
  Length2 = 5
  Placement = pos=(0,0,0) rot=(1,0,0;1.5708rad)
  Profile = -> Sketch046
  ReferenceAxis = -> Sketch046 [N_Axis]
  Refine = true
  Reversed = true
  Suppressed = false
  Type = 0
FEATURE [PartDesign::Pocket] Pocket017
  BaseFeature = -> Pocket016
  Direction = (0,1,-2e-16)
  Length = 17
  Length2 = 5
  Midplane = true
  Placement = pos=(0,0,0) rot=(1,0,0;1.5708rad)
  Profile = -> Sketch048
  ReferenceAxis = -> Sketch048 [N_Axis]
  Refine = true
  Suppressed = false
  Type = 0
FEATURE [PartDesign::Pad] Pad025
  BaseFeature = -> Pocket017
  Direction = (0,-1,2e-16)
  Length = 17
  Length2 = 10
  Midplane = true
  Placement = pos=(0,0,0) rot=(1,0,0;1.5708rad)
  Profile = -> Sketch049
  ReferenceAxis = -> Sketch049 [N_Axis]
  Refine = true
  Suppressed = false
  Type = 0
FEATURE [PartDesign::Pad] Pad026
  BaseFeature = -> Pad025
  Direction = (0,-1,2e-16)
  Length = 17
  Length2 = 10
  Midplane = true
  Placement = pos=(0,0,0) rot=(1,0,0;1.5708rad)
  Profile = -> Sketch066
  ReferenceAxis = -> Sketch066 [N_Axis]
  Refine = true
  Suppressed = false
  Type = 0
FEATURE [PartDesign::Pad] Pad027
  BaseFeature = -> Pad026
  Direction = (0,-1,2e-16)
  Length = 5
  Length2 = 10
  Midplane = true
  Placement = pos=(0,0,0) rot=(1,0,0;1.5708rad)
  Profile = -> Sketch064
  ReferenceAxis = -> Sketch064 [N_Axis]
  Refine = true
  Suppressed = false
  Type = 0
FEATURE [PartDesign::Pad] Pad028
  BaseFeature = -> Pad027
  Direction = (1,0,0)
  Length = 1
  Length2 = 10
  Placement = pos=(0,0,0) rot=(1,0,0;1.5708rad)
  Profile = -> Sketch068
  ReferenceAxis = -> Sketch068 [N_Axis]
  Refine = true
  Reversed = true
  Suppressed = false
  Type = 0
FEATURE [PartDesign::Chamfer] Chamfer020
  Angle = 45
  Base = -> Pad028 [Edge73,Edge75,Edge78,Edge77]
  BaseFeature = -> Pad028
  ChamferType = 0
  FlipDirection = false
  Placement = pos=(0,0,0) rot=(1,0,0;1.5708rad)
  Refine = true
  Size = 0.5
  Size2 = 1
  SupportTransform = false
  Suppressed = false
  UseAllEdges = false
FEATURE [PartDesign::Body] Body002  label="supporto per neopixel"
  AllowCompound = false
  Group = -> [Sketch045,Sketch047,Sketch046,Sketch048,Sketch049,Sketch066,Sketch064,Sketch068,Pad024,Pocket015,Pocket016,Pocket017,Pad025,Pad026,Pad027,Pad028,Chamfer020]
  Origin = -> Origin002
  Tip = -> Chamfer020
FEATURE [Sketcher::SketchObject] Sketch134  label="perno fermo rumble002"
  ArcFitTolerance = 1e-06
  AttachmentSupport = -> [XZ_Plane008]
  FullyConstrained = true
  MakeInternals = false
  MapMode = 5
  Placement = pos=(0,0,0) rot=(1,0,0;1.5708rad)
  sketch-geometry (16):
    g0: LineSegment StartX=0 StartY=0.45 StartZ=0 EndX=0 EndY=1.55 EndZ=0
    g1: LineSegment StartX=0.45 StartY=2 StartZ=0 EndX=1.55 EndY=2 EndZ=0
    g2: LineSegment StartX=2 StartY=1.55 StartZ=0 EndX=2 EndY=0.45 EndZ=0
    g3: LineSegment StartX=1.55 StartY=0 StartZ=0 EndX=0.45 EndY=0 EndZ=0
    g4: ArcOfCircle [constr] CenterX=0.45 CenterY=1.55 CenterZ=0 NormalX=0 NormalY=0 NormalZ=1 AngleXU=0 Radius=0.45 StartAngle=1.5708 EndAngle=3.14159
    g5: GeomPoint [constr] X=0 Y=2 Z=0
    g6: LineSegment StartX=0.45 StartY=2 StartZ=0 EndX=0 EndY=1.55 EndZ=0
    g7: ArcOfCircle [constr] CenterX=1.55 CenterY=1.55 CenterZ=0 NormalX=0 NormalY=0 NormalZ=1 AngleXU=0 Radius=0.45 StartAngle=0 EndAngle=1.5708
    g8: GeomPoint [constr] X=2 Y=2 Z=0
    g9: LineSegment StartX=2 StartY=1.55 StartZ=0 EndX=1.55 EndY=2 EndZ=0
    g10: ArcOfCircle [constr] CenterX=1.55 CenterY=0.45 CenterZ=0 NormalX=0 NormalY=0 NormalZ=1 AngleXU=0 Radius=0.45 StartAngle=4.71239 EndAngle=6.28319
    g11: GeomPoint [constr] X=2 Y=0 Z=0
    g12: LineSegment StartX=1.55 StartY=0 StartZ=0 EndX=2 EndY=0.45 EndZ=0
    g13: ArcOfCircle [constr] CenterX=0.45 CenterY=0.45 CenterZ=0 NormalX=0 NormalY=0 NormalZ=1 AngleXU=0 Radius=0.45 StartAngle=3.14159 EndAngle=4.71239
    g14: GeomPoint [constr] X=0 Y=0 Z=0
    g15: LineSegment StartX=0 StartY=0.45 StartZ=0 EndX=0.45 EndY=0 EndZ=0
  constraints (35):
    c: Coincident(g14,g-1)
    c: PointOnObject(g5,g-2)
    c: Horizontal(g1)
    c: Vertical(g2)
    c: Horizontal(g3)
    c: DistanceX(g5,g8) = 2
    c: DistanceY(g11,g8) = 2
    c: PointOnObject(g5,g0)
    c: PointOnObject(g5,g1)
    c: Tangent(g0,g4) = 1.5708
    c: Tangent(g1,g4) = 1.5708
    c: Coincident(g6,g0)
    c: Coincident(g6,g1)
    c: PointOnObject(g8,g2)
    c: PointOnObject(g8,g1)
    c: Tangent(g2,g7) = 1.5708
    c: Tangent(g1,g7) = 1.5708
    c: Coincident(g9,g2)
    c: Coincident(g9,g1)
    c: PointOnObject(g11,g2)
    c: PointOnObject(g11,g3)
    c: Tangent(g2,g10) = 1.5708
    c: Tangent(g3,g10) = 1.5708
    c: Coincident(g12,g2)
    c: Coincident(g12,g3)
    c: PointOnObject(g14,g0)
    c: PointOnObject(g14,g3)
    c: Tangent(g0,g13) = 1.5708
    c: Tangent(g3,g13) = 1.5708
    c: Coincident(g15,g0)
    c: Coincident(g15,g3)
    c: Equal(g6,g9)
    c: Equal(g9,g12)
    c: Equal(g12,g15)
    c: DistanceX(g14,g3) = 0.45
FEATURE [PartDesign::Pad] Pad029
  Direction = (0,-1,2e-16)
  Length = 17
  Length2 = 10
  Midplane = true
  Placement = pos=(0,0,0) rot=(1,0,0;1.5708rad)
  Profile = -> Sketch134
  ReferenceAxis = -> Sketch134 [N_Axis]
  Refine = true
  Suppressed = false
  Type = 0
FEATURE [PartDesign::Body] Body008  label="perno fermo neopixel"
  AllowCompound = false
  Group = -> [Sketch134,Pad029]
  Origin = -> Origin008
  Tip = -> Pad029
FEATURE [Sketcher::SketchObject] Sketch135  label="perno fermo rumble003"
  ArcFitTolerance = 1e-06
  AttachmentSupport = -> [XZ_Plane009]
  FullyConstrained = true
  MakeInternals = false
  MapMode = 5
  Placement = pos=(0,0,0) rot=(1,0,0;1.5708rad)
  sketch-geometry (16):
    g0: LineSegment StartX=4.69e-14 StartY=0.8 StartZ=0 EndX=-3.04e-14 EndY=3.1 EndZ=0
    g1: LineSegment StartX=0.8 StartY=3.9 StartZ=0 EndX=3.1 EndY=3.9 EndZ=0
    g2: LineSegment StartX=3.9 StartY=3.1 StartZ=0 EndX=3.9 EndY=0.8 EndZ=0
    g3: LineSegment StartX=3.1 StartY=0 StartZ=0 EndX=0.8 EndY=0 EndZ=0
    g4: ArcOfCircle [constr] CenterX=0.8 CenterY=3.1 CenterZ=0 NormalX=0 NormalY=0 NormalZ=1 AngleXU=0 Radius=0.8 StartAngle=1.5708 EndAngle=3.14159
    g5: GeomPoint [constr] X=0 Y=3.9 Z=0
    g6: LineSegment StartX=0.8 StartY=3.9 StartZ=0 EndX=-3.04e-14 EndY=3.1 EndZ=0
    g7: ArcOfCircle [constr] CenterX=3.1 CenterY=3.1 CenterZ=0 NormalX=0 NormalY=0 NormalZ=1 AngleXU=0 Radius=0.8 StartAngle=-2.4e-14 EndAngle=1.5708
    g8: GeomPoint [constr] X=3.9 Y=3.9 Z=0
    g9: LineSegment StartX=3.9 StartY=3.1 StartZ=0 EndX=3.1 EndY=3.9 EndZ=0
    g10: ArcOfCircle [constr] CenterX=3.1 CenterY=0.8 CenterZ=0 NormalX=0 NormalY=0 NormalZ=1 AngleXU=0 Radius=0.8 StartAngle=4.71239 EndAngle=6.28319
    g11: GeomPoint [constr] X=3.9 Y=0 Z=0
    g12: LineSegment StartX=3.1 StartY=0 StartZ=0 EndX=3.9 EndY=0.8 EndZ=0
    g13: ArcOfCircle [constr] CenterX=0.8 CenterY=0.8 CenterZ=0 NormalX=0 NormalY=0 NormalZ=1 AngleXU=0 Radius=0.8 StartAngle=3.14159 EndAngle=4.71239
    g14: GeomPoint [constr] X=0 Y=0 Z=0
    g15: LineSegment StartX=4.69e-14 StartY=0.8 StartZ=0 EndX=0.8 EndY=0 EndZ=0
  constraints (35):
    c: Coincident(g14,g-1)
    c: PointOnObject(g5,g-2)
    c: Horizontal(g1)
    c: Vertical(g2)
    c: Horizontal(g3)
    c: DistanceX(g5,g8) = 3.9
    c: DistanceY(g11,g8) = 3.9
    c: PointOnObject(g5,g0)
    c: PointOnObject(g5,g1)
    c: Tangent(g0,g4) = 1.5708
    c: Tangent(g1,g4) = 1.5708
    c: Coincident(g6,g0)
    c: Coincident(g6,g1)
    c: PointOnObject(g8,g2)
    c: PointOnObject(g8,g1)
    c: Tangent(g2,g7) = 1.5708
    c: Tangent(g1,g7) = 1.5708
    c: Coincident(g9,g2)
    c: Coincident(g9,g1)
    c: PointOnObject(g11,g2)
    c: PointOnObject(g11,g3)
    c: Tangent(g2,g10) = 1.5708
    c: Tangent(g3,g10) = 1.5708
    c: Coincident(g12,g2)
    c: Coincident(g12,g3)
    c: PointOnObject(g14,g0)
    c: PointOnObject(g14,g3)
    c: Tangent(g0,g13) = 1.5708
    c: Tangent(g3,g13) = 1.5708
    c: Coincident(g15,g0)
    c: Coincident(g15,g3)
    c: Equal(g6,g9)
    c: Equal(g9,g12)
    c: Equal(g12,g15)
    c: DistanceX(g14,g3) = 0.8
FEATURE [PartDesign::Pad] Pad030
  Direction = (0,-1,2e-16)
  Length = 25.2
  Length2 = 10
  Midplane = true
  Placement = pos=(0,0,0) rot=(1,0,0;1.5708rad)
  Profile = -> Sketch135
  ReferenceAxis = -> Sketch135 [N_Axis]
  Refine = true
  Suppressed = false
  Type = 0
FEATURE [PartDesign::Body] Body009  label="perno fermo switch - caricabatterie - grilletto"
  AllowCompound = false
  Group = -> [Sketch135,Pad030]
  Origin = -> Origin009
  Tip = -> Pad030
FEATURE [Sketcher::SketchObject] Sketch136  label="scavo_rele"
  ArcFitTolerance = 1e-06
  AttachmentSupport = -> [XZ_Plane]
  ExternalGeometry = -> [Sketch]
  FullyConstrained = true
  MakeInternals = false
  MapMode = 5
  Placement = pos=(0,0,0) rot=(1,0,0;1.5708rad)
  sketch-geometry (7):
    g0: LineSegment [constr] StartX=-168.686 StartY=-49.3292 StartZ=0 EndX=-170.664 EndY=-55.416 EndZ=0
    g1: LineSegment [constr] StartX=-168.686 StartY=-49.3292 StartZ=0 EndX=-164.882 EndY=-50.5653 EndZ=0
    g2: LineSegment [constr] StartX=-168.686 StartY=-49.3292 StartZ=0 EndX=-172.3 EndY=-48.155 EndZ=0
    g3: LineSegment StartX=-172.3 StartY=-48.155 StartZ=0 EndX=-164.882 EndY=-50.5653 EndZ=0
    g4: LineSegment StartX=-172.3 StartY=-48.155 StartZ=0 EndX=-174.278 EndY=-54.2417 EndZ=0
    g5: LineSegment StartX=-164.882 StartY=-50.5653 StartZ=0 EndX=-166.86 EndY=-56.6521 EndZ=0
    g6: LineSegment StartX=-174.278 StartY=-54.2417 StartZ=0 EndX=-166.86 EndY=-56.6521 EndZ=0
  constraints (19):
    c: Tangent(g0,g-3)
    c: Distance(g0,g-3) = 75
    c: Distance(g0,g0) = 6.4
    c: Coincident(g1,g0)
    c: Coincident(g2,g0)
    c: Distance(g2) = 3.8
    c: Distance(g1) = 4
    c: Perpendicular(g0,g1)
    c: Perpendicular(g0,g2)
    c: Coincident(g3,g2)
    c: Coincident(g3,g1)
    c: Equal(g4,g0)
    c: Equal(g5,g0)
    c: Parallel(g4,g0)
    c: Parallel(g5,g0)
    c: Coincident(g4,g2)
    c: Coincident(g5,g1)
    c: Coincident(g6,g4)
    c: Coincident(g6,g5)
FEATURE [Part::Extrusion] Extrude076  label="Extrude076 - scavo_rele"
  Base = -> Sketch136
  Dir = (0,-1,2e-16)
  DirMode = 2
  FaceMakerClass = Part::FaceMakerBullseye
  FaceMakerMode = 3
  LengthFwd = 10.4
  LengthRev = 0
  Solid = true
  Symmetric = true
FEATURE [Sketcher::SketchObject] Sketch137  label="scavo_nuovo_driver"
  ArcFitTolerance = 1e-06
  AttachmentSupport = -> [XZ_Plane]
  ExternalGeometry = -> [Sketch]
  FullyConstrained = true
  MakeInternals = false
  MapMode = 5
  Placement = pos=(0,0,0) rot=(1,0,0;1.5708rad)
  sketch-geometry (7):
    g0: LineSegment [constr] StartX=-171.776 StartY=-58.8398 StartZ=0 EndX=-175.794 EndY=-71.2035 EndZ=0
    g1: LineSegment [constr] StartX=-171.776 StartY=-58.8398 StartZ=0 EndX=-170.255 EndY=-59.3342 EndZ=0
    g2: LineSegment [constr] StartX=-171.776 StartY=-58.8398 StartZ=0 EndX=-175.39 EndY=-57.6655 EndZ=0
    g3: LineSegment StartX=-175.39 StartY=-57.6655 StartZ=0 EndX=-170.255 EndY=-59.3342 EndZ=0
    g4: LineSegment StartX=-175.39 StartY=-57.6655 StartZ=0 EndX=-179.408 EndY=-70.0293 EndZ=0
    g5: LineSegment StartX=-170.255 StartY=-59.3342 StartZ=0 EndX=-174.272 EndY=-71.698 EndZ=0
    g6: LineSegment StartX=-179.408 StartY=-70.0293 StartZ=0 EndX=-174.272 EndY=-71.698 EndZ=0
  constraints (19):
    c: Distance(g0,g-3) = 85
    c: Distance(g0) = 13
    c: Tangent(g0,g-3)
    c: Coincident(g1,g0)
    c: Coincident(g2,g0)
    c: Distance(g1) = 1.6
    c: Distance(g2) = 3.8
    c: Perpendicular(g0,g1)
    c: Perpendicular(g0,g2)
    c: Coincident(g3,g2)
    c: Coincident(g3,g1)
    c: Equal(g4,g0)
    c: Equal(g5,g0)
    c: Parallel(g4,g0)
    c: Parallel(g5,g0)
    c: Coincident(g4,g2)
    c: Coincident(g5,g1)
    c: Coincident(g6,g4)
    c: Coincident(g6,g5)
FEATURE [PartDesign::Body] Body  label="Struttura pistola"
  AllowCompound = false
  Group = -> [Sketch,Sketch002,Sketch004,DatumPlane,Sketch005,DatumPlane001,CopyCut,Sketch008,Sketch009,Sketch010,Sketch011,Sketch012,Sketch013,Sketch014,Sketch015,Sketch016,Sketch017,Sketch018,Sketch019,Sketch020,Sketch022,Sketch023,Sketch024,Sketch025,Sketch026,Sketch027,Sketch029,Sketch030,Sketch031,Sketch032,Sketch033,Sketch034,Sketch035,Sketch036,Sketch037,Sketch038,Sketch039,Sketch040,Sketch041,Sketch042,+17 more]
  Origin = -> Origin
FEATURE [Part::Extrusion] Extrude077  label="Extrude077 - scavo_nuovo_driver"
  Base = -> Sketch137
  Dir = (0,-1,2e-16)
  DirMode = 2
  FaceMakerClass = Part::FaceMakerBullseye
  FaceMakerMode = 3
  LengthFwd = 16.8
  LengthRev = 0
  Solid = true
  Symmetric = true
note: 2 file-system paths scrubbed to <path> (originals preserved in the JSON sidecar)
